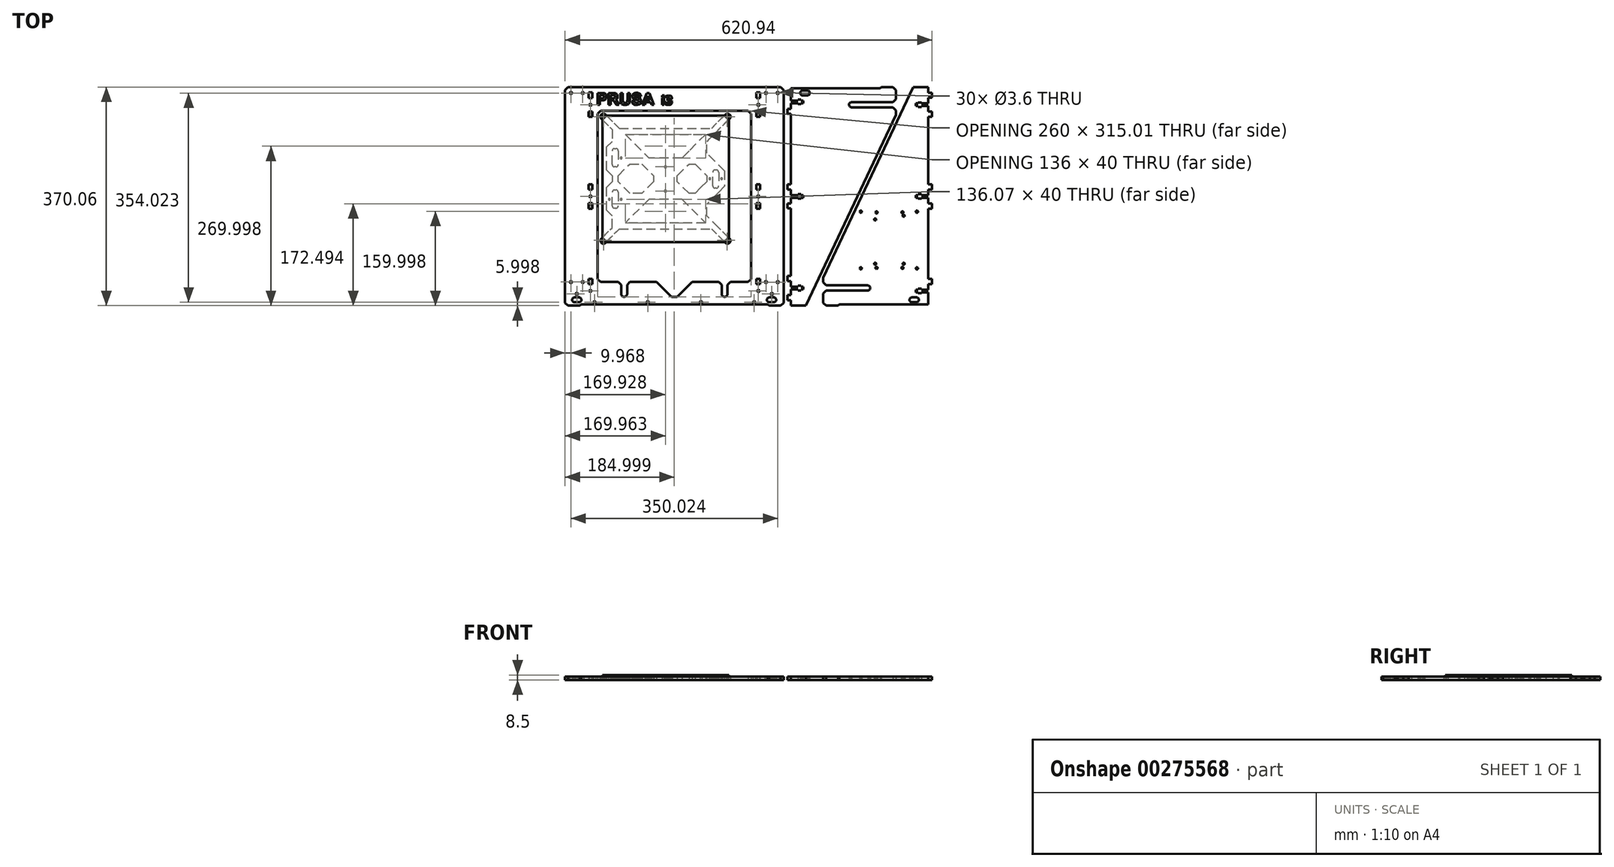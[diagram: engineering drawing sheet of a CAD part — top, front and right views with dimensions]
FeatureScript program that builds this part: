
annotation { "Feature Type Name" : "Feature", "Feature Type Description" : "" }
export const myFeature = defineFeature(function(context is Context, id is Id, definition is map)
    precondition{}
    {
        {
            var Q0;
            Q0=qCreatedBy(makeId("Top.planeOp"),FACE);
            var sketch = newSketch(context, id + "F0", { "sketchPlane" : qUnion([Q0])});
            skLineSegment(sketch, "E0", {"start": v(-112.47, -5.03) * mm, "end": v(-112.54, -5.03) * mm});
            skLineSegment(sketch, "E1", {"start": v(-72.47, -45.03) * mm, "end": v(-72.54, -45.03) * mm});
            skLineSegment(sketch, "E2", {"start": v(-168.47, -5.03) * mm, "end": v(-208.47, -45.03) * mm});
            skLineSegment(sketch, "E3", {"start": v(-112.47, -5.03) * mm, "end": v(-72.47, -45.03) * mm});
            skLineSegment(sketch, "E4", {"start": v(-112.54, -5.03) * mm, "end": v(-72.54, -45.03) * mm});
            skLineSegment(sketch, "E5", {"start": v(-168.54, -5.03) * mm, "end": v(-208.54, -45.03) * mm});
            skLineSegment(sketch, "E6", {"start": v(-208.47, -45.03) * mm, "end": v(-208.54, -45.03) * mm});
            skLineSegment(sketch, "E7", {"start": v(-168.47, -5.03) * mm, "end": v(-168.54, -5.03) * mm});
            skLineSegment(sketch, "E8", {"start": v(-305.47, -185.03) * mm, "end": v(-310.47, -180.22) * mm});
            skLineSegment(sketch, "E9", {"start": v(-310.47, 179.97) * mm, "end": v(-305.47, 184.97) * mm});
            skLineSegment(sketch, "E10", {"start": v(-305.47, 184.97) * mm, "end": v(54.53, 184.97) * mm});
            skLineSegment(sketch, "E11", {"start": v(54.53, 184.97) * mm, "end": v(59.53, 179.97) * mm});
            skLineSegment(sketch, "E12", {"start": v(59.53, -180.03) * mm, "end": v(54.53, -185.03) * mm});
            skLineSegment(sketch, "E13", {"start": v(34.53, -185.03) * mm, "end": v(32.53, -183.03) * mm});
            skLineSegment(sketch, "E14", {"start": v(32.53, -183.03) * mm, "end": v(-283.47, -183.03) * mm});
            skLineSegment(sketch, "E15", {"start": v(-283.47, -183.03) * mm, "end": v(-285.47, -185.03) * mm});
            skLineSegment(sketch, "E16", {"start": v(-230.47, -145.03) * mm, "end": v(-250.47, -145.03) * mm});
            skLineSegment(sketch, "E17", {"start": v(-250.47, -145.03) * mm, "end": v(-255.47, -140.03) * mm});
            skLineSegment(sketch, "E18", {"start": v(-255.47, -140.03) * mm, "end": v(-255.47, 139.97) * mm});
            skLineSegment(sketch, "E19", {"start": v(-255.47, 139.97) * mm, "end": v(-250.47, 144.97) * mm});
            skLineSegment(sketch, "E20", {"start": v(-250.47, 144.97) * mm, "end": v(-0.47, 144.97) * mm});
            skLineSegment(sketch, "E21", {"start": v(-0.47, 144.97) * mm, "end": v(4.53, 139.97) * mm});
            skLineSegment(sketch, "E22", {"start": v(4.53, 139.97) * mm, "end": v(4.53, -140.03) * mm});
            skLineSegment(sketch, "E23", {"start": v(4.53, -140.03) * mm, "end": v(-0.47, -145.03) * mm});
            skLineSegment(sketch, "E24", {"start": v(-0.47, -145.03) * mm, "end": v(-20.47, -145.03) * mm});
            skLineSegment(sketch, "E25", {"start": v(-130.47, -170.03) * mm, "end": v(-120.47, -170.03) * mm});
            skLineSegment(sketch, "E26", {"start": v(-120.47, -170.03) * mm, "end": v(-95.47, -145.03) * mm});
            skLineSegment(sketch, "E27", {"start": v(-130.47, -170.03) * mm, "end": v(-155.47, -145.03) * mm});
            skLineSegment(sketch, "E28", {"start": v(-200.47, -145.03) * mm, "end": v(-155.47, -145.03) * mm});
            skLineSegment(sketch, "E29", {"start": v(-95.47, -145.03) * mm, "end": v(-50.47, -145.03) * mm});
            skLineSegment(sketch, "E30", {"start": v(-80.47, 44.97) * mm, "end": v(-80.47, 44.9) * mm});
            skLineSegment(sketch, "E31", {"start": v(39.53, -179.03) * mm, "end": v(39.8, -179) * mm});
            skLineSegment(sketch, "E32", {"start": v(-310.47, -180.22) * mm, "end": v(-310.47, 179.97) * mm});
            skLineSegment(sketch, "E33", {"start": v(59.53, 179.97) * mm, "end": v(59.53, -180.03) * mm});
            skLineSegment(sketch, "E34", {"start": v(54.53, -185.03) * mm, "end": v(34.53, -185.03) * mm});
            skLineSegment(sketch, "E35", {"start": v(-285.47, -185.03) * mm, "end": v(-305.47, -185.03) * mm});
            skLineSegment(sketch, "E36", {"start": v(31.63, -173) * mm, "end": v(31.23, -173.96) * mm});
            skLineSegment(sketch, "E37", {"start": v(31.1, -175) * mm, "end": v(31.23, -176.03) * mm});
            skLineSegment(sketch, "E38", {"start": v(34.06, -171.13) * mm, "end": v(33.1, -171.53) * mm});
            skLineSegment(sketch, "E39", {"start": v(44.12, -171.13) * mm, "end": v(43.09, -171) * mm});
            skLineSegment(sketch, "E40", {"start": v(45.92, -177.82) * mm, "end": v(46.55, -177) * mm});
            skLineSegment(sketch, "E41", {"start": v(45.09, -178.46) * mm, "end": v(45.92, -177.82) * mm});
            skLineSegment(sketch, "E42", {"start": v(44.12, -178.86) * mm, "end": v(45.09, -178.46) * mm});
            skLineSegment(sketch, "E43", {"start": v(33.1, -178.46) * mm, "end": v(34.06, -178.86) * mm});
            skLineSegment(sketch, "E44", {"start": v(34.06, -178.86) * mm, "end": v(35.1, -179) * mm});
            skLineSegment(sketch, "E45", {"start": v(31.23, -176.03) * mm, "end": v(31.63, -177) * mm});
            skLineSegment(sketch, "E46", {"start": v(45.92, -172.17) * mm, "end": v(45.09, -171.53) * mm});
            skLineSegment(sketch, "E47", {"start": v(46.55, -173) * mm, "end": v(45.92, -172.17) * mm});
            skLineSegment(sketch, "E48", {"start": v(35.1, -171) * mm, "end": v(43.09, -171) * mm});
            skLineSegment(sketch, "E49", {"start": v(33.1, -171.53) * mm, "end": v(32.26, -172.17) * mm});
            skLineSegment(sketch, "E50", {"start": v(32.26, -172.17) * mm, "end": v(31.63, -173) * mm});
            skLineSegment(sketch, "E51", {"start": v(32.26, -177.82) * mm, "end": v(33.1, -178.46) * mm});
            skLineSegment(sketch, "E52", {"start": v(46.95, -173.96) * mm, "end": v(46.55, -173) * mm});
            skLineSegment(sketch, "E53", {"start": v(31.23, -173.96) * mm, "end": v(31.1, -175) * mm});
            skLineSegment(sketch, "E54", {"start": v(31.63, -177) * mm, "end": v(32.26, -177.82) * mm});
            skLineSegment(sketch, "E55", {"start": v(46.95, -176.03) * mm, "end": v(47.09, -175) * mm});
            skLineSegment(sketch, "E56", {"start": v(46.55, -177) * mm, "end": v(46.95, -176.03) * mm});
            skLineSegment(sketch, "E57", {"start": v(35.1, -171) * mm, "end": v(34.06, -171.13) * mm});
            skLineSegment(sketch, "E58", {"start": v(43.16, -179) * mm, "end": v(44.12, -178.86) * mm});
            skLineSegment(sketch, "E59", {"start": v(35.1, -179) * mm, "end": v(39.25, -179) * mm});
            skLineSegment(sketch, "E60", {"start": v(47.09, -175) * mm, "end": v(46.95, -173.96) * mm});
            skLineSegment(sketch, "E61", {"start": v(45.09, -171.53) * mm, "end": v(44.12, -171.13) * mm});
            skLineSegment(sketch, "E62", {"start": v(39.25, -179) * mm, "end": v(39.53, -179.03) * mm});
            skLineSegment(sketch, "E63", {"start": v(39.25, -179) * mm, "end": v(39.8, -179) * mm});
            skLineSegment(sketch, "E64", {"start": v(39.8, -179) * mm, "end": v(43.16, -179) * mm});
            skLineSegment(sketch, "E65", {"start": v(-298.44, -175) * mm, "end": v(-298.3, -176.03) * mm});
            skLineSegment(sketch, "E66", {"start": v(-297.9, -173) * mm, "end": v(-298.3, -173.96) * mm});
            skLineSegment(sketch, "E67", {"start": v(-295.48, -171.13) * mm, "end": v(-296.44, -171.53) * mm});
            skLineSegment(sketch, "E68", {"start": v(-285.41, -171.13) * mm, "end": v(-286.45, -171) * mm});
            skLineSegment(sketch, "E69", {"start": v(-283.62, -177.82) * mm, "end": v(-282.98, -177) * mm});
            skLineSegment(sketch, "E70", {"start": v(-284.45, -178.46) * mm, "end": v(-283.62, -177.82) * mm});
            skLineSegment(sketch, "E71", {"start": v(-285.41, -178.86) * mm, "end": v(-284.45, -178.46) * mm});
            skLineSegment(sketch, "E72", {"start": v(-296.44, -178.46) * mm, "end": v(-295.48, -178.86) * mm});
            skLineSegment(sketch, "E73", {"start": v(-295.48, -178.86) * mm, "end": v(-294.44, -179) * mm});
            skLineSegment(sketch, "E74", {"start": v(-298.3, -176.03) * mm, "end": v(-297.9, -177) * mm});
            skLineSegment(sketch, "E75", {"start": v(-283.62, -172.17) * mm, "end": v(-284.45, -171.53) * mm});
            skLineSegment(sketch, "E76", {"start": v(-282.98, -173) * mm, "end": v(-283.62, -172.17) * mm});
            skLineSegment(sketch, "E77", {"start": v(-294.44, -171) * mm, "end": v(-286.45, -171) * mm});
            skLineSegment(sketch, "E78", {"start": v(-296.44, -171.53) * mm, "end": v(-297.27, -172.17) * mm});
            skLineSegment(sketch, "E79", {"start": v(-297.27, -172.17) * mm, "end": v(-297.9, -173) * mm});
            skLineSegment(sketch, "E80", {"start": v(-297.27, -177.82) * mm, "end": v(-296.44, -178.46) * mm});
            skLineSegment(sketch, "E81", {"start": v(-282.59, -173.96) * mm, "end": v(-282.98, -173) * mm});
            skLineSegment(sketch, "E82", {"start": v(-298.3, -173.96) * mm, "end": v(-298.44, -175) * mm});
            skLineSegment(sketch, "E83", {"start": v(-297.9, -177) * mm, "end": v(-297.27, -177.82) * mm});
            skLineSegment(sketch, "E84", {"start": v(-282.59, -176.03) * mm, "end": v(-282.45, -175) * mm});
            skLineSegment(sketch, "E85", {"start": v(-282.98, -177) * mm, "end": v(-282.59, -176.03) * mm});
            skLineSegment(sketch, "E86", {"start": v(-294.44, -171) * mm, "end": v(-295.48, -171.13) * mm});
            skLineSegment(sketch, "E87", {"start": v(-286.38, -179) * mm, "end": v(-285.41, -178.86) * mm});
            skLineSegment(sketch, "E88", {"start": v(-294.44, -179) * mm, "end": v(-286.38, -179) * mm});
            skLineSegment(sketch, "E89", {"start": v(-282.45, -175) * mm, "end": v(-282.59, -173.96) * mm});
            skLineSegment(sketch, "E90", {"start": v(-284.45, -171.53) * mm, "end": v(-285.41, -171.13) * mm});
            skLineSegment(sketch, "E91", {"start": v(13.28, 166.71) * mm, "end": v(13.28, 175.71) * mm});
            skLineSegment(sketch, "E92", {"start": v(13.28, 175.71) * mm, "end": v(19.78, 175.71) * mm});
            skLineSegment(sketch, "E93", {"start": v(19.78, 175.71) * mm, "end": v(19.78, 166.71) * mm});
            skLineSegment(sketch, "E94", {"start": v(19.78, 166.71) * mm, "end": v(13.28, 166.71) * mm});
            skLineSegment(sketch, "E95", {"start": v(13.28, 134.41) * mm, "end": v(13.28, 143.41) * mm});
            skLineSegment(sketch, "E96", {"start": v(13.28, 143.41) * mm, "end": v(19.78, 143.41) * mm});
            skLineSegment(sketch, "E97", {"start": v(19.78, 143.41) * mm, "end": v(19.78, 134.41) * mm});
            skLineSegment(sketch, "E98", {"start": v(19.78, 134.41) * mm, "end": v(13.28, 134.41) * mm});
            skLineSegment(sketch, "E99", {"start": v(13.28, 11.62) * mm, "end": v(13.28, 20.62) * mm});
            skLineSegment(sketch, "E100", {"start": v(13.28, 20.62) * mm, "end": v(19.78, 20.62) * mm});
            skLineSegment(sketch, "E101", {"start": v(19.78, 20.62) * mm, "end": v(19.78, 11.62) * mm});
            skLineSegment(sketch, "E102", {"start": v(19.78, 11.62) * mm, "end": v(13.28, 11.62) * mm});
            skLineSegment(sketch, "E103", {"start": v(13.28, -20.68) * mm, "end": v(13.28, -11.68) * mm});
            skLineSegment(sketch, "E104", {"start": v(13.28, -11.68) * mm, "end": v(19.78, -11.68) * mm});
            skLineSegment(sketch, "E105", {"start": v(19.78, -11.68) * mm, "end": v(19.78, -20.68) * mm});
            skLineSegment(sketch, "E106", {"start": v(19.78, -20.68) * mm, "end": v(13.28, -20.68) * mm});
            skLineSegment(sketch, "E107", {"start": v(13.28, -148.38) * mm, "end": v(13.28, -139.38) * mm});
            skLineSegment(sketch, "E108", {"start": v(13.28, -139.38) * mm, "end": v(19.78, -139.38) * mm});
            skLineSegment(sketch, "E109", {"start": v(19.78, -139.38) * mm, "end": v(19.78, -148.38) * mm});
            skLineSegment(sketch, "E110", {"start": v(19.78, -148.38) * mm, "end": v(13.28, -148.38) * mm});
            skLineSegment(sketch, "E111", {"start": v(-270.72, 166.71) * mm, "end": v(-270.72, 175.71) * mm});
            skLineSegment(sketch, "E112", {"start": v(-270.72, 175.71) * mm, "end": v(-264.22, 175.71) * mm});
            skLineSegment(sketch, "E113", {"start": v(-264.22, 175.71) * mm, "end": v(-264.22, 166.71) * mm});
            skLineSegment(sketch, "E114", {"start": v(-264.22, 166.71) * mm, "end": v(-270.72, 166.71) * mm});
            skLineSegment(sketch, "E115", {"start": v(-270.72, 134.41) * mm, "end": v(-270.72, 143.41) * mm});
            skLineSegment(sketch, "E116", {"start": v(-270.72, 143.41) * mm, "end": v(-264.22, 143.41) * mm});
            skLineSegment(sketch, "E117", {"start": v(-264.22, 143.41) * mm, "end": v(-264.22, 134.41) * mm});
            skLineSegment(sketch, "E118", {"start": v(-264.22, 134.41) * mm, "end": v(-270.72, 134.41) * mm});
            skLineSegment(sketch, "E119", {"start": v(-270.72, 11.62) * mm, "end": v(-270.72, 20.62) * mm});
            skLineSegment(sketch, "E120", {"start": v(-270.72, 20.62) * mm, "end": v(-264.22, 20.62) * mm});
            skLineSegment(sketch, "E121", {"start": v(-264.22, 20.62) * mm, "end": v(-264.22, 11.62) * mm});
            skLineSegment(sketch, "E122", {"start": v(-264.22, 11.62) * mm, "end": v(-270.72, 11.62) * mm});
            skLineSegment(sketch, "E123", {"start": v(-270.72, -20.68) * mm, "end": v(-270.72, -11.68) * mm});
            skLineSegment(sketch, "E124", {"start": v(-270.72, -11.68) * mm, "end": v(-264.22, -11.68) * mm});
            skLineSegment(sketch, "E125", {"start": v(-264.22, -11.68) * mm, "end": v(-264.22, -20.68) * mm});
            skLineSegment(sketch, "E126", {"start": v(-264.22, -20.68) * mm, "end": v(-270.72, -20.68) * mm});
            skLineSegment(sketch, "E127", {"start": v(-270.72, -148.38) * mm, "end": v(-270.72, -139.38) * mm});
            skLineSegment(sketch, "E128", {"start": v(-270.72, -139.38) * mm, "end": v(-264.22, -139.38) * mm});
            skLineSegment(sketch, "E129", {"start": v(-264.22, -139.38) * mm, "end": v(-264.22, -148.38) * mm});
            skLineSegment(sketch, "E130", {"start": v(-264.22, -148.38) * mm, "end": v(-270.72, -148.38) * mm});
            skLineSegment(sketch, "E131", {"start": v(310.47, 134.51) * mm, "end": v(310.47, 143.31) * mm});
            skLineSegment(sketch, "E132", {"start": v(304.37, -148.28) * mm, "end": v(310.47, -148.28) * mm});
            skLineSegment(sketch, "E133", {"start": v(310.47, -148.28) * mm, "end": v(310.47, -139.48) * mm});
            skLineSegment(sketch, "E134", {"start": v(310.47, -139.48) * mm, "end": v(304.37, -139.48) * mm});
            skLineSegment(sketch, "E135", {"start": v(304.37, -139.48) * mm, "end": v(304.37, -20.58) * mm});
            skLineSegment(sketch, "E136", {"start": v(88.26, 177.03) * mm, "end": v(88.9, 177.86) * mm});
            skLineSegment(sketch, "E137", {"start": v(103.58, 176.07) * mm, "end": v(103.72, 175.03) * mm});
            skLineSegment(sketch, "E138", {"start": v(103.18, 177.03) * mm, "end": v(103.58, 176.07) * mm});
            skLineSegment(sketch, "E139", {"start": v(83.78, 2.23) * mm, "end": v(71.78, 2.23) * mm});
            skLineSegment(sketch, "E140", {"start": v(170.33, 156.17) * mm, "end": v(170.77, 157.23) * mm});
            skLineSegment(sketch, "E141", {"start": v(91.72, 171.03) * mm, "end": v(90.69, 171.17) * mm});
            skLineSegment(sketch, "E142", {"start": v(99.78, 179.03) * mm, "end": v(100.75, 178.9) * mm});
            skLineSegment(sketch, "E143", {"start": v(91.72, 179.03) * mm, "end": v(99.78, 179.03) * mm});
            skLineSegment(sketch, "E144", {"start": v(171.47, 151.92) * mm, "end": v(170.77, 152.83) * mm});
            skLineSegment(sketch, "E145", {"start": v(170.18, 155.03) * mm, "end": v(170.33, 156.17) * mm});
            skLineSegment(sketch, "E146", {"start": v(83.78, -3.97) * mm, "end": v(88.88, -3.97) * mm});
            skLineSegment(sketch, "E147", {"start": v(224.58, 185.03) * mm, "end": v(244.58, 185.03) * mm});
            skLineSegment(sketch, "E148", {"start": v(170.77, 157.23) * mm, "end": v(171.47, 158.14) * mm});
            skLineSegment(sketch, "E149", {"start": v(88.88, 162.24) * mm, "end": v(88.88, 164.04) * mm});
            skLineSegment(sketch, "E150", {"start": v(83.78, 162.24) * mm, "end": v(71.78, 162.24) * mm});
            skLineSegment(sketch, "E151", {"start": v(83.78, 164.04) * mm, "end": v(83.78, 162.24) * mm});
            skLineSegment(sketch, "E152", {"start": v(71.78, 157.84) * mm, "end": v(71.78, 148.28) * mm});
            skLineSegment(sketch, "E153", {"start": v(83.78, -151.05) * mm, "end": v(83.78, -152.85) * mm});
            skLineSegment(sketch, "E154", {"start": v(83.78, -157.25) * mm, "end": v(83.78, -159.05) * mm});
            skLineSegment(sketch, "E155", {"start": v(92.88, -157.25) * mm, "end": v(92.88, -152.85) * mm});
            skLineSegment(sketch, "E156", {"start": v(88.88, -157.25) * mm, "end": v(92.88, -157.25) * mm});
            skLineSegment(sketch, "E157", {"start": v(88.88, -157.25) * mm, "end": v(88.88, -159.05) * mm});
            skLineSegment(sketch, "E158", {"start": v(71.78, -157.25) * mm, "end": v(83.78, -157.25) * mm});
            skLineSegment(sketch, "E159", {"start": v(92.88, -152.85) * mm, "end": v(88.88, -152.85) * mm});
            skLineSegment(sketch, "E160", {"start": v(83.78, -152.85) * mm, "end": v(71.78, -152.85) * mm});
            skLineSegment(sketch, "E161", {"start": v(88.88, -151.05) * mm, "end": v(83.78, -151.05) * mm});
            skLineSegment(sketch, "E162", {"start": v(304.37, -183.03) * mm, "end": v(153.57, -183.03) * mm});
            skLineSegment(sketch, "E163", {"start": v(273.61, -172.2) * mm, "end": v(274.44, -171.57) * mm});
            skLineSegment(sketch, "E164", {"start": v(272.97, -173.03) * mm, "end": v(273.61, -172.2) * mm});
            skLineSegment(sketch, "E165", {"start": v(284.43, -171.03) * mm, "end": v(276.44, -171.03) * mm});
            skLineSegment(sketch, "E166", {"start": v(203.77, -151.22) * mm, "end": v(204.68, -151.92) * mm});
            skLineSegment(sketch, "E167", {"start": v(283.27, -2.23) * mm, "end": v(287.27, -2.23) * mm});
            skLineSegment(sketch, "E168", {"start": v(202.71, -150.78) * mm, "end": v(203.77, -151.22) * mm});
            skLineSegment(sketch, "E169", {"start": v(287.27, -4.03) * mm, "end": v(292.37, -4.03) * mm});
            skLineSegment(sketch, "E170", {"start": v(286.43, -171.57) * mm, "end": v(287.26, -172.2) * mm});
            skLineSegment(sketch, "E171", {"start": v(304.37, -157.84) * mm, "end": v(292.37, -157.84) * mm});
            skLineSegment(sketch, "E172", {"start": v(292.37, -157.84) * mm, "end": v(292.37, -156.04) * mm});
            skLineSegment(sketch, "E173", {"start": v(283.27, -162.24) * mm, "end": v(287.27, -162.24) * mm});
            skLineSegment(sketch, "E174", {"start": v(287.27, -164.04) * mm, "end": v(292.37, -164.04) * mm});
            skLineSegment(sketch, "E175", {"start": v(292.37, -156.04) * mm, "end": v(287.27, -156.04) * mm});
            skLineSegment(sketch, "E176", {"start": v(287.27, -162.24) * mm, "end": v(287.27, -164.04) * mm});
            skLineSegment(sketch, "E177", {"start": v(292.37, -162.24) * mm, "end": v(304.37, -162.24) * mm});
            skLineSegment(sketch, "E178", {"start": v(292.37, -164.04) * mm, "end": v(292.37, -162.24) * mm});
            skLineSegment(sketch, "E179", {"start": v(304.37, -157.84) * mm, "end": v(304.37, -148.28) * mm});
            skLineSegment(sketch, "E180", {"start": v(103.58, 174) * mm, "end": v(103.18, 173.03) * mm});
            skLineSegment(sketch, "E181", {"start": v(273.61, -177.86) * mm, "end": v(272.97, -177.03) * mm});
            skLineSegment(sketch, "E182", {"start": v(274.44, -178.5) * mm, "end": v(273.61, -177.86) * mm});
            skLineSegment(sketch, "E183", {"start": v(275.4, -178.9) * mm, "end": v(274.44, -178.5) * mm});
            skLineSegment(sketch, "E184", {"start": v(304.37, 2.17) * mm, "end": v(292.37, 2.17) * mm});
            skLineSegment(sketch, "E185", {"start": v(286.43, -178.5) * mm, "end": v(285.47, -178.9) * mm});
            skLineSegment(sketch, "E186", {"start": v(285.47, -178.9) * mm, "end": v(284.43, -179.03) * mm});
            skLineSegment(sketch, "E187", {"start": v(288.3, -176.07) * mm, "end": v(287.9, -177.03) * mm});
            skLineSegment(sketch, "E188", {"start": v(203.77, -158.84) * mm, "end": v(202.71, -159.28) * mm});
            skLineSegment(sketch, "E189", {"start": v(71.78, -175.61) * mm, "end": v(71.78, -184.97) * mm});
            skLineSegment(sketch, "E190", {"start": v(65.68, -143.31) * mm, "end": v(71.78, -143.31) * mm});
            skLineSegment(sketch, "E191", {"start": v(71.78, -134.51) * mm, "end": v(65.68, -134.51) * mm});
            skLineSegment(sketch, "E192", {"start": v(65.68, -134.51) * mm, "end": v(65.68, -143.31) * mm});
            skLineSegment(sketch, "E193", {"start": v(71.78, 148.28) * mm, "end": v(65.68, 148.28) * mm});
            skLineSegment(sketch, "E194", {"start": v(65.68, 148.28) * mm, "end": v(65.68, 139.48) * mm});
            skLineSegment(sketch, "E195", {"start": v(65.68, 139.48) * mm, "end": v(71.78, 139.48) * mm});
            skLineSegment(sketch, "E196", {"start": v(71.78, 139.48) * mm, "end": v(71.78, 20.58) * mm});
            skLineSegment(sketch, "E197", {"start": v(83.78, -2.17) * mm, "end": v(83.78, -3.97) * mm});
            skLineSegment(sketch, "E198", {"start": v(244.58, 185.03) * mm, "end": v(249.58, 180.03) * mm});
            skLineSegment(sketch, "E199", {"start": v(222.58, 183.03) * mm, "end": v(224.58, 185.03) * mm});
            skLineSegment(sketch, "E200", {"start": v(87.86, 174) * mm, "end": v(87.72, 175.03) * mm});
            skLineSegment(sketch, "E201", {"start": v(310.47, 20.52) * mm, "end": v(304.37, 20.52) * mm});
            skLineSegment(sketch, "E202", {"start": v(304.37, 20.52) * mm, "end": v(304.37, 134.51) * mm});
            skLineSegment(sketch, "E203", {"start": v(310.47, -11.78) * mm, "end": v(304.37, -11.78) * mm});
            skLineSegment(sketch, "E204", {"start": v(304.37, -20.58) * mm, "end": v(310.47, -20.58) * mm});
            skLineSegment(sketch, "E205", {"start": v(310.47, -20.58) * mm, "end": v(310.47, -11.78) * mm});
            skLineSegment(sketch, "E206", {"start": v(304.37, 11.72) * mm, "end": v(304.37, 2.17) * mm});
            skLineSegment(sketch, "E207", {"start": v(304.37, -2.23) * mm, "end": v(304.37, -11.78) * mm});
            skLineSegment(sketch, "E208", {"start": v(304.37, 166.81) * mm, "end": v(310.47, 166.81) * mm});
            skLineSegment(sketch, "E209", {"start": v(310.47, 166.81) * mm, "end": v(310.47, 175.61) * mm});
            skLineSegment(sketch, "E210", {"start": v(310.47, 175.61) * mm, "end": v(304.37, 175.61) * mm});
            skLineSegment(sketch, "E211", {"start": v(304.37, 175.61) * mm, "end": v(304.37, 184.97) * mm});
            skLineSegment(sketch, "E212", {"start": v(310.47, 143.31) * mm, "end": v(304.37, 143.31) * mm});
            skLineSegment(sketch, "E213", {"start": v(304.37, 134.51) * mm, "end": v(310.47, 134.51) * mm});
            skLineSegment(sketch, "E214", {"start": v(92.88, -2.17) * mm, "end": v(92.88, 2.23) * mm});
            skLineSegment(sketch, "E215", {"start": v(249.58, 138.03) * mm, "end": v(97.18, -184.97) * mm});
            skLineSegment(sketch, "E216", {"start": v(88.88, -2.17) * mm, "end": v(92.88, -2.17) * mm});
            skLineSegment(sketch, "E217", {"start": v(88.88, -2.17) * mm, "end": v(88.88, -3.97) * mm});
            skLineSegment(sketch, "E218", {"start": v(100.75, 171.17) * mm, "end": v(99.72, 171.03) * mm});
            skLineSegment(sketch, "E219", {"start": v(71.78, -184.97) * mm, "end": v(97.18, -184.97) * mm});
            skLineSegment(sketch, "E220", {"start": v(71.78, 2.23) * mm, "end": v(71.78, 11.78) * mm});
            skLineSegment(sketch, "E221", {"start": v(71.78, -166.81) * mm, "end": v(65.68, -166.81) * mm});
            skLineSegment(sketch, "E222", {"start": v(65.68, -166.81) * mm, "end": v(65.68, -175.61) * mm});
            skLineSegment(sketch, "E223", {"start": v(65.68, -175.61) * mm, "end": v(71.78, -175.61) * mm});
            skLineSegment(sketch, "E224", {"start": v(126.57, -180.03) * mm, "end": v(126.57, -164.43) * mm});
            skLineSegment(sketch, "E225", {"start": v(287.9, -173.03) * mm, "end": v(288.3, -174) * mm});
            skLineSegment(sketch, "E226", {"start": v(288.43, -175.03) * mm, "end": v(288.3, -176.07) * mm});
            skLineSegment(sketch, "E227", {"start": v(285.47, -171.17) * mm, "end": v(286.43, -171.57) * mm});
            skLineSegment(sketch, "E228", {"start": v(292.37, -4.03) * mm, "end": v(292.37, -2.23) * mm});
            skLineSegment(sketch, "E229", {"start": v(83.78, -159.05) * mm, "end": v(88.88, -159.05) * mm});
            skLineSegment(sketch, "E230", {"start": v(88.88, -152.85) * mm, "end": v(88.88, -151.05) * mm});
            skLineSegment(sketch, "E231", {"start": v(71.78, -157.25) * mm, "end": v(71.78, -166.81) * mm});
            skLineSegment(sketch, "E232", {"start": v(71.78, -152.85) * mm, "end": v(71.78, -143.31) * mm});
            skLineSegment(sketch, "E233", {"start": v(92.88, 157.84) * mm, "end": v(92.88, 162.24) * mm});
            skLineSegment(sketch, "E234", {"start": v(88.88, 157.84) * mm, "end": v(92.88, 157.84) * mm});
            skLineSegment(sketch, "E235", {"start": v(88.88, 157.84) * mm, "end": v(88.88, 156.04) * mm});
            skLineSegment(sketch, "E236", {"start": v(71.78, 157.84) * mm, "end": v(83.78, 157.84) * mm});
            skLineSegment(sketch, "E237", {"start": v(83.78, 157.84) * mm, "end": v(83.78, 156.04) * mm});
            skLineSegment(sketch, "E238", {"start": v(92.88, 162.24) * mm, "end": v(88.88, 162.24) * mm});
            skLineSegment(sketch, "E239", {"start": v(174.58, 150.63) * mm, "end": v(173.45, 150.78) * mm});
            skLineSegment(sketch, "E240", {"start": v(102.55, 177.86) * mm, "end": v(103.18, 177.03) * mm});
            skLineSegment(sketch, "E241", {"start": v(101.72, 178.5) * mm, "end": v(102.55, 177.86) * mm});
            skLineSegment(sketch, "E242", {"start": v(100.75, 178.9) * mm, "end": v(101.72, 178.5) * mm});
            skLineSegment(sketch, "E243", {"start": v(71.78, -2.17) * mm, "end": v(83.78, -2.17) * mm});
            skLineSegment(sketch, "E244", {"start": v(89.72, 178.5) * mm, "end": v(90.69, 178.9) * mm});
            skLineSegment(sketch, "E245", {"start": v(90.69, 178.9) * mm, "end": v(91.72, 179.03) * mm});
            skLineSegment(sketch, "E246", {"start": v(87.86, 176.07) * mm, "end": v(88.26, 177.03) * mm});
            skLineSegment(sketch, "E247", {"start": v(172.38, 158.84) * mm, "end": v(173.45, 159.28) * mm});
            skLineSegment(sketch, "E248", {"start": v(283.27, 2.17) * mm, "end": v(283.27, -2.23) * mm});
            skLineSegment(sketch, "E249", {"start": v(126.57, -138.03) * mm, "end": v(278.97, 184.97) * mm});
            skLineSegment(sketch, "E250", {"start": v(287.27, 2.17) * mm, "end": v(283.27, 2.17) * mm});
            skLineSegment(sketch, "E251", {"start": v(287.27, 2.17) * mm, "end": v(287.27, 3.97) * mm});
            skLineSegment(sketch, "E252", {"start": v(275.4, -171.17) * mm, "end": v(276.44, -171.03) * mm});
            skLineSegment(sketch, "E253", {"start": v(304.37, 184.97) * mm, "end": v(278.97, 184.97) * mm});
            skLineSegment(sketch, "E254", {"start": v(201.57, -150.63) * mm, "end": v(202.71, -150.78) * mm});
            skLineSegment(sketch, "E255", {"start": v(272.97, -177.03) * mm, "end": v(272.57, -176.07) * mm});
            skLineSegment(sketch, "E256", {"start": v(292.37, -2.23) * mm, "end": v(304.37, -2.23) * mm});
            skLineSegment(sketch, "E257", {"start": v(205.82, -156.17) * mm, "end": v(205.38, -157.23) * mm});
            skLineSegment(sketch, "E258", {"start": v(284.43, -171.03) * mm, "end": v(285.47, -171.17) * mm});
            skLineSegment(sketch, "E259", {"start": v(276.37, -179.03) * mm, "end": v(275.4, -178.9) * mm});
            skLineSegment(sketch, "E260", {"start": v(284.43, -179.03) * mm, "end": v(276.37, -179.03) * mm});
            skLineSegment(sketch, "E261", {"start": v(204.68, -151.92) * mm, "end": v(205.38, -152.83) * mm});
            skLineSegment(sketch, "E262", {"start": v(205.97, -155.03) * mm, "end": v(205.82, -156.17) * mm});
            skLineSegment(sketch, "E263", {"start": v(292.37, 3.97) * mm, "end": v(287.27, 3.97) * mm});
            skLineSegment(sketch, "E264", {"start": v(151.57, -185.03) * mm, "end": v(131.57, -185.03) * mm});
            skLineSegment(sketch, "E265", {"start": v(205.38, -157.23) * mm, "end": v(204.68, -158.14) * mm});
            skLineSegment(sketch, "E266", {"start": v(287.27, -2.23) * mm, "end": v(287.27, -4.03) * mm});
            skLineSegment(sketch, "E267", {"start": v(283.27, 157.25) * mm, "end": v(283.27, 152.85) * mm});
            skLineSegment(sketch, "E268", {"start": v(287.27, 157.25) * mm, "end": v(283.27, 157.25) * mm});
            skLineSegment(sketch, "E269", {"start": v(287.27, 157.25) * mm, "end": v(287.27, 159.05) * mm});
            skLineSegment(sketch, "E270", {"start": v(304.37, 157.25) * mm, "end": v(292.37, 157.25) * mm});
            skLineSegment(sketch, "E271", {"start": v(283.27, 152.85) * mm, "end": v(287.27, 152.85) * mm});
            skLineSegment(sketch, "E272", {"start": v(292.37, 152.85) * mm, "end": v(304.37, 152.85) * mm});
            skLineSegment(sketch, "E273", {"start": v(287.27, 151.05) * mm, "end": v(292.37, 151.05) * mm});
            skLineSegment(sketch, "E274", {"start": v(292.37, 159.05) * mm, "end": v(287.27, 159.05) * mm});
            skLineSegment(sketch, "E275", {"start": v(287.27, 152.85) * mm, "end": v(287.27, 151.05) * mm});
            skLineSegment(sketch, "E276", {"start": v(304.37, 157.25) * mm, "end": v(304.37, 166.81) * mm});
            skLineSegment(sketch, "E277", {"start": v(304.37, 152.85) * mm, "end": v(304.37, 143.31) * mm});
            skLineSegment(sketch, "E278", {"start": v(283.27, -157.84) * mm, "end": v(283.27, -162.24) * mm});
            skLineSegment(sketch, "E279", {"start": v(287.27, -157.84) * mm, "end": v(283.27, -157.84) * mm});
            skLineSegment(sketch, "E280", {"start": v(287.27, -157.84) * mm, "end": v(287.27, -156.04) * mm});
            skLineSegment(sketch, "E281", {"start": v(292.37, 151.05) * mm, "end": v(292.37, 152.85) * mm});
            skLineSegment(sketch, "E282", {"start": v(292.37, 157.25) * mm, "end": v(292.37, 159.05) * mm});
            skLineSegment(sketch, "E283", {"start": v(88.88, 2.23) * mm, "end": v(88.88, 4.03) * mm});
            skLineSegment(sketch, "E284", {"start": v(171.47, 158.14) * mm, "end": v(172.38, 158.84) * mm});
            skLineSegment(sketch, "E285", {"start": v(103.72, 175.03) * mm, "end": v(103.58, 174) * mm});
            skLineSegment(sketch, "E286", {"start": v(101.72, 171.57) * mm, "end": v(100.75, 171.17) * mm});
            skLineSegment(sketch, "E287", {"start": v(244.58, 159.43) * mm, "end": v(174.58, 159.43) * mm});
            skLineSegment(sketch, "E288", {"start": v(244.58, 159.43) * mm, "end": v(249.58, 164.43) * mm});
            skLineSegment(sketch, "E289", {"start": v(244.58, 150.63) * mm, "end": v(174.58, 150.63) * mm});
            skLineSegment(sketch, "E290", {"start": v(249.58, 145.63) * mm, "end": v(249.58, 138.03) * mm});
            skLineSegment(sketch, "E291", {"start": v(244.58, 150.63) * mm, "end": v(249.58, 145.63) * mm});
            skLineSegment(sketch, "E292", {"start": v(71.78, -11.72) * mm, "end": v(65.68, -11.72) * mm});
            skLineSegment(sketch, "E293", {"start": v(65.68, -11.72) * mm, "end": v(65.68, -20.52) * mm});
            skLineSegment(sketch, "E294", {"start": v(65.68, -20.52) * mm, "end": v(71.78, -20.52) * mm});
            skLineSegment(sketch, "E295", {"start": v(71.78, -20.52) * mm, "end": v(71.78, -134.51) * mm});
            skLineSegment(sketch, "E296", {"start": v(65.68, 11.78) * mm, "end": v(71.78, 11.78) * mm});
            skLineSegment(sketch, "E297", {"start": v(71.78, 20.58) * mm, "end": v(65.68, 20.58) * mm});
            skLineSegment(sketch, "E298", {"start": v(65.68, 20.58) * mm, "end": v(65.68, 11.78) * mm});
            skLineSegment(sketch, "E299", {"start": v(71.78, -11.72) * mm, "end": v(71.78, -2.17) * mm});
            skLineSegment(sketch, "E300", {"start": v(88.88, 164.04) * mm, "end": v(83.78, 164.04) * mm});
            skLineSegment(sketch, "E301", {"start": v(91.72, 171.03) * mm, "end": v(99.72, 171.03) * mm});
            skLineSegment(sketch, "E302", {"start": v(172.38, 151.22) * mm, "end": v(171.47, 151.92) * mm});
            skLineSegment(sketch, "E303", {"start": v(92.88, 2.23) * mm, "end": v(88.88, 2.23) * mm});
            skLineSegment(sketch, "E304", {"start": v(173.45, 150.78) * mm, "end": v(172.38, 151.22) * mm});
            skLineSegment(sketch, "E305", {"start": v(88.88, 4.03) * mm, "end": v(83.78, 4.03) * mm});
            skLineSegment(sketch, "E306", {"start": v(83.78, 156.04) * mm, "end": v(88.88, 156.04) * mm});
            skLineSegment(sketch, "E307", {"start": v(89.72, 171.57) * mm, "end": v(88.9, 172.2) * mm});
            skLineSegment(sketch, "E308", {"start": v(88.9, 172.2) * mm, "end": v(88.26, 173.03) * mm});
            skLineSegment(sketch, "E309", {"start": v(88.9, 177.86) * mm, "end": v(89.72, 178.5) * mm});
            skLineSegment(sketch, "E310", {"start": v(170.77, 152.83) * mm, "end": v(170.33, 153.9) * mm});
            skLineSegment(sketch, "E311", {"start": v(170.33, 153.9) * mm, "end": v(170.18, 155.03) * mm});
            skLineSegment(sketch, "E312", {"start": v(71.78, 183.03) * mm, "end": v(71.78, 162.24) * mm});
            skLineSegment(sketch, "E313", {"start": v(173.45, 159.28) * mm, "end": v(174.58, 159.43) * mm});
            skLineSegment(sketch, "E314", {"start": v(249.58, 180.03) * mm, "end": v(249.58, 164.43) * mm});
            skLineSegment(sketch, "E315", {"start": v(88.26, 173.03) * mm, "end": v(87.86, 174) * mm});
            skLineSegment(sketch, "E316", {"start": v(87.72, 175.03) * mm, "end": v(87.86, 176.07) * mm});
            skLineSegment(sketch, "E317", {"start": v(90.69, 171.17) * mm, "end": v(89.72, 171.57) * mm});
            skLineSegment(sketch, "E318", {"start": v(83.78, 4.03) * mm, "end": v(83.78, 2.23) * mm});
            skLineSegment(sketch, "E319", {"start": v(204.68, -158.14) * mm, "end": v(203.77, -158.84) * mm});
            skLineSegment(sketch, "E320", {"start": v(272.44, -175.03) * mm, "end": v(272.57, -174) * mm});
            skLineSegment(sketch, "E321", {"start": v(274.44, -171.57) * mm, "end": v(275.4, -171.17) * mm});
            skLineSegment(sketch, "E322", {"start": v(131.57, -159.43) * mm, "end": v(201.57, -159.43) * mm});
            skLineSegment(sketch, "E323", {"start": v(131.57, -159.43) * mm, "end": v(126.57, -164.43) * mm});
            skLineSegment(sketch, "E324", {"start": v(131.57, -150.63) * mm, "end": v(201.57, -150.63) * mm});
            skLineSegment(sketch, "E325", {"start": v(126.57, -145.63) * mm, "end": v(126.57, -138.03) * mm});
            skLineSegment(sketch, "E326", {"start": v(131.57, -150.63) * mm, "end": v(126.57, -145.63) * mm});
            skLineSegment(sketch, "E327", {"start": v(304.37, 11.72) * mm, "end": v(310.47, 11.72) * mm});
            skLineSegment(sketch, "E328", {"start": v(310.47, 11.72) * mm, "end": v(310.47, 20.52) * mm});
            skLineSegment(sketch, "E329", {"start": v(287.26, -172.2) * mm, "end": v(287.9, -173.03) * mm});
            skLineSegment(sketch, "E330", {"start": v(287.26, -177.86) * mm, "end": v(286.43, -178.5) * mm});
            skLineSegment(sketch, "E331", {"start": v(205.38, -152.83) * mm, "end": v(205.82, -153.9) * mm});
            skLineSegment(sketch, "E332", {"start": v(205.82, -153.9) * mm, "end": v(205.97, -155.03) * mm});
            skLineSegment(sketch, "E333", {"start": v(272.57, -174) * mm, "end": v(272.97, -173.03) * mm});
            skLineSegment(sketch, "E334", {"start": v(292.37, 2.17) * mm, "end": v(292.37, 3.97) * mm});
            skLineSegment(sketch, "E335", {"start": v(131.57, -185.03) * mm, "end": v(126.57, -180.03) * mm});
            skLineSegment(sketch, "E336", {"start": v(153.57, -183.03) * mm, "end": v(151.57, -185.03) * mm});
            skLineSegment(sketch, "E337", {"start": v(288.3, -174) * mm, "end": v(288.43, -175.03) * mm});
            skLineSegment(sketch, "E338", {"start": v(287.9, -177.03) * mm, "end": v(287.26, -177.86) * mm});
            skLineSegment(sketch, "E339", {"start": v(272.57, -176.07) * mm, "end": v(272.44, -175.03) * mm});
            skLineSegment(sketch, "E340", {"start": v(304.37, -183.03) * mm, "end": v(304.37, -162.24) * mm});
            skLineSegment(sketch, "E341", {"start": v(202.71, -159.28) * mm, "end": v(201.57, -159.43) * mm});
            skLineSegment(sketch, "E342", {"start": v(71.78, 183.03) * mm, "end": v(222.58, 183.03) * mm});
            skLineSegment(sketch, "E343", {"start": v(102.55, 172.2) * mm, "end": v(101.72, 171.57) * mm});
            skLineSegment(sketch, "E344", {"start": v(103.18, 173.03) * mm, "end": v(102.55, 172.2) * mm});
            skLineSegment(sketch, "E345", {"start": v(188.2, -26.36) * mm, "end": v(188.15, -25.9) * mm});
            skLineSegment(sketch, "E346", {"start": v(286.7, -121.34) * mm, "end": v(286.76, -121.8) * mm});
            skLineSegment(sketch, "E347", {"start": v(286.52, -120.9) * mm, "end": v(286.7, -121.34) * mm});
            skLineSegment(sketch, "E348", {"start": v(286.24, -120.54) * mm, "end": v(286.52, -120.9) * mm});
            skLineSegment(sketch, "E349", {"start": v(191.68, -26.36) * mm, "end": v(191.5, -26.8) * mm});
            skLineSegment(sketch, "E350", {"start": v(191.24, -123.04) * mm, "end": v(190.87, -123.33) * mm});
            skLineSegment(sketch, "E351", {"start": v(191.53, -122.67) * mm, "end": v(191.24, -123.04) * mm});
            skLineSegment(sketch, "E352", {"start": v(189.07, -123.32) * mm, "end": v(188.7, -123.04) * mm});
            skLineSegment(sketch, "E353", {"start": v(188.41, -122.67) * mm, "end": v(188.23, -122.23) * mm});
            skLineSegment(sketch, "E354", {"start": v(189.5, -120.03) * mm, "end": v(189.9, -119.98) * mm});
            skLineSegment(sketch, "E355", {"start": v(286.74, -25.85) * mm, "end": v(286.68, -26.32) * mm});
            skLineSegment(sketch, "E356", {"start": v(285.4, -27.6) * mm, "end": v(284.94, -27.65) * mm});
            skLineSegment(sketch, "E357", {"start": v(188.39, -25) * mm, "end": v(188.67, -24.63) * mm});
            skLineSegment(sketch, "E358", {"start": v(189.9, -27.7) * mm, "end": v(189.48, -27.64) * mm});
            skLineSegment(sketch, "E359", {"start": v(284.04, -27.41) * mm, "end": v(283.67, -27.13) * mm});
            skLineSegment(sketch, "E360", {"start": v(283.17, -121.84) * mm, "end": v(283.16, -121.8) * mm});
            skLineSegment(sketch, "E361", {"start": v(189.48, -24.16) * mm, "end": v(189.95, -24.1) * mm});
            skLineSegment(sketch, "E362", {"start": v(284.06, -123.37) * mm, "end": v(283.69, -123.08) * mm});
            skLineSegment(sketch, "E363", {"start": v(213.85, -37.27) * mm, "end": v(214.31, -37.2) * mm});
            skLineSegment(sketch, "E364", {"start": v(212.75, -38.1) * mm, "end": v(213.04, -37.74) * mm});
            skLineSegment(sketch, "E365", {"start": v(189.04, -27.46) * mm, "end": v(188.67, -27.17) * mm});
            skLineSegment(sketch, "E366", {"start": v(216.08, -114.42) * mm, "end": v(215.9, -114.85) * mm});
            skLineSegment(sketch, "E367", {"start": v(215.9, -114.85) * mm, "end": v(215.62, -115.23) * mm});
            skLineSegment(sketch, "E368", {"start": v(190.41, -24.16) * mm, "end": v(190.85, -24.34) * mm});
            skLineSegment(sketch, "E369", {"start": v(285.43, -120.07) * mm, "end": v(285.86, -120.25) * mm});
            skLineSegment(sketch, "E370", {"start": v(283.69, -120.54) * mm, "end": v(284.06, -120.25) * mm});
            skLineSegment(sketch, "E371", {"start": v(283.4, -120.9) * mm, "end": v(283.69, -120.54) * mm});
            skLineSegment(sketch, "E372", {"start": v(283.22, -121.34) * mm, "end": v(283.4, -120.9) * mm});
            skLineSegment(sketch, "E373", {"start": v(189.95, -24.1) * mm, "end": v(190.41, -24.16) * mm});
            skLineSegment(sketch, "E374", {"start": v(213.07, -115.23) * mm, "end": v(212.79, -114.85) * mm});
            skLineSegment(sketch, "E375", {"start": v(212.79, -114.85) * mm, "end": v(212.6, -114.42) * mm});
            skLineSegment(sketch, "E376", {"start": v(263.48, -34.27) * mm, "end": v(263.04, -34.45) * mm});
            skLineSegment(sketch, "E377", {"start": v(259.04, -108.12) * mm, "end": v(259.04, -110.32) * mm});
            skLineSegment(sketch, "E378", {"start": v(259.04, -110.32) * mm, "end": v(258.74, -110.32) * mm});
            skLineSegment(sketch, "E379", {"start": v(259.04, -110.32) * mm, "end": v(259.36, -110.32) * mm});
            skLineSegment(sketch, "E380", {"start": v(188.23, -122.23) * mm, "end": v(188.17, -121.77) * mm});
            skLineSegment(sketch, "E381", {"start": v(189.07, -120.2) * mm, "end": v(189.5, -120.03) * mm});
            skLineSegment(sketch, "E382", {"start": v(261.02, -33.6) * mm, "end": v(260.84, -33.17) * mm});
            skLineSegment(sketch, "E383", {"start": v(262.11, -30.97) * mm, "end": v(262.58, -30.9) * mm});
            skLineSegment(sketch, "E384", {"start": v(263.48, -31.15) * mm, "end": v(263.62, -31.26) * mm});
            skLineSegment(sketch, "E385", {"start": v(264.14, -31.8) * mm, "end": v(264.32, -32.24) * mm});
            skLineSegment(sketch, "E386", {"start": v(286.76, -121.8) * mm, "end": v(286.7, -122.28) * mm});
            skLineSegment(sketch, "E387", {"start": v(190.41, -27.64) * mm, "end": v(189.94, -27.7) * mm});
            skLineSegment(sketch, "E388", {"start": v(189.94, -27.7) * mm, "end": v(189.9, -27.7) * mm});
            skLineSegment(sketch, "E389", {"start": v(191.48, -31.81) * mm, "end": v(192.63, -31.81) * mm});
            skLineSegment(sketch, "E390", {"start": v(191.48, -31.81) * mm, "end": v(191.48, -30.71) * mm});
            skLineSegment(sketch, "E391", {"start": v(262.11, -34.45) * mm, "end": v(261.75, -34.3) * mm});
            skLineSegment(sketch, "E392", {"start": v(216.05, -38.54) * mm, "end": v(216.11, -39) * mm});
            skLineSegment(sketch, "E393", {"start": v(213.04, -37.74) * mm, "end": v(213.41, -37.45) * mm});
            skLineSegment(sketch, "E394", {"start": v(213.41, -37.45) * mm, "end": v(213.85, -37.27) * mm});
            skLineSegment(sketch, "E395", {"start": v(190.44, -120.03) * mm, "end": v(190.87, -120.2) * mm});
            skLineSegment(sketch, "E396", {"start": v(189.97, -119.97) * mm, "end": v(190.44, -120.03) * mm});
            skLineSegment(sketch, "E397", {"start": v(284.96, -120) * mm, "end": v(285.43, -120.07) * mm});
            skLineSegment(sketch, "E398", {"start": v(283.22, -122.28) * mm, "end": v(283.17, -121.84) * mm});
            skLineSegment(sketch, "E399", {"start": v(215.87, -39.9) * mm, "end": v(215.59, -40.28) * mm});
            skLineSegment(sketch, "E400", {"start": v(214.78, -40.75) * mm, "end": v(214.31, -40.8) * mm});
            skLineSegment(sketch, "E401", {"start": v(259.18, -36) * mm, "end": v(258.88, -36.3) * mm});
            skLineSegment(sketch, "E402", {"start": v(216.99, -42.2) * mm, "end": v(216.69, -42.51) * mm});
            skLineSegment(sketch, "E403", {"start": v(216.99, -44.4) * mm, "end": v(217.3, -44.4) * mm});
            skLineSegment(sketch, "E404", {"start": v(216.99, -44.4) * mm, "end": v(216.69, -44.4) * mm});
            skLineSegment(sketch, "E405", {"start": v(283.16, -121.8) * mm, "end": v(283.22, -121.34) * mm});
            skLineSegment(sketch, "E406", {"start": v(284.5, -123.55) * mm, "end": v(284.06, -123.37) * mm});
            skLineSegment(sketch, "E407", {"start": v(283.2, -25.39) * mm, "end": v(283.38, -24.95) * mm});
            skLineSegment(sketch, "E408", {"start": v(191.75, -25.9) * mm, "end": v(191.68, -26.36) * mm});
            skLineSegment(sketch, "E409", {"start": v(261.3, -31.44) * mm, "end": v(261.68, -31.15) * mm});
            skLineSegment(sketch, "E410", {"start": v(261.02, -31.8) * mm, "end": v(261.3, -31.44) * mm});
            skLineSegment(sketch, "E411", {"start": v(188.2, -25.43) * mm, "end": v(188.39, -25) * mm});
            skLineSegment(sketch, "E412", {"start": v(260.84, -33.17) * mm, "end": v(260.78, -32.7) * mm});
            skLineSegment(sketch, "E413", {"start": v(193.58, -116.54) * mm, "end": v(194.73, -116.54) * mm});
            skLineSegment(sketch, "E414", {"start": v(193.58, -117.64) * mm, "end": v(194.73, -117.64) * mm});
            skLineSegment(sketch, "E415", {"start": v(194.73, -115.44) * mm, "end": v(193.58, -115.44) * mm});
            skLineSegment(sketch, "E416", {"start": v(193.58, -117.64) * mm, "end": v(193.58, -116.54) * mm});
            skLineSegment(sketch, "E417", {"start": v(282.06, -116.37) * mm, "end": v(282.06, -115.27) * mm});
            skLineSegment(sketch, "E418", {"start": v(280.9, -116.37) * mm, "end": v(282.06, -116.37) * mm});
            skLineSegment(sketch, "E419", {"start": v(280.9, -117.47) * mm, "end": v(280.9, -116.37) * mm});
            skLineSegment(sketch, "E420", {"start": v(191.76, -121.84) * mm, "end": v(191.7, -122.23) * mm});
            skLineSegment(sketch, "E421", {"start": v(283.38, -26.75) * mm, "end": v(283.2, -26.32) * mm});
            skLineSegment(sketch, "E422", {"start": v(191.22, -27.17) * mm, "end": v(190.84, -27.46) * mm});
            skLineSegment(sketch, "E423", {"start": v(264.31, -33.17) * mm, "end": v(264.13, -33.6) * mm});
            skLineSegment(sketch, "E424", {"start": v(285.86, -123.37) * mm, "end": v(285.43, -123.55) * mm});
            skLineSegment(sketch, "E425", {"start": v(286.24, -123.08) * mm, "end": v(285.86, -123.37) * mm});
            skLineSegment(sketch, "E426", {"start": v(286.52, -122.7) * mm, "end": v(286.24, -123.08) * mm});
            skLineSegment(sketch, "E427", {"start": v(286.7, -122.28) * mm, "end": v(286.52, -122.7) * mm});
            skLineSegment(sketch, "E428", {"start": v(264.13, -33.6) * mm, "end": v(263.85, -33.98) * mm});
            skLineSegment(sketch, "E429", {"start": v(263.04, -34.45) * mm, "end": v(262.58, -34.5) * mm});
            skLineSegment(sketch, "E430", {"start": v(212.6, -114.42) * mm, "end": v(212.55, -113.95) * mm});
            skLineSegment(sketch, "E431", {"start": v(215.9, -113.05) * mm, "end": v(216.08, -113.49) * mm});
            skLineSegment(sketch, "E432", {"start": v(261.68, -31.15) * mm, "end": v(262.11, -30.97) * mm});
            skLineSegment(sketch, "E433", {"start": v(261.68, -34.27) * mm, "end": v(261.53, -34.13) * mm});
            skLineSegment(sketch, "E434", {"start": v(285.84, -27.41) * mm, "end": v(285.4, -27.6) * mm});
            skLineSegment(sketch, "E435", {"start": v(286.68, -26.32) * mm, "end": v(286.5, -26.75) * mm});
            skLineSegment(sketch, "E436", {"start": v(283.38, -24.95) * mm, "end": v(283.67, -24.58) * mm});
            skLineSegment(sketch, "E437", {"start": v(280.9, -117.47) * mm, "end": v(282.06, -117.47) * mm});
            skLineSegment(sketch, "E438", {"start": v(282.06, -115.27) * mm, "end": v(280.9, -115.27) * mm});
            skLineSegment(sketch, "E439", {"start": v(259.18, -38.2) * mm, "end": v(259.5, -38.2) * mm});
            skLineSegment(sketch, "E440", {"start": v(259.18, -38.2) * mm, "end": v(258.88, -38.2) * mm});
            skLineSegment(sketch, "E441", {"start": v(259.18, -36) * mm, "end": v(259.18, -38.2) * mm});
            skLineSegment(sketch, "E442", {"start": v(215.25, -112.4) * mm, "end": v(215.36, -112.48) * mm});
            skLineSegment(sketch, "E443", {"start": v(190.84, -27.46) * mm, "end": v(190.41, -27.64) * mm});
            skLineSegment(sketch, "E444", {"start": v(188.39, -26.8) * mm, "end": v(188.2, -26.36) * mm});
            skLineSegment(sketch, "E445", {"start": v(190.87, -120.2) * mm, "end": v(191.24, -120.5) * mm});
            skLineSegment(sketch, "E446", {"start": v(218.12, -110.06) * mm, "end": v(218.44, -110.06) * mm});
            skLineSegment(sketch, "E447", {"start": v(218.12, -107.86) * mm, "end": v(217.82, -108.17) * mm});
            skLineSegment(sketch, "E448", {"start": v(218.12, -110.06) * mm, "end": v(217.82, -110.06) * mm});
            skLineSegment(sketch, "E449", {"start": v(218.12, -107.86) * mm, "end": v(218.12, -110.06) * mm});
            skLineSegment(sketch, "E450", {"start": v(259.04, -108.12) * mm, "end": v(258.74, -108.43) * mm});
            skLineSegment(sketch, "E451", {"start": v(263.04, -30.97) * mm, "end": v(263.48, -31.15) * mm});
            skLineSegment(sketch, "E452", {"start": v(283.4, -122.7) * mm, "end": v(283.22, -122.28) * mm});
            skLineSegment(sketch, "E453", {"start": v(284.5, -120.07) * mm, "end": v(284.9, -120.02) * mm});
            skLineSegment(sketch, "E454", {"start": v(212.57, -39.47) * mm, "end": v(212.51, -39) * mm});
            skLineSegment(sketch, "E455", {"start": v(261.7, -112.47) * mm, "end": v(262.14, -112.29) * mm});
            skLineSegment(sketch, "E456", {"start": v(260.87, -114.5) * mm, "end": v(260.8, -114.02) * mm});
            skLineSegment(sketch, "E457", {"start": v(213.07, -112.68) * mm, "end": v(213.45, -112.4) * mm});
            skLineSegment(sketch, "E458", {"start": v(214.31, -40.8) * mm, "end": v(213.85, -40.75) * mm});
            skLineSegment(sketch, "E459", {"start": v(213.85, -40.75) * mm, "end": v(213.46, -40.59) * mm});
            skLineSegment(sketch, "E460", {"start": v(264.32, -32.24) * mm, "end": v(264.38, -32.7) * mm});
            skLineSegment(sketch, "E461", {"start": v(262.14, -115.76) * mm, "end": v(261.96, -115.67) * mm});
            skLineSegment(sketch, "E462", {"start": v(261.7, -115.58) * mm, "end": v(261.33, -115.3) * mm});
            skLineSegment(sketch, "E463", {"start": v(261.33, -115.3) * mm, "end": v(261.05, -114.92) * mm});
            skLineSegment(sketch, "E464", {"start": v(190.85, -24.34) * mm, "end": v(191.22, -24.63) * mm});
            skLineSegment(sketch, "E465", {"start": v(191.22, -24.63) * mm, "end": v(191.5, -25) * mm});
            skLineSegment(sketch, "E466", {"start": v(213.41, -40.57) * mm, "end": v(213.3, -40.47) * mm});
            skLineSegment(sketch, "E467", {"start": v(213.04, -40.28) * mm, "end": v(212.75, -39.9) * mm});
            skLineSegment(sketch, "E468", {"start": v(212.75, -39.9) * mm, "end": v(212.57, -39.47) * mm});
            skLineSegment(sketch, "E469", {"start": v(190.87, -123.33) * mm, "end": v(190.44, -123.5) * mm});
            skLineSegment(sketch, "E470", {"start": v(190.44, -123.5) * mm, "end": v(189.97, -123.57) * mm});
            skLineSegment(sketch, "E471", {"start": v(189.97, -123.57) * mm, "end": v(189.5, -123.5) * mm});
            skLineSegment(sketch, "E472", {"start": v(284.06, -120.25) * mm, "end": v(284.5, -120.07) * mm});
            skLineSegment(sketch, "E473", {"start": v(188.17, -121.77) * mm, "end": v(188.23, -121.3) * mm});
            skLineSegment(sketch, "E474", {"start": v(189.5, -123.5) * mm, "end": v(189.07, -123.32) * mm});
            skLineSegment(sketch, "E475", {"start": v(189.9, -119.98) * mm, "end": v(189.97, -119.97) * mm});
            skLineSegment(sketch, "E476", {"start": v(284.96, -123.6) * mm, "end": v(284.5, -123.55) * mm});
            skLineSegment(sketch, "E477", {"start": v(188.15, -25.9) * mm, "end": v(188.2, -25.43) * mm});
            skLineSegment(sketch, "E478", {"start": v(285.43, -123.55) * mm, "end": v(284.96, -123.6) * mm});
            skLineSegment(sketch, "E479", {"start": v(188.7, -120.5) * mm, "end": v(189.07, -120.2) * mm});
            skLineSegment(sketch, "E480", {"start": v(188.41, -120.87) * mm, "end": v(188.7, -120.5) * mm});
            skLineSegment(sketch, "E481", {"start": v(188.23, -121.3) * mm, "end": v(188.41, -120.87) * mm});
            skLineSegment(sketch, "E482", {"start": v(213.88, -112.21) * mm, "end": v(214.35, -112.15) * mm});
            skLineSegment(sketch, "E483", {"start": v(214.35, -112.15) * mm, "end": v(214.81, -112.21) * mm});
            skLineSegment(sketch, "E484", {"start": v(213.45, -112.4) * mm, "end": v(213.88, -112.21) * mm});
            skLineSegment(sketch, "E485", {"start": v(212.79, -113.05) * mm, "end": v(213.07, -112.68) * mm});
            skLineSegment(sketch, "E486", {"start": v(284.47, -24.11) * mm, "end": v(284.94, -24.05) * mm});
            skLineSegment(sketch, "E487", {"start": v(215.87, -38.1) * mm, "end": v(216.05, -38.54) * mm});
            skLineSegment(sketch, "E488", {"start": v(216.05, -39.48) * mm, "end": v(215.87, -39.9) * mm});
            skLineSegment(sketch, "E489", {"start": v(214.81, -115.7) * mm, "end": v(214.35, -115.75) * mm});
            skLineSegment(sketch, "E490", {"start": v(214.35, -115.75) * mm, "end": v(213.88, -115.7) * mm});
            skLineSegment(sketch, "E491", {"start": v(212.57, -38.54) * mm, "end": v(212.75, -38.1) * mm});
            skLineSegment(sketch, "E492", {"start": v(212.51, -39) * mm, "end": v(212.57, -38.54) * mm});
            skLineSegment(sketch, "E493", {"start": v(280.79, -32.1) * mm, "end": v(280.79, -31) * mm});
            skLineSegment(sketch, "E494", {"start": v(280.79, -31) * mm, "end": v(281.94, -31) * mm});
            skLineSegment(sketch, "E495", {"start": v(281.94, -29.9) * mm, "end": v(280.79, -29.9) * mm});
            skLineSegment(sketch, "E496", {"start": v(280.79, -32.1) * mm, "end": v(281.94, -32.1) * mm});
            skLineSegment(sketch, "E497", {"start": v(194.73, -116.54) * mm, "end": v(194.73, -115.44) * mm});
            skLineSegment(sketch, "E498", {"start": v(189.05, -24.34) * mm, "end": v(189.48, -24.16) * mm});
            skLineSegment(sketch, "E499", {"start": v(262.6, -112.22) * mm, "end": v(263.07, -112.29) * mm});
            skLineSegment(sketch, "E500", {"start": v(263.07, -112.29) * mm, "end": v(263.27, -112.37) * mm});
            skLineSegment(sketch, "E501", {"start": v(263.5, -112.47) * mm, "end": v(263.88, -112.75) * mm});
            skLineSegment(sketch, "E502", {"start": v(263.88, -112.75) * mm, "end": v(264.17, -113.13) * mm});
            skLineSegment(sketch, "E503", {"start": v(264.38, -32.7) * mm, "end": v(264.31, -33.17) * mm});
            skLineSegment(sketch, "E504", {"start": v(264.34, -114.5) * mm, "end": v(264.16, -114.93) * mm});
            skLineSegment(sketch, "E505", {"start": v(264.16, -114.93) * mm, "end": v(263.88, -115.3) * mm});
            skLineSegment(sketch, "E506", {"start": v(263.88, -115.3) * mm, "end": v(263.5, -115.58) * mm});
            skLineSegment(sketch, "E507", {"start": v(262.14, -112.29) * mm, "end": v(262.6, -112.22) * mm});
            skLineSegment(sketch, "E508", {"start": v(263.85, -33.98) * mm, "end": v(263.48, -34.27) * mm});
            skLineSegment(sketch, "E509", {"start": v(212.6, -113.49) * mm, "end": v(212.79, -113.05) * mm});
            skLineSegment(sketch, "E510", {"start": v(212.55, -113.95) * mm, "end": v(212.6, -113.49) * mm});
            skLineSegment(sketch, "E511", {"start": v(262.58, -30.9) * mm, "end": v(263.04, -30.97) * mm});
            skLineSegment(sketch, "E512", {"start": v(283.14, -25.85) * mm, "end": v(283.2, -25.39) * mm});
            skLineSegment(sketch, "E513", {"start": v(285.84, -24.3) * mm, "end": v(286.21, -24.58) * mm});
            skLineSegment(sketch, "E514", {"start": v(284.04, -24.3) * mm, "end": v(284.47, -24.11) * mm});
            skLineSegment(sketch, "E515", {"start": v(284.9, -120.02) * mm, "end": v(284.96, -120) * mm});
            skLineSegment(sketch, "E516", {"start": v(188.67, -27.17) * mm, "end": v(188.39, -26.8) * mm});
            skLineSegment(sketch, "E517", {"start": v(188.7, -123.04) * mm, "end": v(188.41, -122.67) * mm});
            skLineSegment(sketch, "E518", {"start": v(263.5, -115.58) * mm, "end": v(263.07, -115.76) * mm});
            skLineSegment(sketch, "E519", {"start": v(263.07, -115.76) * mm, "end": v(262.6, -115.82) * mm});
            skLineSegment(sketch, "E520", {"start": v(262.6, -115.82) * mm, "end": v(262.2, -115.77) * mm});
            skLineSegment(sketch, "E521", {"start": v(215.62, -115.23) * mm, "end": v(215.25, -115.51) * mm});
            skLineSegment(sketch, "E522", {"start": v(215.25, -115.51) * mm, "end": v(214.81, -115.7) * mm});
            skLineSegment(sketch, "E523", {"start": v(191.5, -26.8) * mm, "end": v(191.22, -27.17) * mm});
            skLineSegment(sketch, "E524", {"start": v(284.9, -27.65) * mm, "end": v(284.47, -27.6) * mm});
            skLineSegment(sketch, "E525", {"start": v(189.48, -27.64) * mm, "end": v(189.04, -27.46) * mm});
            skLineSegment(sketch, "E526", {"start": v(285.86, -120.25) * mm, "end": v(286.24, -120.54) * mm});
            skLineSegment(sketch, "E527", {"start": v(285.4, -24.11) * mm, "end": v(285.84, -24.3) * mm});
            skLineSegment(sketch, "E528", {"start": v(286.5, -24.95) * mm, "end": v(286.68, -25.39) * mm});
            skLineSegment(sketch, "E529", {"start": v(191.7, -122.23) * mm, "end": v(191.53, -122.67) * mm});
            skLineSegment(sketch, "E530", {"start": v(191.77, -121.77) * mm, "end": v(191.76, -121.84) * mm});
            skLineSegment(sketch, "E531", {"start": v(213.88, -115.7) * mm, "end": v(213.52, -115.54) * mm});
            skLineSegment(sketch, "E532", {"start": v(213.45, -115.51) * mm, "end": v(213.26, -115.34) * mm});
            skLineSegment(sketch, "E533", {"start": v(214.31, -37.2) * mm, "end": v(214.78, -37.27) * mm});
            skLineSegment(sketch, "E534", {"start": v(214.78, -37.27) * mm, "end": v(215.21, -37.45) * mm});
            skLineSegment(sketch, "E535", {"start": v(215.21, -37.45) * mm, "end": v(215.43, -37.62) * mm});
            skLineSegment(sketch, "E536", {"start": v(284.94, -24.05) * mm, "end": v(285.4, -24.11) * mm});
            skLineSegment(sketch, "E537", {"start": v(283.2, -26.32) * mm, "end": v(283.14, -25.85) * mm});
            skLineSegment(sketch, "E538", {"start": v(283.67, -24.58) * mm, "end": v(284.04, -24.3) * mm});
            skLineSegment(sketch, "E539", {"start": v(216.08, -113.49) * mm, "end": v(216.15, -113.95) * mm});
            skLineSegment(sketch, "E540", {"start": v(216.15, -113.95) * mm, "end": v(216.08, -114.42) * mm});
            skLineSegment(sketch, "E541", {"start": v(192.63, -29.61) * mm, "end": v(191.48, -29.61) * mm});
            skLineSegment(sketch, "E542", {"start": v(191.48, -30.71) * mm, "end": v(192.63, -30.71) * mm});
            skLineSegment(sketch, "E543", {"start": v(192.63, -30.71) * mm, "end": v(192.63, -29.61) * mm});
            skLineSegment(sketch, "E544", {"start": v(281.94, -31) * mm, "end": v(281.94, -29.9) * mm});
            skLineSegment(sketch, "E545", {"start": v(260.8, -114.02) * mm, "end": v(260.87, -113.56) * mm});
            skLineSegment(sketch, "E546", {"start": v(260.87, -113.56) * mm, "end": v(261.05, -113.12) * mm});
            skLineSegment(sketch, "E547", {"start": v(261.05, -113.12) * mm, "end": v(261.33, -112.75) * mm});
            skLineSegment(sketch, "E548", {"start": v(261.33, -112.75) * mm, "end": v(261.7, -112.47) * mm});
            skLineSegment(sketch, "E549", {"start": v(191.7, -121.3) * mm, "end": v(191.77, -121.77) * mm});
            skLineSegment(sketch, "E550", {"start": v(191.53, -120.87) * mm, "end": v(191.7, -121.3) * mm});
            skLineSegment(sketch, "E551", {"start": v(191.24, -120.5) * mm, "end": v(191.53, -120.87) * mm});
            skLineSegment(sketch, "E552", {"start": v(283.69, -123.08) * mm, "end": v(283.4, -122.7) * mm});
            skLineSegment(sketch, "E553", {"start": v(188.67, -24.63) * mm, "end": v(189.05, -24.34) * mm});
            skLineSegment(sketch, "E554", {"start": v(191.5, -25) * mm, "end": v(191.68, -25.43) * mm});
            skLineSegment(sketch, "E555", {"start": v(191.68, -25.43) * mm, "end": v(191.74, -25.84) * mm});
            skLineSegment(sketch, "E556", {"start": v(191.74, -25.84) * mm, "end": v(191.75, -25.9) * mm});
            skLineSegment(sketch, "E557", {"start": v(286.21, -24.58) * mm, "end": v(286.5, -24.95) * mm});
            skLineSegment(sketch, "E558", {"start": v(286.21, -27.13) * mm, "end": v(285.84, -27.41) * mm});
            skLineSegment(sketch, "E559", {"start": v(286.5, -26.75) * mm, "end": v(286.21, -27.13) * mm});
            skLineSegment(sketch, "E560", {"start": v(215.21, -40.57) * mm, "end": v(214.78, -40.75) * mm});
            skLineSegment(sketch, "E561", {"start": v(215.59, -37.74) * mm, "end": v(215.87, -38.1) * mm});
            skLineSegment(sketch, "E562", {"start": v(260.84, -32.24) * mm, "end": v(261.02, -31.8) * mm});
            skLineSegment(sketch, "E563", {"start": v(260.78, -32.7) * mm, "end": v(260.84, -32.24) * mm});
            skLineSegment(sketch, "E564", {"start": v(261.05, -114.92) * mm, "end": v(260.87, -114.5) * mm});
            skLineSegment(sketch, "E565", {"start": v(264.17, -113.13) * mm, "end": v(264.34, -113.56) * mm});
            skLineSegment(sketch, "E566", {"start": v(264.34, -113.56) * mm, "end": v(264.4, -114.03) * mm});
            skLineSegment(sketch, "E567", {"start": v(264.4, -114.03) * mm, "end": v(264.34, -114.5) * mm});
            skLineSegment(sketch, "E568", {"start": v(263.85, -31.44) * mm, "end": v(264.14, -31.8) * mm});
            skLineSegment(sketch, "E569", {"start": v(261.3, -33.98) * mm, "end": v(261.02, -33.6) * mm});
            skLineSegment(sketch, "E570", {"start": v(262.58, -34.5) * mm, "end": v(262.11, -34.45) * mm});
            skLineSegment(sketch, "E571", {"start": v(216.11, -39) * mm, "end": v(216.05, -39.48) * mm});
            skLineSegment(sketch, "E572", {"start": v(215.59, -40.28) * mm, "end": v(215.21, -40.57) * mm});
            skLineSegment(sketch, "E573", {"start": v(283.67, -27.13) * mm, "end": v(283.38, -26.75) * mm});
            skLineSegment(sketch, "E574", {"start": v(284.94, -27.65) * mm, "end": v(284.9, -27.65) * mm});
            skLineSegment(sketch, "E575", {"start": v(284.47, -27.6) * mm, "end": v(284.04, -27.41) * mm});
            skLineSegment(sketch, "E576", {"start": v(286.68, -25.39) * mm, "end": v(286.74, -25.85) * mm});
            skLineSegment(sketch, "E577", {"start": v(214.81, -112.21) * mm, "end": v(215.25, -112.4) * mm});
            skLineSegment(sketch, "E578", {"start": v(215.62, -112.68) * mm, "end": v(215.9, -113.05) * mm});
            skLineSegment(sketch, "E579", {"start": v(263.62, -31.26) * mm, "end": v(263.7, -31.3) * mm});
            skLineSegment(sketch, "E580", {"start": v(261.75, -34.3) * mm, "end": v(261.68, -34.27) * mm});
            skLineSegment(sketch, "E581", {"start": v(261.53, -34.13) * mm, "end": v(261.3, -33.98) * mm});
            skLineSegment(sketch, "E582", {"start": v(215.43, -112.51) * mm, "end": v(215.62, -112.68) * mm});
            skLineSegment(sketch, "E583", {"start": v(215.36, -112.48) * mm, "end": v(215.43, -112.51) * mm});
            skLineSegment(sketch, "E584", {"start": v(213.46, -40.59) * mm, "end": v(213.41, -40.57) * mm});
            skLineSegment(sketch, "E585", {"start": v(261.96, -115.67) * mm, "end": v(261.7, -115.58) * mm});
            skLineSegment(sketch, "E586", {"start": v(213.3, -40.47) * mm, "end": v(213.04, -40.28) * mm});
            skLineSegment(sketch, "E587", {"start": v(263.33, -112.38) * mm, "end": v(263.5, -112.47) * mm});
            skLineSegment(sketch, "E588", {"start": v(263.27, -112.37) * mm, "end": v(263.33, -112.38) * mm});
            skLineSegment(sketch, "E589", {"start": v(262.2, -115.77) * mm, "end": v(262.14, -115.76) * mm});
            skLineSegment(sketch, "E590", {"start": v(213.52, -115.54) * mm, "end": v(213.45, -115.51) * mm});
            skLineSegment(sketch, "E591", {"start": v(213.26, -115.34) * mm, "end": v(213.07, -115.23) * mm});
            skLineSegment(sketch, "E592", {"start": v(215.48, -37.63) * mm, "end": v(215.59, -37.74) * mm});
            skLineSegment(sketch, "E593", {"start": v(215.43, -37.62) * mm, "end": v(215.48, -37.63) * mm});
            skLineSegment(sketch, "E594", {"start": v(263.7, -31.3) * mm, "end": v(263.85, -31.44) * mm});
            skLineSegment(sketch, "E595", {"start": v(-142.74, 154.97) * mm, "end": v(-146.26, 154.97) * mm});
            skLineSegment(sketch, "E596", {"start": v(-146.26, 154.97) * mm, "end": v(-146.26, 166.26) * mm});
            skLineSegment(sketch, "E597", {"start": v(-146.26, 166.26) * mm, "end": v(-142.74, 166.26) * mm});
            skLineSegment(sketch, "E598", {"start": v(-142.74, 166.26) * mm, "end": v(-142.74, 154.97) * mm});
            skLineSegment(sketch, "E599", {"start": v(-142.63, 167.87) * mm, "end": v(-146.36, 167.87) * mm});
            skLineSegment(sketch, "E600", {"start": v(-146.36, 167.87) * mm, "end": v(-146.36, 170.62) * mm});
            skLineSegment(sketch, "E601", {"start": v(-146.36, 170.62) * mm, "end": v(-142.63, 170.62) * mm});
            skLineSegment(sketch, "E602", {"start": v(-142.63, 170.62) * mm, "end": v(-142.63, 167.87) * mm});
            skLineSegment(sketch, "E603", {"start": v(-129.24, 159.82) * mm, "end": v(-129.34, 158.77) * mm});
            skLineSegment(sketch, "E604", {"start": v(-129.34, 158.77) * mm, "end": v(-129.64, 157.81) * mm});
            skLineSegment(sketch, "E605", {"start": v(-129.64, 157.81) * mm, "end": v(-130.15, 156.98) * mm});
            skLineSegment(sketch, "E606", {"start": v(-130.15, 156.98) * mm, "end": v(-130.84, 156.28) * mm});
            skLineSegment(sketch, "E607", {"start": v(-130.84, 156.28) * mm, "end": v(-131.7, 155.72) * mm});
            skLineSegment(sketch, "E608", {"start": v(-131.7, 155.72) * mm, "end": v(-132.7, 155.3) * mm});
            skLineSegment(sketch, "E609", {"start": v(-132.7, 155.3) * mm, "end": v(-133.9, 155.05) * mm});
            skLineSegment(sketch, "E610", {"start": v(-133.9, 155.05) * mm, "end": v(-135.31, 154.97) * mm});
            skLineSegment(sketch, "E611", {"start": v(-135.31, 154.97) * mm, "end": v(-136.94, 155.04) * mm});
            skLineSegment(sketch, "E612", {"start": v(-136.94, 155.04) * mm, "end": v(-138.31, 155.26) * mm});
            skLineSegment(sketch, "E613", {"start": v(-138.31, 155.26) * mm, "end": v(-140.35, 155.91) * mm});
            skLineSegment(sketch, "E614", {"start": v(-140.35, 155.91) * mm, "end": v(-140.35, 159.16) * mm});
            skLineSegment(sketch, "E615", {"start": v(-140.35, 159.16) * mm, "end": v(-139.99, 159.16) * mm});
            skLineSegment(sketch, "E616", {"start": v(-139.99, 159.16) * mm, "end": v(-139.1, 158.67) * mm});
            skLineSegment(sketch, "E617", {"start": v(-139.1, 158.67) * mm, "end": v(-138.05, 158.26) * mm});
            skLineSegment(sketch, "E618", {"start": v(-138.05, 158.26) * mm, "end": v(-137, 157.97) * mm});
            skLineSegment(sketch, "E619", {"start": v(-137, 157.97) * mm, "end": v(-136.03, 157.87) * mm});
            skLineSegment(sketch, "E620", {"start": v(-136.03, 157.87) * mm, "end": v(-134.84, 157.97) * mm});
            skLineSegment(sketch, "E621", {"start": v(-134.84, 157.97) * mm, "end": v(-134.26, 158.12) * mm});
            skLineSegment(sketch, "E622", {"start": v(-134.26, 158.12) * mm, "end": v(-133.77, 158.39) * mm});
            skLineSegment(sketch, "E623", {"start": v(-133.77, 158.39) * mm, "end": v(-133.23, 159) * mm});
            skLineSegment(sketch, "E624", {"start": v(-133.23, 159) * mm, "end": v(-133.07, 159.45) * mm});
            skLineSegment(sketch, "E625", {"start": v(-133.07, 159.45) * mm, "end": v(-133.02, 160.05) * mm});
            skLineSegment(sketch, "E626", {"start": v(-133.02, 160.05) * mm, "end": v(-133.1, 160.63) * mm});
            skLineSegment(sketch, "E627", {"start": v(-133.1, 160.63) * mm, "end": v(-133.31, 161.07) * mm});
            skLineSegment(sketch, "E628", {"start": v(-133.31, 161.07) * mm, "end": v(-133.65, 161.38) * mm});
            skLineSegment(sketch, "E629", {"start": v(-133.65, 161.38) * mm, "end": v(-134.09, 161.59) * mm});
            skLineSegment(sketch, "E630", {"start": v(-134.09, 161.59) * mm, "end": v(-135.24, 161.78) * mm});
            skLineSegment(sketch, "E631", {"start": v(-135.24, 161.78) * mm, "end": v(-136.43, 161.8) * mm});
            skLineSegment(sketch, "E632", {"start": v(-136.43, 161.8) * mm, "end": v(-137.07, 161.8) * mm});
            skLineSegment(sketch, "E633", {"start": v(-137.07, 161.8) * mm, "end": v(-137.07, 164.43) * mm});
            skLineSegment(sketch, "E634", {"start": v(-137.07, 164.43) * mm, "end": v(-136.48, 164.43) * mm});
            skLineSegment(sketch, "E635", {"start": v(-136.48, 164.43) * mm, "end": v(-135.22, 164.5) * mm});
            skLineSegment(sketch, "E636", {"start": v(-135.22, 164.5) * mm, "end": v(-134.25, 164.73) * mm});
            skLineSegment(sketch, "E637", {"start": v(-134.25, 164.73) * mm, "end": v(-133.62, 165.27) * mm});
            skLineSegment(sketch, "E638", {"start": v(-133.62, 165.27) * mm, "end": v(-133.45, 165.67) * mm});
            skLineSegment(sketch, "E639", {"start": v(-133.45, 165.67) * mm, "end": v(-133.4, 166.2) * mm});
            skLineSegment(sketch, "E640", {"start": v(-133.4, 166.2) * mm, "end": v(-133.44, 166.6) * mm});
            skLineSegment(sketch, "E641", {"start": v(-133.44, 166.6) * mm, "end": v(-133.6, 166.93) * mm});
            skLineSegment(sketch, "E642", {"start": v(-133.6, 166.93) * mm, "end": v(-134.13, 167.38) * mm});
            skLineSegment(sketch, "E643", {"start": v(-134.13, 167.38) * mm, "end": v(-134.97, 167.62) * mm});
            skLineSegment(sketch, "E644", {"start": v(-134.97, 167.62) * mm, "end": v(-135.8, 167.68) * mm});
            skLineSegment(sketch, "E645", {"start": v(-135.8, 167.68) * mm, "end": v(-136.92, 167.55) * mm});
            skLineSegment(sketch, "E646", {"start": v(-136.92, 167.55) * mm, "end": v(-138.04, 167.22) * mm});
            skLineSegment(sketch, "E647", {"start": v(-138.04, 167.22) * mm, "end": v(-138.92, 166.8) * mm});
            skLineSegment(sketch, "E648", {"start": v(-138.92, 166.8) * mm, "end": v(-139.6, 166.41) * mm});
            skLineSegment(sketch, "E649", {"start": v(-139.6, 166.41) * mm, "end": v(-139.92, 166.41) * mm});
            skLineSegment(sketch, "E650", {"start": v(-139.92, 166.41) * mm, "end": v(-139.92, 169.62) * mm});
            skLineSegment(sketch, "E651", {"start": v(-139.92, 169.62) * mm, "end": v(-137.83, 170.26) * mm});
            skLineSegment(sketch, "E652", {"start": v(-137.83, 170.26) * mm, "end": v(-136.5, 170.5) * mm});
            skLineSegment(sketch, "E653", {"start": v(-136.5, 170.5) * mm, "end": v(-135.15, 170.57) * mm});
            skLineSegment(sketch, "E654", {"start": v(-135.15, 170.57) * mm, "end": v(-133.9, 170.51) * mm});
            skLineSegment(sketch, "E655", {"start": v(-133.9, 170.51) * mm, "end": v(-132.83, 170.34) * mm});
            skLineSegment(sketch, "E656", {"start": v(-132.83, 170.34) * mm, "end": v(-131.92, 170.05) * mm});
            skLineSegment(sketch, "E657", {"start": v(-131.92, 170.05) * mm, "end": v(-131.16, 169.66) * mm});
            skLineSegment(sketch, "E658", {"start": v(-131.16, 169.66) * mm, "end": v(-130.49, 169.13) * mm});
            skLineSegment(sketch, "E659", {"start": v(-130.49, 169.13) * mm, "end": v(-130.01, 168.46) * mm});
            skLineSegment(sketch, "E660", {"start": v(-130.01, 168.46) * mm, "end": v(-129.73, 167.69) * mm});
            skLineSegment(sketch, "E661", {"start": v(-129.73, 167.69) * mm, "end": v(-129.63, 166.82) * mm});
            skLineSegment(sketch, "E662", {"start": v(-129.63, 166.82) * mm, "end": v(-129.81, 165.62) * mm});
            skLineSegment(sketch, "E663", {"start": v(-129.81, 165.62) * mm, "end": v(-130.37, 164.58) * mm});
            skLineSegment(sketch, "E664", {"start": v(-130.37, 164.58) * mm, "end": v(-131.23, 163.79) * mm});
            skLineSegment(sketch, "E665", {"start": v(-131.23, 163.79) * mm, "end": v(-132.32, 163.34) * mm});
            skLineSegment(sketch, "E666", {"start": v(-132.32, 163.34) * mm, "end": v(-132.32, 163.2) * mm});
            skLineSegment(sketch, "E667", {"start": v(-132.32, 163.2) * mm, "end": v(-131.27, 162.92) * mm});
            skLineSegment(sketch, "E668", {"start": v(-131.27, 162.92) * mm, "end": v(-130.28, 162.3) * mm});
            skLineSegment(sketch, "E669", {"start": v(-130.28, 162.3) * mm, "end": v(-129.87, 161.85) * mm});
            skLineSegment(sketch, "E670", {"start": v(-129.87, 161.85) * mm, "end": v(-129.53, 161.29) * mm});
            skLineSegment(sketch, "E671", {"start": v(-129.53, 161.29) * mm, "end": v(-129.31, 160.61) * mm});
            skLineSegment(sketch, "E672", {"start": v(-129.31, 160.61) * mm, "end": v(-129.24, 159.82) * mm});
            skLineSegment(sketch, "E673", {"start": v(216.99, -42.2) * mm, "end": v(216.99, -44.4) * mm});
            skLineSegment(sketch, "E674", {"start": v(214.86, -27.58) * mm, "end": v(214.8, -27.12) * mm});
            skLineSegment(sketch, "E675", {"start": v(215.7, -25.56) * mm, "end": v(216.14, -25.38) * mm});
            skLineSegment(sketch, "E676", {"start": v(215.33, -28.4) * mm, "end": v(215.04, -28.02) * mm});
            skLineSegment(sketch, "E677", {"start": v(218.16, -28.02) * mm, "end": v(217.87, -28.4) * mm});
            skLineSegment(sketch, "E678", {"start": v(216.13, -28.86) * mm, "end": v(215.7, -28.68) * mm});
            skLineSegment(sketch, "E679", {"start": v(215.33, -25.85) * mm, "end": v(215.7, -25.56) * mm});
            skLineSegment(sketch, "E680", {"start": v(217.07, -28.86) * mm, "end": v(216.6, -28.92) * mm});
            skLineSegment(sketch, "E681", {"start": v(216.6, -28.92) * mm, "end": v(216.55, -28.91) * mm});
            skLineSegment(sketch, "E682", {"start": v(218.4, -27.12) * mm, "end": v(218.34, -27.58) * mm});
            skLineSegment(sketch, "E683", {"start": v(214.86, -26.65) * mm, "end": v(215.04, -26.22) * mm});
            skLineSegment(sketch, "E684", {"start": v(217.87, -28.4) * mm, "end": v(217.5, -28.68) * mm});
            skLineSegment(sketch, "E685", {"start": v(218.16, -26.22) * mm, "end": v(218.34, -26.65) * mm});
            skLineSegment(sketch, "E686", {"start": v(218.34, -26.65) * mm, "end": v(218.4, -27.06) * mm});
            skLineSegment(sketch, "E687", {"start": v(218.4, -27.06) * mm, "end": v(218.4, -27.12) * mm});
            skLineSegment(sketch, "E688", {"start": v(217.5, -28.68) * mm, "end": v(217.07, -28.86) * mm});
            skLineSegment(sketch, "E689", {"start": v(215.04, -28.02) * mm, "end": v(214.86, -27.58) * mm});
            skLineSegment(sketch, "E690", {"start": v(217.5, -25.56) * mm, "end": v(217.87, -25.85) * mm});
            skLineSegment(sketch, "E691", {"start": v(217.87, -25.85) * mm, "end": v(218.16, -26.22) * mm});
            skLineSegment(sketch, "E692", {"start": v(214.8, -27.12) * mm, "end": v(214.86, -26.65) * mm});
            skLineSegment(sketch, "E693", {"start": v(216.55, -28.91) * mm, "end": v(216.13, -28.86) * mm});
            skLineSegment(sketch, "E694", {"start": v(216.14, -25.38) * mm, "end": v(216.6, -25.32) * mm});
            skLineSegment(sketch, "E695", {"start": v(215.7, -28.68) * mm, "end": v(215.33, -28.4) * mm});
            skLineSegment(sketch, "E696", {"start": v(217.07, -25.38) * mm, "end": v(217.5, -25.56) * mm});
            skLineSegment(sketch, "E697", {"start": v(216.6, -25.32) * mm, "end": v(217.07, -25.38) * mm});
            skLineSegment(sketch, "E698", {"start": v(215.04, -26.22) * mm, "end": v(215.33, -25.85) * mm});
            skLineSegment(sketch, "E699", {"start": v(218.34, -27.58) * mm, "end": v(218.16, -28.02) * mm});
            skLineSegment(sketch, "E700", {"start": v(260.38, -28.82) * mm, "end": v(259.97, -28.76) * mm});
            skLineSegment(sketch, "E701", {"start": v(258.64, -27.03) * mm, "end": v(258.7, -26.56) * mm});
            skLineSegment(sketch, "E702", {"start": v(259.54, -25.47) * mm, "end": v(259.97, -25.29) * mm});
            skLineSegment(sketch, "E703", {"start": v(259.16, -28.3) * mm, "end": v(258.88, -27.93) * mm});
            skLineSegment(sketch, "E704", {"start": v(262, -27.93) * mm, "end": v(261.7, -28.3) * mm});
            skLineSegment(sketch, "E705", {"start": v(259.97, -28.76) * mm, "end": v(259.53, -28.58) * mm});
            skLineSegment(sketch, "E706", {"start": v(259.16, -25.75) * mm, "end": v(259.54, -25.47) * mm});
            skLineSegment(sketch, "E707", {"start": v(261.7, -28.3) * mm, "end": v(261.33, -28.58) * mm});
            skLineSegment(sketch, "E708", {"start": v(258.7, -26.56) * mm, "end": v(258.88, -26.13) * mm});
            skLineSegment(sketch, "E709", {"start": v(261.33, -28.58) * mm, "end": v(260.9, -28.76) * mm});
            skLineSegment(sketch, "E710", {"start": v(258.88, -27.93) * mm, "end": v(258.7, -27.5) * mm});
            skLineSegment(sketch, "E711", {"start": v(261.34, -25.47) * mm, "end": v(261.7, -25.75) * mm});
            skLineSegment(sketch, "E712", {"start": v(261.7, -25.75) * mm, "end": v(262, -26.13) * mm});
            skLineSegment(sketch, "E713", {"start": v(262.24, -27.03) * mm, "end": v(262.17, -27.5) * mm});
            skLineSegment(sketch, "E714", {"start": v(260.43, -28.83) * mm, "end": v(260.38, -28.82) * mm});
            skLineSegment(sketch, "E715", {"start": v(260.9, -28.76) * mm, "end": v(260.54, -28.81) * mm});
            skLineSegment(sketch, "E716", {"start": v(260.44, -25.23) * mm, "end": v(260.9, -25.29) * mm});
            skLineSegment(sketch, "E717", {"start": v(260.9, -25.29) * mm, "end": v(261.34, -25.47) * mm});
            skLineSegment(sketch, "E718", {"start": v(258.88, -26.13) * mm, "end": v(259.16, -25.75) * mm});
            skLineSegment(sketch, "E719", {"start": v(262.17, -27.5) * mm, "end": v(262, -27.93) * mm});
            skLineSegment(sketch, "E720", {"start": v(258.7, -27.5) * mm, "end": v(258.64, -27.08) * mm});
            skLineSegment(sketch, "E721", {"start": v(259.97, -25.29) * mm, "end": v(260.44, -25.23) * mm});
            skLineSegment(sketch, "E722", {"start": v(262, -26.13) * mm, "end": v(262.17, -26.56) * mm});
            skLineSegment(sketch, "E723", {"start": v(262.17, -26.56) * mm, "end": v(262.23, -26.97) * mm});
            skLineSegment(sketch, "E724", {"start": v(262.23, -26.97) * mm, "end": v(262.24, -27.03) * mm});
            skLineSegment(sketch, "E725", {"start": v(259.53, -28.58) * mm, "end": v(259.16, -28.3) * mm});
            skLineSegment(sketch, "E726", {"start": v(260.54, -28.81) * mm, "end": v(260.43, -28.83) * mm});
            skLineSegment(sketch, "E727", {"start": v(258.64, -27.08) * mm, "end": v(258.64, -27.03) * mm});
            skLineSegment(sketch, "E728", {"start": v(215.63, -122.6) * mm, "end": v(215.26, -122.32) * mm});
            skLineSegment(sketch, "E729", {"start": v(214.98, -120.14) * mm, "end": v(215.26, -119.77) * mm});
            skLineSegment(sketch, "E730", {"start": v(218.27, -120.58) * mm, "end": v(218.33, -120.99) * mm});
            skLineSegment(sketch, "E731", {"start": v(218.33, -120.99) * mm, "end": v(218.34, -121.04) * mm});
            skLineSegment(sketch, "E732", {"start": v(217, -119.3) * mm, "end": v(217.44, -119.48) * mm});
            skLineSegment(sketch, "E733", {"start": v(214.74, -121.04) * mm, "end": v(214.8, -120.58) * mm});
            skLineSegment(sketch, "E734", {"start": v(215.64, -119.48) * mm, "end": v(216.07, -119.3) * mm});
            skLineSegment(sketch, "E735", {"start": v(215.26, -122.32) * mm, "end": v(214.98, -121.94) * mm});
            skLineSegment(sketch, "E736", {"start": v(218.1, -121.94) * mm, "end": v(217.8, -122.32) * mm});
            skLineSegment(sketch, "E737", {"start": v(216.07, -122.78) * mm, "end": v(215.63, -122.6) * mm});
            skLineSegment(sketch, "E738", {"start": v(215.26, -119.77) * mm, "end": v(215.64, -119.48) * mm});
            skLineSegment(sketch, "E739", {"start": v(218.1, -120.14) * mm, "end": v(218.27, -120.58) * mm});
            skLineSegment(sketch, "E740", {"start": v(214.8, -121.5) * mm, "end": v(214.74, -121.04) * mm});
            skLineSegment(sketch, "E741", {"start": v(214.8, -120.58) * mm, "end": v(214.98, -120.14) * mm});
            skLineSegment(sketch, "E742", {"start": v(216.54, -119.24) * mm, "end": v(217, -119.3) * mm});
            skLineSegment(sketch, "E743", {"start": v(217, -122.78) * mm, "end": v(216.53, -122.84) * mm});
            skLineSegment(sketch, "E744", {"start": v(216.07, -119.3) * mm, "end": v(216.54, -119.24) * mm});
            skLineSegment(sketch, "E745", {"start": v(217.8, -122.32) * mm, "end": v(217.43, -122.6) * mm});
            skLineSegment(sketch, "E746", {"start": v(217.43, -122.6) * mm, "end": v(217, -122.78) * mm});
            skLineSegment(sketch, "E747", {"start": v(214.98, -121.94) * mm, "end": v(214.8, -121.5) * mm});
            skLineSegment(sketch, "E748", {"start": v(218.27, -121.5) * mm, "end": v(218.1, -121.94) * mm});
            skLineSegment(sketch, "E749", {"start": v(216.48, -122.84) * mm, "end": v(216.07, -122.78) * mm});
            skLineSegment(sketch, "E750", {"start": v(217.44, -119.48) * mm, "end": v(217.8, -119.77) * mm});
            skLineSegment(sketch, "E751", {"start": v(217.8, -119.77) * mm, "end": v(218.1, -120.14) * mm});
            skLineSegment(sketch, "E752", {"start": v(216.53, -122.84) * mm, "end": v(216.48, -122.84) * mm});
            skLineSegment(sketch, "E753", {"start": v(218.34, -121.04) * mm, "end": v(218.33, -121.08) * mm});
            skLineSegment(sketch, "E754", {"start": v(218.33, -121.08) * mm, "end": v(218.27, -121.5) * mm});
            skLineSegment(sketch, "E755", {"start": v(261.37, -122.6) * mm, "end": v(260.93, -122.78) * mm});
            skLineSegment(sketch, "E756", {"start": v(258.9, -121.94) * mm, "end": v(258.73, -121.5) * mm});
            skLineSegment(sketch, "E757", {"start": v(261.37, -119.48) * mm, "end": v(261.74, -119.77) * mm});
            skLineSegment(sketch, "E758", {"start": v(261.74, -119.77) * mm, "end": v(262.03, -120.14) * mm});
            skLineSegment(sketch, "E759", {"start": v(258.67, -121.04) * mm, "end": v(258.73, -120.58) * mm});
            skLineSegment(sketch, "E760", {"start": v(259.57, -119.48) * mm, "end": v(260, -119.3) * mm});
            skLineSegment(sketch, "E761", {"start": v(259.2, -122.32) * mm, "end": v(258.9, -121.94) * mm});
            skLineSegment(sketch, "E762", {"start": v(262.03, -121.94) * mm, "end": v(261.74, -122.32) * mm});
            skLineSegment(sketch, "E763", {"start": v(260, -122.78) * mm, "end": v(259.57, -122.6) * mm});
            skLineSegment(sketch, "E764", {"start": v(259.2, -119.77) * mm, "end": v(259.57, -119.48) * mm});
            skLineSegment(sketch, "E765", {"start": v(262.03, -120.14) * mm, "end": v(262.2, -120.58) * mm});
            skLineSegment(sketch, "E766", {"start": v(262.2, -120.58) * mm, "end": v(262.26, -120.99) * mm});
            skLineSegment(sketch, "E767", {"start": v(262.26, -120.99) * mm, "end": v(262.27, -121.04) * mm});
            skLineSegment(sketch, "E768", {"start": v(260.93, -119.3) * mm, "end": v(261.37, -119.48) * mm});
            skLineSegment(sketch, "E769", {"start": v(260.47, -119.24) * mm, "end": v(260.54, -119.25) * mm});
            skLineSegment(sketch, "E770", {"start": v(260.93, -122.78) * mm, "end": v(260.47, -122.84) * mm});
            skLineSegment(sketch, "E771", {"start": v(259.57, -122.6) * mm, "end": v(259.2, -122.32) * mm});
            skLineSegment(sketch, "E772", {"start": v(258.73, -121.5) * mm, "end": v(258.67, -121.08) * mm});
            skLineSegment(sketch, "E773", {"start": v(262.2, -121.5) * mm, "end": v(262.03, -121.94) * mm});
            skLineSegment(sketch, "E774", {"start": v(260, -119.3) * mm, "end": v(260.47, -119.24) * mm});
            skLineSegment(sketch, "E775", {"start": v(260.47, -122.84) * mm, "end": v(260.41, -122.84) * mm});
            skLineSegment(sketch, "E776", {"start": v(262.27, -121.04) * mm, "end": v(262.2, -121.5) * mm});
            skLineSegment(sketch, "E777", {"start": v(258.73, -120.58) * mm, "end": v(258.9, -120.14) * mm});
            skLineSegment(sketch, "E778", {"start": v(261.74, -122.32) * mm, "end": v(261.37, -122.6) * mm});
            skLineSegment(sketch, "E779", {"start": v(258.9, -120.14) * mm, "end": v(259.2, -119.77) * mm});
            skLineSegment(sketch, "E780", {"start": v(260.41, -122.84) * mm, "end": v(260, -122.78) * mm});
            skLineSegment(sketch, "E781", {"start": v(260.54, -119.25) * mm, "end": v(260.93, -119.3) * mm});
            skLineSegment(sketch, "E782", {"start": v(258.67, -121.08) * mm, "end": v(258.67, -121.04) * mm});
            skLineSegment(sketch, "E783", {"start": v(218.2, -32.59) * mm, "end": v(219.35, -32.59) * mm});
            skLineSegment(sketch, "E784", {"start": v(218.2, -31.49) * mm, "end": v(219.35, -31.49) * mm});
            skLineSegment(sketch, "E785", {"start": v(219.35, -30.39) * mm, "end": v(218.2, -30.39) * mm});
            skLineSegment(sketch, "E786", {"start": v(219.35, -30.39) * mm, "end": v(219.35, -31.49) * mm});
            skLineSegment(sketch, "E787", {"start": v(219.35, -31.49) * mm, "end": v(219.35, -32.59) * mm});
            skLineSegment(sketch, "E788", {"start": v(257.86, -30.84) * mm, "end": v(257.86, -31.94) * mm});
            skLineSegment(sketch, "E789", {"start": v(257.86, -30.84) * mm, "end": v(256.71, -30.84) * mm});
            skLineSegment(sketch, "E790", {"start": v(257.86, -31.94) * mm, "end": v(257.86, -33.04) * mm});
            skLineSegment(sketch, "E791", {"start": v(256.71, -33.04) * mm, "end": v(257.86, -33.04) * mm});
            skLineSegment(sketch, "E792", {"start": v(256.71, -31.94) * mm, "end": v(257.86, -31.94) * mm});
            skLineSegment(sketch, "E793", {"start": v(255.87, -116.27) * mm, "end": v(257.02, -116.27) * mm});
            skLineSegment(sketch, "E794", {"start": v(257.02, -115.17) * mm, "end": v(257.02, -116.27) * mm});
            skLineSegment(sketch, "E795", {"start": v(255.87, -117.37) * mm, "end": v(257.02, -117.37) * mm});
            skLineSegment(sketch, "E796", {"start": v(257.02, -115.17) * mm, "end": v(255.87, -115.17) * mm});
            skLineSegment(sketch, "E797", {"start": v(257.02, -116.27) * mm, "end": v(257.02, -117.37) * mm});
            skLineSegment(sketch, "E798", {"start": v(221.1, -114.8) * mm, "end": v(221.1, -115.9) * mm});
            skLineSegment(sketch, "E799", {"start": v(221.1, -114.8) * mm, "end": v(219.94, -114.8) * mm});
            skLineSegment(sketch, "E800", {"start": v(221.1, -115.9) * mm, "end": v(221.1, -117) * mm});
            skLineSegment(sketch, "E801", {"start": v(219.94, -117) * mm, "end": v(221.1, -117) * mm});
            skLineSegment(sketch, "E802", {"start": v(219.94, -115.9) * mm, "end": v(221.1, -115.9) * mm});
            skLineSegment(sketch, "E803", {"start": v(-230.54, 112.97) * mm, "end": v(-230.54, 92.97) * mm});
            skLineSegment(sketch, "E804", {"start": v(-40.54, 16.97) * mm, "end": v(-50.54, 6.97) * mm});
            skLineSegment(sketch, "E805", {"start": v(-220.54, 76.98) * mm, "end": v(-220.54, 53.98) * mm});
            skLineSegment(sketch, "E806", {"start": v(-227.58, 10.83) * mm, "end": v(-228.07, 10.66) * mm});
            skLineSegment(sketch, "E807", {"start": v(-224.54, 49.98) * mm, "end": v(-226.54, 49.98) * mm});
            skLineSegment(sketch, "E808", {"start": v(-227.58, 80.84) * mm, "end": v(-228.07, 80.67) * mm});
            skLineSegment(sketch, "E809", {"start": v(-228.07, 10.66) * mm, "end": v(-228.54, 10.43) * mm});
            skLineSegment(sketch, "E810", {"start": v(-228.98, 10.14) * mm, "end": v(-229.37, 9.8) * mm});
            skLineSegment(sketch, "E811", {"start": v(-228.54, 10.43) * mm, "end": v(-228.98, 10.14) * mm});
            skLineSegment(sketch, "E812", {"start": v(-243.54, -80.03) * mm, "end": v(-218.54, -55.03) * mm});
            skLineSegment(sketch, "E813", {"start": v(-226.54, 80.98) * mm, "end": v(-227.06, 80.94) * mm});
            skLineSegment(sketch, "E814", {"start": v(-223.01, 50.28) * mm, "end": v(-222.54, 50.51) * mm});
            skLineSegment(sketch, "E815", {"start": v(-240.54, -23.03) * mm, "end": v(-230.54, -33.03) * mm});
            skLineSegment(sketch, "E816", {"start": v(-230.54, 92.97) * mm, "end": v(-240.54, 82.97) * mm});
            skLineSegment(sketch, "E817", {"start": v(-250.54, -73.03) * mm, "end": v(-250.54, -77.03) * mm});
            skLineSegment(sketch, "E818", {"start": v(-208.54, 104.97) * mm, "end": v(-72.54, 104.97) * mm});
            skLineSegment(sketch, "E819", {"start": v(-229.72, 9.4) * mm, "end": v(-230, 8.97) * mm});
            skLineSegment(sketch, "E820", {"start": v(-229.37, 9.8) * mm, "end": v(-229.72, 9.4) * mm});
            skLineSegment(sketch, "E821", {"start": v(-250.54, 134.97) * mm, "end": v(-250.54, 132.97) * mm});
            skLineSegment(sketch, "E822", {"start": v(-60.4, 16.8) * mm, "end": v(-60.24, 16.3) * mm});
            skLineSegment(sketch, "E823", {"start": v(-60.5, 17.3) * mm, "end": v(-60.4, 16.8) * mm});
            skLineSegment(sketch, "E824", {"start": v(-223.01, 80.67) * mm, "end": v(-223.5, 80.84) * mm});
            skLineSegment(sketch, "E825", {"start": v(-221.37, 9.4) * mm, "end": v(-221.71, 9.8) * mm});
            skLineSegment(sketch, "E826", {"start": v(-58.07, 14.14) * mm, "end": v(-57.58, 13.97) * mm});
            skLineSegment(sketch, "E827", {"start": v(-230.24, 52.44) * mm, "end": v(-230, 51.98) * mm});
            skLineSegment(sketch, "E828", {"start": v(-230, 51.98) * mm, "end": v(-229.72, 51.54) * mm});
            skLineSegment(sketch, "E829", {"start": v(-229.72, 51.54) * mm, "end": v(-229.37, 51.15) * mm});
            skLineSegment(sketch, "E830", {"start": v(-229.37, 51.15) * mm, "end": v(-228.98, 50.8) * mm});
            skLineSegment(sketch, "E831", {"start": v(-250.54, -73.03) * mm, "end": v(-230.54, -53.03) * mm});
            skLineSegment(sketch, "E832", {"start": v(-53.5, 13.97) * mm, "end": v(-53.01, 14.14) * mm});
            skLineSegment(sketch, "E833", {"start": v(-54.02, 13.87) * mm, "end": v(-53.5, 13.97) * mm});
            skLineSegment(sketch, "E834", {"start": v(-54.54, 13.83) * mm, "end": v(-54.02, 13.87) * mm});
            skLineSegment(sketch, "E835", {"start": v(-160.54, 34.97) * mm, "end": v(-160.54, 24.97) * mm});
            skLineSegment(sketch, "E836", {"start": v(-230.54, 34.97) * mm, "end": v(-230.54, 24.97) * mm});
            skLineSegment(sketch, "E837", {"start": v(-230.54, 53.98) * mm, "end": v(-230.54, 76.98) * mm});
            skLineSegment(sketch, "E838", {"start": v(-37.54, -80.03) * mm, "end": v(-35.47, -80.03) * mm});
            skLineSegment(sketch, "E839", {"start": v(-228.54, 50.51) * mm, "end": v(-228.07, 50.28) * mm});
            skLineSegment(sketch, "E840", {"start": v(-228.98, 50.8) * mm, "end": v(-228.54, 50.51) * mm});
            skLineSegment(sketch, "E841", {"start": v(-230.4, 52.94) * mm, "end": v(-230.24, 52.44) * mm});
            skLineSegment(sketch, "E842", {"start": v(-230.54, 53.98) * mm, "end": v(-230.5, 53.45) * mm});
            skLineSegment(sketch, "E843", {"start": v(-224.02, 80.94) * mm, "end": v(-224.54, 80.98) * mm});
            skLineSegment(sketch, "E844", {"start": v(-223.5, 80.84) * mm, "end": v(-224.02, 80.94) * mm});
            skLineSegment(sketch, "E845", {"start": v(-222.1, 80.15) * mm, "end": v(-222.54, 80.44) * mm});
            skLineSegment(sketch, "E846", {"start": v(-221.71, 79.8) * mm, "end": v(-222.1, 80.15) * mm});
            skLineSegment(sketch, "E847", {"start": v(-221.08, 78.98) * mm, "end": v(-221.37, 79.41) * mm});
            skLineSegment(sketch, "E848", {"start": v(-223.5, -19.9) * mm, "end": v(-223.01, -19.73) * mm});
            skLineSegment(sketch, "E849", {"start": v(-33.54, -80.03) * mm, "end": v(-30.54, -77.03) * mm});
            skLineSegment(sketch, "E850", {"start": v(-220.85, -17.56) * mm, "end": v(-220.68, -17.07) * mm});
            skLineSegment(sketch, "E851", {"start": v(-220.68, -17.07) * mm, "end": v(-220.58, -16.55) * mm});
            skLineSegment(sketch, "E852", {"start": v(-220.58, -16.55) * mm, "end": v(-220.54, -16.03) * mm});
            skLineSegment(sketch, "E853", {"start": v(-218.54, 114.97) * mm, "end": v(-62.54, 114.97) * mm});
            skLineSegment(sketch, "E854", {"start": v(-223.01, -19.73) * mm, "end": v(-222.54, -19.5) * mm});
            skLineSegment(sketch, "E855", {"start": v(-222.54, -19.5) * mm, "end": v(-222.1, -19.2) * mm});
            skLineSegment(sketch, "E856", {"start": v(-222.1, -19.2) * mm, "end": v(-221.71, -18.86) * mm});
            skLineSegment(sketch, "E857", {"start": v(-220.54, 24.97) * mm, "end": v(-220.54, 34.97) * mm});
            skLineSegment(sketch, "E858", {"start": v(-230.54, 24.97) * mm, "end": v(-240.54, 14.97) * mm});
            skLineSegment(sketch, "E859", {"start": v(-57.58, 13.97) * mm, "end": v(-57.06, 13.87) * mm});
            skLineSegment(sketch, "E860", {"start": v(-57.06, 13.87) * mm, "end": v(-56.54, 13.83) * mm});
            skLineSegment(sketch, "E861", {"start": v(-54.54, 13.83) * mm, "end": v(-56.54, 13.83) * mm});
            skLineSegment(sketch, "E862", {"start": v(-221.71, -18.86) * mm, "end": v(-221.37, -18.47) * mm});
            skLineSegment(sketch, "E863", {"start": v(-221.37, -18.47) * mm, "end": v(-221.08, -18.03) * mm});
            skLineSegment(sketch, "E864", {"start": v(-221.08, -18.03) * mm, "end": v(-220.85, -17.56) * mm});
            skLineSegment(sketch, "E865", {"start": v(-180.54, 54.97) * mm, "end": v(-160.54, 34.97) * mm});
            skLineSegment(sketch, "E866", {"start": v(-230.4, -17.07) * mm, "end": v(-230.24, -17.56) * mm});
            skLineSegment(sketch, "E867", {"start": v(-59.72, 15.4) * mm, "end": v(-59.37, 15) * mm});
            skLineSegment(sketch, "E868", {"start": v(-240.54, 44.97) * mm, "end": v(-230.54, 34.97) * mm});
            skLineSegment(sketch, "E869", {"start": v(-223.01, 10.66) * mm, "end": v(-223.5, 10.83) * mm});
            skLineSegment(sketch, "E870", {"start": v(-223.5, 10.83) * mm, "end": v(-224.02, 10.93) * mm});
            skLineSegment(sketch, "E871", {"start": v(-224.02, 10.93) * mm, "end": v(-224.54, 10.97) * mm});
            skLineSegment(sketch, "E872", {"start": v(-250.54, 136.97) * mm, "end": v(-250.54, 134.97) * mm});
            skLineSegment(sketch, "E873", {"start": v(-250.54, -77.03) * mm, "end": v(-247.54, -80.03) * mm});
            skLineSegment(sketch, "E874", {"start": v(-60.54, 17.83) * mm, "end": v(-60.5, 17.3) * mm});
            skLineSegment(sketch, "E875", {"start": v(-226.54, 10.97) * mm, "end": v(-227.06, 10.93) * mm});
            skLineSegment(sketch, "E876", {"start": v(-227.06, 10.93) * mm, "end": v(-227.58, 10.83) * mm});
            skLineSegment(sketch, "E877", {"start": v(-230.54, -16.03) * mm, "end": v(-230.54, 6.97) * mm});
            skLineSegment(sketch, "E878", {"start": v(-230.54, -16.03) * mm, "end": v(-230.5, -16.55) * mm});
            skLineSegment(sketch, "E879", {"start": v(-230.5, -16.55) * mm, "end": v(-230.4, -17.07) * mm});
            skLineSegment(sketch, "E880", {"start": v(-50.54, 6.97) * mm, "end": v(-70.54, -13.03) * mm});
            skLineSegment(sketch, "E881", {"start": v(-30.54, 136.97) * mm, "end": v(-33.54, 139.97) * mm});
            skLineSegment(sketch, "E882", {"start": v(-240.54, 82.97) * mm, "end": v(-240.54, 44.97) * mm});
            skLineSegment(sketch, "E883", {"start": v(-224.54, -20.03) * mm, "end": v(-224.02, -20) * mm});
            skLineSegment(sketch, "E884", {"start": v(-227.58, -19.9) * mm, "end": v(-227.06, -20) * mm});
            skLineSegment(sketch, "E885", {"start": v(-227.06, -20) * mm, "end": v(-226.54, -20.03) * mm});
            skLineSegment(sketch, "E886", {"start": v(-30.54, -73.03) * mm, "end": v(-50.54, -53.03) * mm});
            skLineSegment(sketch, "E887", {"start": v(-50.54, -53.03) * mm, "end": v(-70.54, -33.03) * mm});
            skLineSegment(sketch, "E888", {"start": v(-70.54, -33.03) * mm, "end": v(-70.54, -13.03) * mm});
            skLineSegment(sketch, "E889", {"start": v(-50.58, 41.35) * mm, "end": v(-50.68, 41.87) * mm});
            skLineSegment(sketch, "E890", {"start": v(-50.54, 40.83) * mm, "end": v(-50.58, 41.35) * mm});
            skLineSegment(sketch, "E891", {"start": v(-222.54, 10.43) * mm, "end": v(-223.01, 10.66) * mm});
            skLineSegment(sketch, "E892", {"start": v(-222.1, 10.14) * mm, "end": v(-222.54, 10.43) * mm});
            skLineSegment(sketch, "E893", {"start": v(-221.71, 9.8) * mm, "end": v(-222.1, 10.14) * mm});
            skLineSegment(sketch, "E894", {"start": v(-37.54, 139.97) * mm, "end": v(-60.54, 116.97) * mm});
            skLineSegment(sketch, "E895", {"start": v(-180.54, 4.97) * mm, "end": v(-200.54, 4.97) * mm});
            skLineSegment(sketch, "E896", {"start": v(-247.54, 139.97) * mm, "end": v(-250.54, 136.97) * mm});
            skLineSegment(sketch, "E897", {"start": v(-33.54, 139.97) * mm, "end": v(-37.54, 139.97) * mm});
            skLineSegment(sketch, "E898", {"start": v(-245.54, 139.97) * mm, "end": v(-245.47, 139.97) * mm});
            skLineSegment(sketch, "E899", {"start": v(-243.54, -80.03) * mm, "end": v(-245.47, -80.03) * mm});
            skLineSegment(sketch, "E900", {"start": v(-30.54, 132.97) * mm, "end": v(-70.54, 92.97) * mm});
            skLineSegment(sketch, "E901", {"start": v(-59.37, 43.66) * mm, "end": v(-59.72, 43.27) * mm});
            skLineSegment(sketch, "E902", {"start": v(-58.98, 44) * mm, "end": v(-59.37, 43.66) * mm});
            skLineSegment(sketch, "E903", {"start": v(-58.07, 44.53) * mm, "end": v(-58.54, 44.3) * mm});
            skLineSegment(sketch, "E904", {"start": v(-57.58, 44.7) * mm, "end": v(-58.07, 44.53) * mm});
            skLineSegment(sketch, "E905", {"start": v(-52.1, 14.66) * mm, "end": v(-51.71, 15) * mm});
            skLineSegment(sketch, "E906", {"start": v(-220.85, 8.5) * mm, "end": v(-221.08, 8.97) * mm});
            skLineSegment(sketch, "E907", {"start": v(-221.08, 8.97) * mm, "end": v(-221.37, 9.4) * mm});
            skLineSegment(sketch, "E908", {"start": v(-30.54, -73.03) * mm, "end": v(-30.54, -77.03) * mm});
            skLineSegment(sketch, "E909", {"start": v(-230.54, -53.03) * mm, "end": v(-230.54, -33.03) * mm});
            skLineSegment(sketch, "E910", {"start": v(-245.54, 139.97) * mm, "end": v(-247.54, 139.97) * mm});
            skLineSegment(sketch, "E911", {"start": v(-70.54, 72.97) * mm, "end": v(-70.54, 92.97) * mm});
            skLineSegment(sketch, "E912", {"start": v(-50.54, 52.97) * mm, "end": v(-70.54, 72.97) * mm});
            skLineSegment(sketch, "E913", {"start": v(-50.58, 17.3) * mm, "end": v(-50.54, 17.83) * mm});
            skLineSegment(sketch, "E914", {"start": v(-50.54, 40.83) * mm, "end": v(-50.54, 17.83) * mm});
            skLineSegment(sketch, "E915", {"start": v(-54.02, 44.8) * mm, "end": v(-54.54, 44.83) * mm});
            skLineSegment(sketch, "E916", {"start": v(-53.5, 44.7) * mm, "end": v(-54.02, 44.8) * mm});
            skLineSegment(sketch, "E917", {"start": v(-218.54, -55.03) * mm, "end": v(-62.54, -55.03) * mm});
            skLineSegment(sketch, "E918", {"start": v(-230.24, 8.5) * mm, "end": v(-230.4, 8) * mm});
            skLineSegment(sketch, "E919", {"start": v(-230.4, 8) * mm, "end": v(-230.5, 7.5) * mm});
            skLineSegment(sketch, "E920", {"start": v(-230.5, 7.5) * mm, "end": v(-230.54, 6.97) * mm});
            skLineSegment(sketch, "E921", {"start": v(-226.54, 10.97) * mm, "end": v(-224.54, 10.97) * mm});
            skLineSegment(sketch, "E922", {"start": v(-37.54, -80.03) * mm, "end": v(-62.54, -55.03) * mm});
            skLineSegment(sketch, "E923", {"start": v(-40.54, 42.97) * mm, "end": v(-50.54, 52.97) * mm});
            skLineSegment(sketch, "E924", {"start": v(-30.54, 135.97) * mm, "end": v(-30.54, 136.97) * mm});
            skLineSegment(sketch, "E925", {"start": v(-243.54, 139.97) * mm, "end": v(-218.54, 114.97) * mm});
            skLineSegment(sketch, "E926", {"start": v(-40.54, 42.97) * mm, "end": v(-40.54, 16.97) * mm});
            skLineSegment(sketch, "E927", {"start": v(-35.47, -80.03) * mm, "end": v(-33.54, -80.03) * mm});
            skLineSegment(sketch, "E928", {"start": v(-240.54, 14.97) * mm, "end": v(-240.54, -23.03) * mm});
            skLineSegment(sketch, "E929", {"start": v(-245.47, 139.97) * mm, "end": v(-243.54, 139.97) * mm});
            skLineSegment(sketch, "E930", {"start": v(-245.47, -80.03) * mm, "end": v(-247.54, -80.03) * mm});
            skLineSegment(sketch, "E931", {"start": v(-30.54, 135.97) * mm, "end": v(-30.54, 132.97) * mm});
            skLineSegment(sketch, "E932", {"start": v(-250.54, 132.97) * mm, "end": v(-230.54, 112.97) * mm});
            skLineSegment(sketch, "E933", {"start": v(-60.54, 116.97) * mm, "end": v(-62.54, 114.97) * mm});
            skLineSegment(sketch, "E934", {"start": v(-100.54, 76.97) * mm, "end": v(-102.54, 74.97) * mm});
            skLineSegment(sketch, "E935", {"start": v(-102.54, 74.97) * mm, "end": v(-112.54, 64.97) * mm});
            skLineSegment(sketch, "E936", {"start": v(-72.54, 104.97) * mm, "end": v(-100.54, 76.97) * mm});
            skLineSegment(sketch, "E937", {"start": v(-112.47, 64.97) * mm, "end": v(-112.54, 64.97) * mm});
            skLineSegment(sketch, "E938", {"start": v(-112.54, 64.97) * mm, "end": v(-168.54, 64.97) * mm});
            skLineSegment(sketch, "E939", {"start": v(-208.54, 104.97) * mm, "end": v(-168.54, 64.97) * mm});
            skLineSegment(sketch, "E940", {"start": v(-160.54, 24.97) * mm, "end": v(-180.54, 4.97) * mm});
            skLineSegment(sketch, "E941", {"start": v(-180.54, 54.97) * mm, "end": v(-180.47, 54.97) * mm});
            skLineSegment(sketch, "E942", {"start": v(-220.54, 34.97) * mm, "end": v(-200.54, 54.97) * mm});
            skLineSegment(sketch, "E943", {"start": v(-200.54, 54.97) * mm, "end": v(-180.54, 54.97) * mm});
            skLineSegment(sketch, "E944", {"start": v(-200.54, 4.97) * mm, "end": v(-220.54, 24.97) * mm});
            skLineSegment(sketch, "E945", {"start": v(-70.54, 34.97) * mm, "end": v(-70.54, 24.97) * mm});
            skLineSegment(sketch, "E946", {"start": v(-120.54, 24.97) * mm, "end": v(-120.54, 34.97) * mm});
            skLineSegment(sketch, "E947", {"start": v(-80.47, 44.9) * mm, "end": v(-70.54, 34.97) * mm});
            skLineSegment(sketch, "E948", {"start": v(-90.54, 54.97) * mm, "end": v(-80.47, 44.9) * mm});
            skLineSegment(sketch, "E949", {"start": v(-70.54, 24.97) * mm, "end": v(-80.47, 15.04) * mm});
            skLineSegment(sketch, "E950", {"start": v(-100.54, 4.97) * mm, "end": v(-120.54, 24.97) * mm});
            skLineSegment(sketch, "E951", {"start": v(-120.54, 34.97) * mm, "end": v(-100.54, 54.97) * mm});
            skLineSegment(sketch, "E952", {"start": v(-80.47, 15.04) * mm, "end": v(-90.54, 4.97) * mm});
            skLineSegment(sketch, "E953", {"start": v(-100.54, 54.97) * mm, "end": v(-90.54, 54.97) * mm});
            skLineSegment(sketch, "E954", {"start": v(-80.47, 15.04) * mm, "end": v(-80.47, 14.97) * mm});
            skLineSegment(sketch, "E955", {"start": v(-90.54, 4.97) * mm, "end": v(-100.54, 4.97) * mm});
            skLineSegment(sketch, "E956", {"start": v(-72.54, -45.03) * mm, "end": v(-208.47, -45.03) * mm});
            skLineSegment(sketch, "E957", {"start": v(-112.54, -5.03) * mm, "end": v(-168.47, -5.03) * mm});
            skLineSegment(sketch, "E958", {"start": v(-72.54, 104.97) * mm, "end": v(-72.47, 104.97) * mm});
            skLineSegment(sketch, "E959", {"start": v(-50.68, 41.87) * mm, "end": v(-50.85, 42.36) * mm});
            skLineSegment(sketch, "E960", {"start": v(-60.5, 41.35) * mm, "end": v(-60.54, 40.83) * mm});
            skLineSegment(sketch, "E961", {"start": v(-59.72, 43.27) * mm, "end": v(-60, 42.83) * mm});
            skLineSegment(sketch, "E962", {"start": v(-57.06, 44.8) * mm, "end": v(-57.58, 44.7) * mm});
            skLineSegment(sketch, "E963", {"start": v(-56.54, 44.83) * mm, "end": v(-57.06, 44.8) * mm});
            skLineSegment(sketch, "E964", {"start": v(-56.54, 44.83) * mm, "end": v(-54.54, 44.83) * mm});
            skLineSegment(sketch, "E965", {"start": v(-60.54, 17.83) * mm, "end": v(-60.54, 40.83) * mm});
            skLineSegment(sketch, "E966", {"start": v(-60, 15.83) * mm, "end": v(-59.72, 15.4) * mm});
            skLineSegment(sketch, "E967", {"start": v(-60.4, 41.87) * mm, "end": v(-60.5, 41.35) * mm});
            skLineSegment(sketch, "E968", {"start": v(-60.24, 42.36) * mm, "end": v(-60.4, 41.87) * mm});
            skLineSegment(sketch, "E969", {"start": v(-60, 42.83) * mm, "end": v(-60.24, 42.36) * mm});
            skLineSegment(sketch, "E970", {"start": v(-52.1, 44) * mm, "end": v(-52.54, 44.3) * mm});
            skLineSegment(sketch, "E971", {"start": v(-52.54, 44.3) * mm, "end": v(-53.01, 44.53) * mm});
            skLineSegment(sketch, "E972", {"start": v(-53.01, 44.53) * mm, "end": v(-53.5, 44.7) * mm});
            skLineSegment(sketch, "E973", {"start": v(-50.85, 42.36) * mm, "end": v(-51.08, 42.83) * mm});
            skLineSegment(sketch, "E974", {"start": v(-59.37, 15) * mm, "end": v(-58.98, 14.66) * mm});
            skLineSegment(sketch, "E975", {"start": v(-51.08, 42.83) * mm, "end": v(-51.37, 43.27) * mm});
            skLineSegment(sketch, "E976", {"start": v(-51.37, 43.27) * mm, "end": v(-51.71, 43.66) * mm});
            skLineSegment(sketch, "E977", {"start": v(-51.71, 43.66) * mm, "end": v(-52.1, 44) * mm});
            skLineSegment(sketch, "E978", {"start": v(-51.37, 15.4) * mm, "end": v(-51.08, 15.83) * mm});
            skLineSegment(sketch, "E979", {"start": v(-58.54, 44.3) * mm, "end": v(-58.98, 44) * mm});
            skLineSegment(sketch, "E980", {"start": v(-60.24, 16.3) * mm, "end": v(-60, 15.83) * mm});
            skLineSegment(sketch, "E981", {"start": v(-51.08, 15.83) * mm, "end": v(-50.85, 16.3) * mm});
            skLineSegment(sketch, "E982", {"start": v(-50.85, 16.3) * mm, "end": v(-50.68, 16.8) * mm});
            skLineSegment(sketch, "E983", {"start": v(-50.68, 16.8) * mm, "end": v(-50.58, 17.3) * mm});
            skLineSegment(sketch, "E984", {"start": v(-51.71, 15) * mm, "end": v(-51.37, 15.4) * mm});
            skLineSegment(sketch, "E985", {"start": v(-52.54, 14.37) * mm, "end": v(-52.1, 14.66) * mm});
            skLineSegment(sketch, "E986", {"start": v(-53.01, 14.14) * mm, "end": v(-52.54, 14.37) * mm});
            skLineSegment(sketch, "E987", {"start": v(-58.54, 14.37) * mm, "end": v(-58.07, 14.14) * mm});
            skLineSegment(sketch, "E988", {"start": v(-58.98, 14.66) * mm, "end": v(-58.54, 14.37) * mm});
            skLineSegment(sketch, "E989", {"start": v(-220.58, 53.45) * mm, "end": v(-220.54, 53.98) * mm});
            skLineSegment(sketch, "E990", {"start": v(-220.68, 52.94) * mm, "end": v(-220.58, 53.45) * mm});
            skLineSegment(sketch, "E991", {"start": v(-224.02, 50) * mm, "end": v(-223.5, 50.11) * mm});
            skLineSegment(sketch, "E992", {"start": v(-222.54, 50.51) * mm, "end": v(-222.1, 50.8) * mm});
            skLineSegment(sketch, "E993", {"start": v(-222.1, 50.8) * mm, "end": v(-221.71, 51.15) * mm});
            skLineSegment(sketch, "E994", {"start": v(-221.71, 51.15) * mm, "end": v(-221.37, 51.54) * mm});
            skLineSegment(sketch, "E995", {"start": v(-220.85, 52.44) * mm, "end": v(-220.68, 52.94) * mm});
            skLineSegment(sketch, "E996", {"start": v(-221.37, 51.54) * mm, "end": v(-221.08, 51.98) * mm});
            skLineSegment(sketch, "E997", {"start": v(-221.08, 51.98) * mm, "end": v(-220.85, 52.44) * mm});
            skLineSegment(sketch, "E998", {"start": v(-228.54, 80.44) * mm, "end": v(-228.98, 80.15) * mm});
            skLineSegment(sketch, "E999", {"start": v(-228.98, 80.15) * mm, "end": v(-229.37, 79.8) * mm});
            skLineSegment(sketch, "E1000", {"start": v(-229.37, 79.8) * mm, "end": v(-229.72, 79.41) * mm});
            skLineSegment(sketch, "E1001", {"start": v(-229.72, 79.41) * mm, "end": v(-230, 78.98) * mm});
            skLineSegment(sketch, "E1002", {"start": v(-230, 78.98) * mm, "end": v(-230.24, 78.5) * mm});
            skLineSegment(sketch, "E1003", {"start": v(-230.24, 78.5) * mm, "end": v(-230.4, 78.01) * mm});
            skLineSegment(sketch, "E1004", {"start": v(-230.4, 78.01) * mm, "end": v(-230.5, 77.5) * mm});
            skLineSegment(sketch, "E1005", {"start": v(-230.5, 77.5) * mm, "end": v(-230.54, 76.98) * mm});
            skLineSegment(sketch, "E1006", {"start": v(-220.58, 77.5) * mm, "end": v(-220.68, 78.01) * mm});
            skLineSegment(sketch, "E1007", {"start": v(-220.68, 78.01) * mm, "end": v(-220.85, 78.5) * mm});
            skLineSegment(sketch, "E1008", {"start": v(-220.85, 78.5) * mm, "end": v(-221.08, 78.98) * mm});
            skLineSegment(sketch, "E1009", {"start": v(-221.37, 79.41) * mm, "end": v(-221.71, 79.8) * mm});
            skLineSegment(sketch, "E1010", {"start": v(-228.07, 50.28) * mm, "end": v(-227.58, 50.11) * mm});
            skLineSegment(sketch, "E1011", {"start": v(-227.58, 50.11) * mm, "end": v(-227.06, 50) * mm});
            skLineSegment(sketch, "E1012", {"start": v(-227.06, 50) * mm, "end": v(-226.54, 49.98) * mm});
            skLineSegment(sketch, "E1013", {"start": v(-220.54, 76.98) * mm, "end": v(-220.58, 77.5) * mm});
            skLineSegment(sketch, "E1014", {"start": v(-227.06, 80.94) * mm, "end": v(-227.58, 80.84) * mm});
            skLineSegment(sketch, "E1015", {"start": v(-230.5, 53.45) * mm, "end": v(-230.4, 52.94) * mm});
            skLineSegment(sketch, "E1016", {"start": v(-223.5, 50.11) * mm, "end": v(-223.01, 50.28) * mm});
            skLineSegment(sketch, "E1017", {"start": v(-226.54, 80.98) * mm, "end": v(-224.54, 80.98) * mm});
            skLineSegment(sketch, "E1018", {"start": v(-222.54, 80.44) * mm, "end": v(-223.01, 80.67) * mm});
            skLineSegment(sketch, "E1019", {"start": v(-224.54, 49.98) * mm, "end": v(-224.02, 50) * mm});
            skLineSegment(sketch, "E1020", {"start": v(-228.07, 80.67) * mm, "end": v(-228.54, 80.44) * mm});
            skLineSegment(sketch, "E1021", {"start": v(-228.07, -19.73) * mm, "end": v(-227.58, -19.9) * mm});
            skLineSegment(sketch, "E1022", {"start": v(-228.54, -19.5) * mm, "end": v(-228.07, -19.73) * mm});
            skLineSegment(sketch, "E1023", {"start": v(-228.98, -19.2) * mm, "end": v(-228.54, -19.5) * mm});
            skLineSegment(sketch, "E1024", {"start": v(-229.37, -18.86) * mm, "end": v(-228.98, -19.2) * mm});
            skLineSegment(sketch, "E1025", {"start": v(-224.54, -20.03) * mm, "end": v(-226.54, -20.03) * mm});
            skLineSegment(sketch, "E1026", {"start": v(-220.68, 8) * mm, "end": v(-220.85, 8.5) * mm});
            skLineSegment(sketch, "E1027", {"start": v(-220.58, 7.5) * mm, "end": v(-220.68, 8) * mm});
            skLineSegment(sketch, "E1028", {"start": v(-220.54, 6.97) * mm, "end": v(-220.58, 7.5) * mm});
            skLineSegment(sketch, "E1029", {"start": v(-224.02, -20) * mm, "end": v(-223.5, -19.9) * mm});
            skLineSegment(sketch, "E1030", {"start": v(-230.24, -17.56) * mm, "end": v(-230, -18.03) * mm});
            skLineSegment(sketch, "E1031", {"start": v(-230, -18.03) * mm, "end": v(-229.72, -18.47) * mm});
            skLineSegment(sketch, "E1032", {"start": v(-229.72, -18.47) * mm, "end": v(-229.37, -18.86) * mm});
            skLineSegment(sketch, "E1033", {"start": v(-220.54, 6.97) * mm, "end": v(-220.54, -16.03) * mm});
            skLineSegment(sketch, "E1034", {"start": v(-230, 8.97) * mm, "end": v(-230.24, 8.5) * mm});
            skLineSegment(sketch, "E1035", {"start": v(-191.55, 164.03) * mm, "end": v(-186.98, 162.9) * mm});
            skLineSegment(sketch, "E1036", {"start": v(-186.98, 162.9) * mm, "end": v(-185.72, 162.15) * mm});
            skLineSegment(sketch, "E1037", {"start": v(-185.72, 162.15) * mm, "end": v(-185.36, 161.13) * mm});
            skLineSegment(sketch, "E1038", {"start": v(-185.36, 161.13) * mm, "end": v(-185.41, 159.97) * mm});
            skLineSegment(sketch, "E1039", {"start": v(-185.41, 159.97) * mm, "end": v(-186.22, 158.9) * mm});
            skLineSegment(sketch, "E1040", {"start": v(-186.22, 158.9) * mm, "end": v(-187.44, 158.19) * mm});
            skLineSegment(sketch, "E1041", {"start": v(-187.44, 158.19) * mm, "end": v(-189.07, 158.04) * mm});
            skLineSegment(sketch, "E1042", {"start": v(-189.07, 158.04) * mm, "end": v(-191, 158.4) * mm});
            skLineSegment(sketch, "E1043", {"start": v(-191, 158.4) * mm, "end": v(-192.47, 159.3) * mm});
            skLineSegment(sketch, "E1044", {"start": v(-192.47, 159.3) * mm, "end": v(-193.38, 160.88) * mm});
            skLineSegment(sketch, "E1045", {"start": v(-193.38, 160.88) * mm, "end": v(-193.58, 161.74) * mm});
            skLineSegment(sketch, "E1046", {"start": v(-193.58, 161.74) * mm, "end": v(-197.49, 161.39) * mm});
            skLineSegment(sketch, "E1047", {"start": v(-224.67, 174.37) * mm, "end": v(-225.57, 174.67) * mm});
            skLineSegment(sketch, "E1048", {"start": v(-225.57, 174.67) * mm, "end": v(-227.07, 174.87) * mm});
            skLineSegment(sketch, "E1049", {"start": v(-227.07, 174.87) * mm, "end": v(-228.47, 174.97) * mm});
            skLineSegment(sketch, "E1050", {"start": v(-228.47, 174.97) * mm, "end": v(-236.87, 174.97) * mm});
            skLineSegment(sketch, "E1051", {"start": v(-236.87, 174.97) * mm, "end": v(-236.87, 154.97) * mm});
            skLineSegment(sketch, "E1052", {"start": v(-236.87, 154.97) * mm, "end": v(-232.87, 154.97) * mm});
            skLineSegment(sketch, "E1053", {"start": v(-232.87, 154.97) * mm, "end": v(-232.87, 171.57) * mm});
            skLineSegment(sketch, "E1054", {"start": v(-232.87, 171.57) * mm, "end": v(-228.57, 171.57) * mm});
            skLineSegment(sketch, "E1055", {"start": v(-228.57, 171.57) * mm, "end": v(-227.57, 171.37) * mm});
            skLineSegment(sketch, "E1056", {"start": v(-227.57, 171.37) * mm, "end": v(-226.77, 170.97) * mm});
            skLineSegment(sketch, "E1057", {"start": v(-226.77, 170.97) * mm, "end": v(-226.17, 170.37) * mm});
            skLineSegment(sketch, "E1058", {"start": v(-226.17, 170.37) * mm, "end": v(-225.87, 169.77) * mm});
            skLineSegment(sketch, "E1059", {"start": v(-223.74, 154.97) * mm, "end": v(-228.98, 162.57) * mm});
            skLineSegment(sketch, "E1060", {"start": v(-204.77, 163.02) * mm, "end": v(-204.9, 161.3) * mm});
            skLineSegment(sketch, "E1061", {"start": v(-204.9, 161.3) * mm, "end": v(-205.26, 159.57) * mm});
            skLineSegment(sketch, "E1062", {"start": v(-205.26, 159.57) * mm, "end": v(-206.16, 158.69) * mm});
            skLineSegment(sketch, "E1063", {"start": v(-206.16, 158.69) * mm, "end": v(-207.36, 158.17) * mm});
            skLineSegment(sketch, "E1064", {"start": v(-207.36, 158.17) * mm, "end": v(-208.8, 158.07) * mm});
            skLineSegment(sketch, "E1065", {"start": v(-208.8, 158.07) * mm, "end": v(-210.3, 158.32) * mm});
            skLineSegment(sketch, "E1066", {"start": v(-210.3, 158.32) * mm, "end": v(-211.52, 159.05) * mm});
            skLineSegment(sketch, "E1067", {"start": v(-211.52, 159.05) * mm, "end": v(-212.33, 160.28) * mm});
            skLineSegment(sketch, "E1068", {"start": v(-212.33, 160.28) * mm, "end": v(-212.65, 162.18) * mm});
            skLineSegment(sketch, "E1069", {"start": v(-212.65, 162.18) * mm, "end": v(-212.62, 170.14) * mm});
            skLineSegment(sketch, "E1070", {"start": v(-212.62, 170.14) * mm, "end": v(-212.62, 174.96) * mm});
            skLineSegment(sketch, "E1071", {"start": v(-212.62, 174.96) * mm, "end": v(-216.67, 174.97) * mm});
            skLineSegment(sketch, "E1072", {"start": v(-179.93, 154.94) * mm, "end": v(-172.06, 174.89) * mm});
            skLineSegment(sketch, "E1073", {"start": v(-186.63, 166.87) * mm, "end": v(-190.18, 167.78) * mm});
            skLineSegment(sketch, "E1074", {"start": v(-190.18, 167.78) * mm, "end": v(-192.52, 168.8) * mm});
            skLineSegment(sketch, "E1075", {"start": v(-192.52, 168.8) * mm, "end": v(-192.82, 169.7) * mm});
            skLineSegment(sketch, "E1076", {"start": v(-192.82, 169.7) * mm, "end": v(-192.82, 170.47) * mm});
            skLineSegment(sketch, "E1077", {"start": v(-192.82, 170.47) * mm, "end": v(-192.35, 171.18) * mm});
            skLineSegment(sketch, "E1078", {"start": v(-192.35, 171.18) * mm, "end": v(-191.5, 171.68) * mm});
            skLineSegment(sketch, "E1079", {"start": v(-191.5, 171.68) * mm, "end": v(-190.47, 171.94) * mm});
            skLineSegment(sketch, "E1080", {"start": v(-190.47, 171.94) * mm, "end": v(-189.09, 172) * mm});
            skLineSegment(sketch, "E1081", {"start": v(-189.09, 172) * mm, "end": v(-187.8, 171.8) * mm});
            skLineSegment(sketch, "E1082", {"start": v(-187.8, 171.8) * mm, "end": v(-186.65, 171.15) * mm});
            skLineSegment(sketch, "E1083", {"start": v(-186.65, 171.15) * mm, "end": v(-186.12, 170.3) * mm});
            skLineSegment(sketch, "E1084", {"start": v(-186.12, 170.3) * mm, "end": v(-185.83, 169) * mm});
            skLineSegment(sketch, "E1085", {"start": v(-185.83, 169) * mm, "end": v(-181.76, 169.25) * mm});
            skLineSegment(sketch, "E1086", {"start": v(-183.28, 173.21) * mm, "end": v(-184.85, 174.33) * mm});
            skLineSegment(sketch, "E1087", {"start": v(-184.85, 174.33) * mm, "end": v(-186.88, 175.09) * mm});
            skLineSegment(sketch, "E1088", {"start": v(-186.88, 175.09) * mm, "end": v(-189.01, 175.24) * mm});
            skLineSegment(sketch, "E1089", {"start": v(-189.01, 175.24) * mm, "end": v(-190.69, 175.24) * mm});
            skLineSegment(sketch, "E1090", {"start": v(-190.69, 175.24) * mm, "end": v(-193.33, 174.63) * mm});
            skLineSegment(sketch, "E1091", {"start": v(-193.33, 174.63) * mm, "end": v(-195.2, 173.47) * mm});
            skLineSegment(sketch, "E1092", {"start": v(-195.2, 173.47) * mm, "end": v(-196.42, 171.64) * mm});
            skLineSegment(sketch, "E1093", {"start": v(-196.42, 171.64) * mm, "end": v(-196.83, 170.32) * mm});
            skLineSegment(sketch, "E1094", {"start": v(-196.83, 170.32) * mm, "end": v(-196.63, 168.34) * mm});
            skLineSegment(sketch, "E1095", {"start": v(-196.63, 168.34) * mm, "end": v(-195.81, 166.56) * mm});
            skLineSegment(sketch, "E1096", {"start": v(-195.81, 166.56) * mm, "end": v(-194.4, 165.3) * mm});
            skLineSegment(sketch, "E1097", {"start": v(-194.4, 165.3) * mm, "end": v(-191.55, 164.03) * mm});
            skLineSegment(sketch, "E1098", {"start": v(-213.33, 155.56) * mm, "end": v(-211.6, 154.93) * mm});
            skLineSegment(sketch, "E1099", {"start": v(-211.6, 154.93) * mm, "end": v(-208.98, 154.58) * mm});
            skLineSegment(sketch, "E1100", {"start": v(-208.98, 154.58) * mm, "end": v(-206.36, 154.78) * mm});
            skLineSegment(sketch, "E1101", {"start": v(-206.36, 154.78) * mm, "end": v(-204.25, 155.44) * mm});
            skLineSegment(sketch, "E1102", {"start": v(-204.25, 155.44) * mm, "end": v(-202.93, 156.3) * mm});
            skLineSegment(sketch, "E1103", {"start": v(-202.93, 156.3) * mm, "end": v(-201.78, 157.42) * mm});
            skLineSegment(sketch, "E1104", {"start": v(-201.78, 157.42) * mm, "end": v(-201.05, 159.47) * mm});
            skLineSegment(sketch, "E1105", {"start": v(-201.05, 159.47) * mm, "end": v(-200.7, 162.23) * mm});
            skLineSegment(sketch, "E1106", {"start": v(-200.7, 162.23) * mm, "end": v(-200.7, 166.15) * mm});
            skLineSegment(sketch, "E1107", {"start": v(-200.7, 166.15) * mm, "end": v(-200.73, 174.96) * mm});
            skLineSegment(sketch, "E1108", {"start": v(-200.73, 174.96) * mm, "end": v(-204.8, 174.96) * mm});
            skLineSegment(sketch, "E1109", {"start": v(-204.8, 174.96) * mm, "end": v(-204.77, 163.02) * mm});
            skLineSegment(sketch, "E1110", {"start": v(-246.17, 171.37) * mm, "end": v(-245.37, 170.97) * mm});
            skLineSegment(sketch, "E1111", {"start": v(-245.37, 170.97) * mm, "end": v(-244.77, 170.37) * mm});
            skLineSegment(sketch, "E1112", {"start": v(-244.77, 170.37) * mm, "end": v(-244.47, 169.77) * mm});
            skLineSegment(sketch, "E1113", {"start": v(-244.47, 169.77) * mm, "end": v(-244.27, 168.97) * mm});
            skLineSegment(sketch, "E1114", {"start": v(-244.27, 168.97) * mm, "end": v(-244.37, 168.07) * mm});
            skLineSegment(sketch, "E1115", {"start": v(-244.37, 168.07) * mm, "end": v(-244.77, 167.27) * mm});
            skLineSegment(sketch, "E1116", {"start": v(-244.77, 167.27) * mm, "end": v(-245.27, 166.67) * mm});
            skLineSegment(sketch, "E1117", {"start": v(-245.27, 166.67) * mm, "end": v(-246.17, 166.17) * mm});
            skLineSegment(sketch, "E1118", {"start": v(-246.17, 166.17) * mm, "end": v(-247.07, 165.97) * mm});
            skLineSegment(sketch, "E1119", {"start": v(-247.07, 165.97) * mm, "end": v(-248.37, 165.97) * mm});
            skLineSegment(sketch, "E1120", {"start": v(-248.37, 165.97) * mm, "end": v(-249.97, 165.97) * mm});
            skLineSegment(sketch, "E1121", {"start": v(-241.97, 173.47) * mm, "end": v(-243.27, 174.37) * mm});
            skLineSegment(sketch, "E1122", {"start": v(-243.27, 174.37) * mm, "end": v(-244.17, 174.67) * mm});
            skLineSegment(sketch, "E1123", {"start": v(-244.17, 174.67) * mm, "end": v(-245.67, 174.87) * mm});
            skLineSegment(sketch, "E1124", {"start": v(-245.67, 174.87) * mm, "end": v(-247.07, 174.97) * mm});
            skLineSegment(sketch, "E1125", {"start": v(-247.07, 174.97) * mm, "end": v(-255.47, 174.97) * mm});
            skLineSegment(sketch, "E1126", {"start": v(-225.87, 169.77) * mm, "end": v(-225.67, 168.97) * mm});
            skLineSegment(sketch, "E1127", {"start": v(-225.67, 168.97) * mm, "end": v(-225.77, 168.07) * mm});
            skLineSegment(sketch, "E1128", {"start": v(-225.77, 168.07) * mm, "end": v(-226.17, 167.27) * mm});
            skLineSegment(sketch, "E1129", {"start": v(-226.17, 167.27) * mm, "end": v(-226.67, 166.67) * mm});
            skLineSegment(sketch, "E1130", {"start": v(-226.67, 166.67) * mm, "end": v(-227.57, 166.17) * mm});
            skLineSegment(sketch, "E1131", {"start": v(-227.57, 166.17) * mm, "end": v(-228.47, 165.97) * mm});
            skLineSegment(sketch, "E1132", {"start": v(-228.47, 165.97) * mm, "end": v(-229.77, 165.97) * mm});
            skLineSegment(sketch, "E1133", {"start": v(-172.06, 174.89) * mm, "end": v(-167.8, 174.89) * mm});
            skLineSegment(sketch, "E1134", {"start": v(-167.8, 174.89) * mm, "end": v(-159.88, 155) * mm});
            skLineSegment(sketch, "E1135", {"start": v(-159.88, 155) * mm, "end": v(-164.2, 155.04) * mm});
            skLineSegment(sketch, "E1136", {"start": v(-179.93, 154.94) * mm, "end": v(-175.57, 154.94) * mm});
            skLineSegment(sketch, "E1137", {"start": v(-175.57, 154.94) * mm, "end": v(-170.03, 170.22) * mm});
            skLineSegment(sketch, "E1138", {"start": v(-170.03, 170.22) * mm, "end": v(-167.24, 162.9) * mm});
            skLineSegment(sketch, "E1139", {"start": v(-167.24, 162.9) * mm, "end": v(-171.6, 162.86) * mm});
            skLineSegment(sketch, "E1140", {"start": v(-171.6, 162.86) * mm, "end": v(-172.77, 159.56) * mm});
            skLineSegment(sketch, "E1141", {"start": v(-172.77, 159.56) * mm, "end": v(-165.92, 159.56) * mm});
            skLineSegment(sketch, "E1142", {"start": v(-165.92, 159.56) * mm, "end": v(-164.2, 155.04) * mm});
            skLineSegment(sketch, "E1143", {"start": v(-181.76, 169.25) * mm, "end": v(-182.16, 171.23) * mm});
            skLineSegment(sketch, "E1144", {"start": v(-182.16, 171.23) * mm, "end": v(-183.28, 173.21) * mm});
            skLineSegment(sketch, "E1145", {"start": v(-197.49, 161.39) * mm, "end": v(-196.88, 159.1) * mm});
            skLineSegment(sketch, "E1146", {"start": v(-196.88, 159.1) * mm, "end": v(-195.4, 156.72) * mm});
            skLineSegment(sketch, "E1147", {"start": v(-195.4, 156.72) * mm, "end": v(-192.92, 155.2) * mm});
            skLineSegment(sketch, "E1148", {"start": v(-192.92, 155.2) * mm, "end": v(-190.28, 154.64) * mm});
            skLineSegment(sketch, "E1149", {"start": v(-190.28, 154.64) * mm, "end": v(-187.75, 154.74) * mm});
            skLineSegment(sketch, "E1150", {"start": v(-187.75, 154.74) * mm, "end": v(-184.45, 155.55) * mm});
            skLineSegment(sketch, "E1151", {"start": v(-184.45, 155.55) * mm, "end": v(-182.32, 157.43) * mm});
            skLineSegment(sketch, "E1152", {"start": v(-182.32, 157.43) * mm, "end": v(-181.3, 159.36) * mm});
            skLineSegment(sketch, "E1153", {"start": v(-181.3, 159.36) * mm, "end": v(-181.3, 161.9) * mm});
            skLineSegment(sketch, "E1154", {"start": v(-181.3, 161.9) * mm, "end": v(-182.01, 163.92) * mm});
            skLineSegment(sketch, "E1155", {"start": v(-182.01, 163.92) * mm, "end": v(-183.63, 165.7) * mm});
            skLineSegment(sketch, "E1156", {"start": v(-183.63, 165.7) * mm, "end": v(-186.63, 166.87) * mm});
            skLineSegment(sketch, "E1157", {"start": v(-249.97, 165.97) * mm, "end": v(-249.97, 162.57) * mm});
            skLineSegment(sketch, "E1158", {"start": v(-249.97, 162.57) * mm, "end": v(-247.07, 162.57) * mm});
            skLineSegment(sketch, "E1159", {"start": v(-247.07, 162.57) * mm, "end": v(-245.37, 162.67) * mm});
            skLineSegment(sketch, "E1160", {"start": v(-245.37, 162.67) * mm, "end": v(-243.37, 163.27) * mm});
            skLineSegment(sketch, "E1161", {"start": v(-243.37, 163.27) * mm, "end": v(-241.87, 164.27) * mm});
            skLineSegment(sketch, "E1162", {"start": v(-241.87, 164.27) * mm, "end": v(-240.97, 165.37) * mm});
            skLineSegment(sketch, "E1163", {"start": v(-240.97, 165.37) * mm, "end": v(-240.37, 166.67) * mm});
            skLineSegment(sketch, "E1164", {"start": v(-240.37, 166.67) * mm, "end": v(-240.17, 167.97) * mm});
            skLineSegment(sketch, "E1165", {"start": v(-240.17, 167.97) * mm, "end": v(-240.17, 169.67) * mm});
            skLineSegment(sketch, "E1166", {"start": v(-240.17, 169.67) * mm, "end": v(-240.47, 171.17) * mm});
            skLineSegment(sketch, "E1167", {"start": v(-240.47, 171.17) * mm, "end": v(-241.17, 172.47) * mm});
            skLineSegment(sketch, "E1168", {"start": v(-241.17, 172.47) * mm, "end": v(-241.97, 173.47) * mm});
            skLineSegment(sketch, "E1169", {"start": v(-223.74, 154.97) * mm, "end": v(-218.86, 154.97) * mm});
            skLineSegment(sketch, "E1170", {"start": v(-218.86, 154.97) * mm, "end": v(-223.04, 161.62) * mm});
            skLineSegment(sketch, "E1171", {"start": v(-223.04, 161.62) * mm, "end": v(-224, 162.58) * mm});
            skLineSegment(sketch, "E1172", {"start": v(-224, 162.58) * mm, "end": v(-224.77, 163.27) * mm});
            skLineSegment(sketch, "E1173", {"start": v(-231.37, 162.57) * mm, "end": v(-228.98, 162.57) * mm});
            skLineSegment(sketch, "E1174", {"start": v(-216.67, 174.97) * mm, "end": v(-216.71, 163.98) * mm});
            skLineSegment(sketch, "E1175", {"start": v(-216.71, 163.98) * mm, "end": v(-216.5, 160.36) * mm});
            skLineSegment(sketch, "E1176", {"start": v(-216.5, 160.36) * mm, "end": v(-216.1, 158.7) * mm});
            skLineSegment(sketch, "E1177", {"start": v(-216.1, 158.7) * mm, "end": v(-215.51, 157.5) * mm});
            skLineSegment(sketch, "E1178", {"start": v(-215.51, 157.5) * mm, "end": v(-214.58, 156.4) * mm});
            skLineSegment(sketch, "E1179", {"start": v(-214.58, 156.4) * mm, "end": v(-213.33, 155.56) * mm});
            skLineSegment(sketch, "E1180", {"start": v(-229.77, 165.97) * mm, "end": v(-231.37, 165.97) * mm});
            skLineSegment(sketch, "E1181", {"start": v(-231.37, 165.97) * mm, "end": v(-231.37, 162.57) * mm});
            skLineSegment(sketch, "E1182", {"start": v(-224.77, 163.27) * mm, "end": v(-223.27, 164.27) * mm});
            skLineSegment(sketch, "E1183", {"start": v(-223.27, 164.27) * mm, "end": v(-222.37, 165.37) * mm});
            skLineSegment(sketch, "E1184", {"start": v(-222.37, 165.37) * mm, "end": v(-221.77, 166.67) * mm});
            skLineSegment(sketch, "E1185", {"start": v(-221.77, 166.67) * mm, "end": v(-221.57, 167.97) * mm});
            skLineSegment(sketch, "E1186", {"start": v(-221.57, 167.97) * mm, "end": v(-221.57, 169.67) * mm});
            skLineSegment(sketch, "E1187", {"start": v(-221.57, 169.67) * mm, "end": v(-221.87, 171.17) * mm});
            skLineSegment(sketch, "E1188", {"start": v(-221.87, 171.17) * mm, "end": v(-222.57, 172.47) * mm});
            skLineSegment(sketch, "E1189", {"start": v(-222.57, 172.47) * mm, "end": v(-223.37, 173.47) * mm});
            skLineSegment(sketch, "E1190", {"start": v(-223.37, 173.47) * mm, "end": v(-224.67, 174.37) * mm});
            skLineSegment(sketch, "E1191", {"start": v(-255.47, 174.97) * mm, "end": v(-255.47, 154.97) * mm});
            skLineSegment(sketch, "E1192", {"start": v(-255.47, 154.97) * mm, "end": v(-251.47, 154.97) * mm});
            skLineSegment(sketch, "E1193", {"start": v(-251.47, 154.97) * mm, "end": v(-251.47, 171.57) * mm});
            skLineSegment(sketch, "E1194", {"start": v(-251.47, 171.57) * mm, "end": v(-247.17, 171.57) * mm});
            skLineSegment(sketch, "E1195", {"start": v(-247.17, 171.57) * mm, "end": v(-246.17, 171.37) * mm});
            skLineSegment(sketch, "E1196", {"start": v(-215.47, -151.03) * mm, "end": v(-215.47, -165.1) * mm});
            skLineSegment(sketch, "E1197", {"start": v(-205.47, -165.1) * mm, "end": v(-205.47, -151.03) * mm});
            skLineSegment(sketch, "E1198", {"start": v(-215.47, -151.03) * mm, "end": v(-215.47, -150.03) * mm});
            skLineSegment(sketch, "E1199", {"start": v(-205.47, -150.03) * mm, "end": v(-200.47, -145.03) * mm});
            skLineSegment(sketch, "E1200", {"start": v(-205.47, -151.03) * mm, "end": v(-205.47, -150.03) * mm});
            skLineSegment(sketch, "E1201", {"start": v(-45.47, -151.03) * mm, "end": v(-45.47, -165.1) * mm});
            skLineSegment(sketch, "E1202", {"start": v(-35.47, -165.1) * mm, "end": v(-35.47, -151.03) * mm});
            skLineSegment(sketch, "E1203", {"start": v(-45.47, -150.03) * mm, "end": v(-50.47, -145.03) * mm});
            skLineSegment(sketch, "E1204", {"start": v(-45.47, -151.03) * mm, "end": v(-45.47, -150.03) * mm});
            skLineSegment(sketch, "E1205", {"start": v(-35.47, -151.03) * mm, "end": v(-35.47, -150.03) * mm});
            skLineSegment(sketch, "E1206", {"start": v(-230.47, -145.03) * mm, "end": v(-220.47, -145.03) * mm});
            skLineSegment(sketch, "E1207", {"start": v(-220.47, -145.03) * mm, "end": v(-215.47, -150.03) * mm});
            skLineSegment(sketch, "E1208", {"start": v(-20.47, -145.03) * mm, "end": v(-30.47, -145.03) * mm});
            skLineSegment(sketch, "E1209", {"start": v(-35.47, -150.03) * mm, "end": v(-30.47, -145.03) * mm});
            skCircle(sketch, "E1210", {"center": v(29.54, -145.04) * mm, "radius": 1.8 * mm});
            skCircle(sketch, "E1211", {"center": v(49.52, -145.09) * mm, "radius": 1.8 * mm});
            skCircle(sketch, "E1212", {"center": v(39.53, -165.06) * mm, "radius": 1.8 * mm});
            skCircle(sketch, "E1213", {"center": v(16.53, -160.03) * mm, "radius": 1.8 * mm});
            skCircle(sketch, "E1214", {"center": v(-290.5, -165.02) * mm, "radius": 1.8 * mm});
            skCircle(sketch, "E1215", {"center": v(-267.49, -160.02) * mm, "radius": 1.8 * mm});
            skCircle(sketch, "E1216", {"center": v(-280.49, -145.01) * mm, "radius": 1.8 * mm});
            skCircle(sketch, "E1217", {"center": v(-300.5, -145.01) * mm, "radius": 1.8 * mm});
            skArc(sketch, "E1218", {"start": v(-215.47, -165.1) * mm, "mid": v(-210.47, -170.04) * mm, "end": v(-205.47, -165.1) * mm});
            skArc(sketch, "E1219", {"start": v(-45.47, -165.1) * mm, "mid": v(-40.47, -170.04) * mm, "end": v(-35.47, -165.1) * mm});
            skCircle(sketch, "E1220", {"center": v(-245.05, -74.52) * mm, "radius": 1.8 * mm});
            skCircle(sketch, "E1221", {"center": v(-36.03, -74.54) * mm, "radius": 1.8 * mm});
            skCircle(sketch, "E1222", {"center": v(-45.54, 29.97) * mm, "radius": 1.5 * mm});
            skCircle(sketch, "E1223", {"center": v(-65.54, 29.97) * mm, "radius": 1.5 * mm});
            skCircle(sketch, "E1224", {"center": v(-140.5, 49.95) * mm, "radius": 1.8 * mm});
            skCircle(sketch, "E1225", {"center": v(-140.5, 8.97) * mm, "radius": 1.8 * mm});
            skCircle(sketch, "E1226", {"center": v(-215.54, -5.03) * mm, "radius": 1.5 * mm});
            skCircle(sketch, "E1227", {"center": v(-235.54, -5.03) * mm, "radius": 1.5 * mm});
            skCircle(sketch, "E1228", {"center": v(-215.54, 64.97) * mm, "radius": 1.5 * mm});
            skCircle(sketch, "E1229", {"center": v(-245.05, 134.48) * mm, "radius": 1.8 * mm});
            skCircle(sketch, "E1230", {"center": v(-36.03, 134.48) * mm, "radius": 1.8 * mm});
            skCircle(sketch, "E1231", {"center": v(-267.45, -0.03) * mm, "radius": 1.8 * mm});
            skCircle(sketch, "E1232", {"center": v(-267.45, 154.96) * mm, "radius": 1.8 * mm});
            skCircle(sketch, "E1233", {"center": v(-280.45, 174.98) * mm, "radius": 1.8 * mm});
            skCircle(sketch, "E1234", {"center": v(-300.47, 174.98) * mm, "radius": 1.8 * mm});
            skCircle(sketch, "E1235", {"center": v(16.54, 154.96) * mm, "radius": 1.8 * mm});
            skCircle(sketch, "E1236", {"center": v(29.53, 174.96) * mm, "radius": 1.8 * mm});
            skCircle(sketch, "E1237", {"center": v(49.5, 175) * mm, "radius": 1.8 * mm});
            skCircle(sketch, "E1238", {"center": v(16.53, -0.03) * mm, "radius": 1.8 * mm});
            skCircle(sketch, "E1239", {"center": v(9.53, -179.03) * mm, "radius": 1.8 * mm});
            skCircle(sketch, "E1240", {"center": v(-80.47, -179.03) * mm, "radius": 1.8 * mm});
            skCircle(sketch, "E1241", {"center": v(-170.47, -179.03) * mm, "radius": 1.8 * mm});
            skCircle(sketch, "E1242", {"center": v(-260.47, -179.03) * mm, "radius": 1.8 * mm});
            skPoint(sketch, "E1243", {"position": v(16.53, -143.88) * mm});
            skPoint(sketch, "E1243.positionSnap0", {"position": v(16.53, -139.38) * mm});
            skPoint(sketch, "E1243.positionSnap1", {"position": v(19.78, -143.88) * mm});
            skPoint(sketch, "E1244", {"position": v(16.53, 171.21) * mm});
            skPoint(sketch, "E1244.positionSnap0", {"position": v(13.28, 171.21) * mm});
            skPoint(sketch, "E1244.positionSnap1", {"position": v(16.53, 175.71) * mm});
            skPoint(sketch, "E1245", {"position": v(-267.47, 171.21) * mm});
            skPoint(sketch, "E1245.positionSnap0", {"position": v(-267.47, 175.71) * mm});
            skPoint(sketch, "E1245.positionSnap1", {"position": v(-270.72, 171.21) * mm});
            skPoint(sketch, "E1246", {"position": v(-267.47, -143.88) * mm});
            skPoint(sketch, "E1246.positionSnap0", {"position": v(-267.47, -148.38) * mm});
            skPoint(sketch, "E1246.positionSnap1", {"position": v(-264.22, -143.88) * mm});
            skSolve(sketch);
        }
        {
            var Q0;
            Q0=makeQuery(id+"F0.imprint","IMPRINT",FACE,{"disambiguationData":[TD([[makeQuery(id+"F0.imprint","IMPRINT",EDGE,{"derivedFrom":sQuery(id+"F0.wireOp",EDGE,"E0")}),-1.0]])]});
            var Q1;
            Q1=sQuery(id+"F0.wireOp",EDGE,"E925");
            var Q2;
            Q2=sQuery(id+"F0.wireOp",EDGE,"E914");
            var Q3;
            Q3=sQuery(id+"F0.wireOp",EDGE,"E938");
            var Q4;
            Q4=sQuery(id+"F0.wireOp",EDGE,"E911");
            var Q5;
            Q5=sQuery(id+"F0.wireOp",EDGE,"E928");
            var Q6;
            Q6=sQuery(id+"F0.wireOp",EDGE,"E900");
            var Q7;
            Q7=sQuery(id+"F0.wireOp",EDGE,"E888");
            var Q8;
            Q8=sQuery(id+"F0.wireOp",EDGE,"E831");
            var Q9;
            Q9=sQuery(id+"F0.wireOp",EDGE,"E942");
            var Q10;
            Q10=sQuery(id+"F0.wireOp",EDGE,"E949");
            var Q11;
            Q11=sQuery(id+"F0.wireOp",EDGE,"E944");
            var Q12;
            Q12=sQuery(id+"F0.wireOp",EDGE,"E951");
            var Q13;
            Q13=sQuery(id+"F0.wireOp",EDGE,"E935");
            var Q14;
            Q14=sQuery(id+"F0.wireOp",EDGE,"E5");
            var Q15;
            Q15=sQuery(id+"F0.wireOp",EDGE,"E4");
            var Q16;
            Q16=sQuery(id+"F0.wireOp",EDGE,"E3");
            var Q17;
            Q17=sQuery(id+"F0.wireOp",EDGE,"E957");
            var Q18;
            Q18=sQuery(id+"F0.wireOp",EDGE,"E948");
            var Q19;
            Q19=sQuery(id+"F0.wireOp",EDGE,"E932");
            var Q20;
            Q20=sQuery(id+"F0.wireOp",EDGE,"E909");
            var Q21;
            Q21=sQuery(id+"F0.wireOp",EDGE,"E887");
            var Q22;
            Q22=sQuery(id+"F0.wireOp",EDGE,"E858");
            var Q23;
            Q23=sQuery(id+"F0.wireOp",EDGE,"E804");
            var Q24;
            Q24=sQuery(id+"F0.wireOp",EDGE,"E880");
            var Q25;
            Q25=sQuery(id+"F0.wireOp",EDGE,"E965");
            var Q26;
            Q26=sQuery(id+"F0.wireOp",EDGE,"E952");
            var Q27;
            Q27=sQuery(id+"F0.wireOp",EDGE,"E936");
            var Q28;
            Q28=sQuery(id+"F0.wireOp",EDGE,"E956");
            var Q29;
            Q29=sQuery(id+"F0.wireOp",EDGE,"E940");
            var Q30;
            Q30=sQuery(id+"F0.wireOp",EDGE,"E947");
            var Q31;
            Q31=sQuery(id+"F0.wireOp",EDGE,"E894");
            var Q32;
            Q32=sQuery(id+"F0.wireOp",EDGE,"E926");
            var Q33;
            Q33=sQuery(id+"F0.wireOp",EDGE,"E882");
            var Q34;
            Q34=sQuery(id+"F0.wireOp",EDGE,"E939");
            var Q35;
            Q35=sQuery(id+"F0.wireOp",EDGE,"E923");
            var Q36;
            Q36=sQuery(id+"F0.wireOp",EDGE,"E917");
            var Q37;
            Q37=sQuery(id+"F0.wireOp",EDGE,"E877");
            var Q38;
            Q38=sQuery(id+"F0.wireOp",EDGE,"E803");
            var Q39;
            Q39=sQuery(id+"F0.wireOp",EDGE,"E922");
            var Q40;
            Q40=sQuery(id+"F0.wireOp",EDGE,"E865");
            var Q41;
            Q41=sQuery(id+"F0.wireOp",EDGE,"E912");
            var Q42;
            Q42=sQuery(id+"F0.wireOp",EDGE,"E895");
            var Q43;
            Q43=sQuery(id+"F0.wireOp",EDGE,"E886");
            var Q44;
            Q44=sQuery(id+"F0.wireOp",EDGE,"E868");
            var Q45;
            Q45=sQuery(id+"F0.wireOp",EDGE,"E853");
            var Q46;
            Q46=sQuery(id+"F0.wireOp",EDGE,"E812");
            var Q47;
            Q47=sQuery(id+"F0.wireOp",EDGE,"E818");
            var Q48;
            Q48=sQuery(id+"F0.wireOp",EDGE,"E943");
            var Q49;
            Q49=sQuery(id+"F0.wireOp",EDGE,"E950");
            var Q50;
            Q50=sQuery(id+"F0.wireOp",EDGE,"E2");
            var Q51;
            Q51=sQuery(id+"F0.wireOp",EDGE,"E857");
            var Q52;
            Q52=sQuery(id+"F0.wireOp",EDGE,"E815");
            var Q53;
            Q53=sQuery(id+"F0.wireOp",EDGE,"E933");
            var Q54;
            Q54=sQuery(id+"F0.wireOp",EDGE,"E817");
            var Q55;
            Q55=sQuery(id+"F0.wireOp",EDGE,"E835");
            var Q56;
            Q56=sQuery(id+"F0.wireOp",EDGE,"E953");
            var Q57;
            Q57=sQuery(id+"F0.wireOp",EDGE,"E836");
            var Q58;
            Q58=sQuery(id+"F0.wireOp",EDGE,"E955");
            var Q59;
            Q59=sQuery(id+"F0.wireOp",EDGE,"E946");
            var Q60;
            Q60=sQuery(id+"F0.wireOp",EDGE,"E816");
            var Q61;
            Q61=sQuery(id+"F0.wireOp",EDGE,"E934");
            var Q62;
            Q62=sQuery(id+"F0.wireOp",EDGE,"E954");
            var Q63;
            Q63=sQuery(id+"F0.wireOp",EDGE,"E30");
            var Q64;
            Q64=sQuery(id+"F0.wireOp",EDGE,"E958");
            var Q65;
            Q65=sQuery(id+"F0.wireOp",EDGE,"E1033");
            var Q66;
            Q66=sQuery(id+"F0.wireOp",EDGE,"E805");
            var Q67;
            Q67=sQuery(id+"F0.wireOp",EDGE,"E941");
            var Q68;
            Q68=sQuery(id+"F0.wireOp",EDGE,"E837");
            var Q69;
            Q69=sQuery(id+"F0.wireOp",EDGE,"E937");
            var Q70;
            Q70=sQuery(id+"F0.wireOp",EDGE,"E821");
            var Q71;
            Q71=sQuery(id+"F0.wireOp",EDGE,"E7");
            var Q72;
            Q72=sQuery(id+"F0.wireOp",EDGE,"E6");
            var Q73;
            Q73=sQuery(id+"F0.wireOp",EDGE,"E1");
            var Q74;
            Q74=sQuery(id+"F0.wireOp",EDGE,"E0");
            var Q75;
            Q75=sQuery(id+"F0.wireOp",EDGE,"E872");
            var Q76;
            Q76=sQuery(id+"F0.wireOp",EDGE,"E806");
            var Q77;
            Q77=sQuery(id+"F0.wireOp",EDGE,"E1034");
            var Q78;
            Q78=sQuery(id+"F0.wireOp",EDGE,"E820");
            var Q79;
            Q79=sQuery(id+"F0.wireOp",EDGE,"E918");
            var Q80;
            Q80=sQuery(id+"F0.wireOp",EDGE,"E876");
            var Q81;
            Q81=sQuery(id+"F0.wireOp",EDGE,"E920");
            var Q82;
            Q82=sQuery(id+"F0.wireOp",EDGE,"E819");
            var Q83;
            Q83=sQuery(id+"F0.wireOp",EDGE,"E811");
            var Q84;
            Q84=sQuery(id+"F0.wireOp",EDGE,"E885");
            var Q85;
            Q85=sQuery(id+"F0.wireOp",EDGE,"E921");
            var Q86;
            Q86=sQuery(id+"F0.wireOp",EDGE,"E913");
            var Q87;
            Q87=sQuery(id+"F0.wireOp",EDGE,"E851");
            var Q88;
            Q88=sQuery(id+"F0.wireOp",EDGE,"E907");
            var Q89;
            Q89=sQuery(id+"F0.wireOp",EDGE,"E871");
            var Q90;
            Q90=sQuery(id+"F0.wireOp",EDGE,"E834");
            var Q91;
            Q91=sQuery(id+"F0.wireOp",EDGE,"E862");
            var Q92;
            Q92=sQuery(id+"F0.wireOp",EDGE,"E1023");
            var Q93;
            Q93=sQuery(id+"F0.wireOp",EDGE,"E982");
            var Q94;
            Q94=sQuery(id+"F0.wireOp",EDGE,"E974");
            var Q95;
            Q95=sQuery(id+"F0.wireOp",EDGE,"E961");
            var Q96;
            Q96=sQuery(id+"F0.wireOp",EDGE,"E833");
            var Q97;
            Q97=sQuery(id+"F0.wireOp",EDGE,"E861");
            var Q98;
            Q98=sQuery(id+"F0.wireOp",EDGE,"E924");
            var Q99;
            Q99=sQuery(id+"F0.wireOp",EDGE,"E1032");
            var Q100;
            Q100=sQuery(id+"F0.wireOp",EDGE,"E969");
            var Q101;
            Q101=sQuery(id+"F0.wireOp",EDGE,"E981");
            var Q102;
            Q102=sQuery(id+"F0.wireOp",EDGE,"E884");
            var Q103;
            Q103=sQuery(id+"F0.wireOp",EDGE,"E878");
            var Q104;
            Q104=sQuery(id+"F0.wireOp",EDGE,"E850");
            var Q105;
            Q105=sQuery(id+"F0.wireOp",EDGE,"E870");
            var Q106;
            Q106=sQuery(id+"F0.wireOp",EDGE,"E1028");
            var Q107;
            Q107=sQuery(id+"F0.wireOp",EDGE,"E968");
            var Q108;
            Q108=sQuery(id+"F0.wireOp",EDGE,"E988");
            var Q109;
            Q109=sQuery(id+"F0.wireOp",EDGE,"E980");
            var Q110;
            Q110=sQuery(id+"F0.wireOp",EDGE,"E822");
            var Q111;
            Q111=sQuery(id+"F0.wireOp",EDGE,"E866");
            var Q112;
            Q112=sQuery(id+"F0.wireOp",EDGE,"E1025");
            var Q113;
            Q113=sQuery(id+"F0.wireOp",EDGE,"E810");
            var Q114;
            Q114=sQuery(id+"F0.wireOp",EDGE,"E931");
            var Q115;
            Q115=sQuery(id+"F0.wireOp",EDGE,"E849");
            var Q116;
            Q116=sQuery(id+"F0.wireOp",EDGE,"E869");
            var Q117;
            Q117=sQuery(id+"F0.wireOp",EDGE,"E905");
            var Q118;
            Q118=sQuery(id+"F0.wireOp",EDGE,"E832");
            var Q119;
            Q119=sQuery(id+"F0.wireOp",EDGE,"E875");
            var Q120;
            Q120=sQuery(id+"F0.wireOp",EDGE,"E1027");
            var Q121;
            Q121=sQuery(id+"F0.wireOp",EDGE,"E979");
            var Q122;
            Q122=sQuery(id+"F0.wireOp",EDGE,"E967");
            var Q123;
            Q123=sQuery(id+"F0.wireOp",EDGE,"E883");
            var Q124;
            Q124=sQuery(id+"F0.wireOp",EDGE,"E908");
            var Q125;
            Q125=sQuery(id+"F0.wireOp",EDGE,"E919");
            var Q126;
            Q126=sQuery(id+"F0.wireOp",EDGE,"E809");
            var Q127;
            Q127=sQuery(id+"F0.wireOp",EDGE,"E848");
            var Q128;
            Q128=sQuery(id+"F0.wireOp",EDGE,"E881");
            var Q129;
            Q129=sQuery(id+"F0.wireOp",EDGE,"E826");
            var Q130;
            Q130=sQuery(id+"F0.wireOp",EDGE,"E903");
            var Q131;
            Q131=sQuery(id+"F0.wireOp",EDGE,"E840");
            var Q132;
            Q132=sQuery(id+"F0.wireOp",EDGE,"E874");
            var Q133;
            Q133=sQuery(id+"F0.wireOp",EDGE,"E966");
            var Q134;
            Q134=sQuery(id+"F0.wireOp",EDGE,"E978");
            var Q135;
            Q135=sQuery(id+"F0.wireOp",EDGE,"cdc0a224-aea8-41c6-a81f-871d923c7d92");
            var Q136;
            Q136=sQuery(id+"F0.wireOp",EDGE,"E893");
            var Q137;
            Q137=sQuery(id+"F0.wireOp",EDGE,"bc39cccc-46bb-4995-b1c6-2d97363e9930");
            var Q138;
            Q138=sQuery(id+"F0.wireOp",EDGE,"E838");
            var Q139;
            Q139=sQuery(id+"F0.wireOp",EDGE,"E844");
            var Q140;
            Q140=sQuery(id+"F0.wireOp",EDGE,"43ff72d7-fdd7-47b5-8dc7-33902472c25b");
            var Q141;
            Q141=sQuery(id+"F0.wireOp",EDGE,"9a1018fb-7509-48c5-9983-983c4e2f5393");
            var Q142;
            Q142=sQuery(id+"F0.wireOp",EDGE,"312ed6c2-6fb5-4807-85d1-3ac4b1190a24");
            var Q143;
            Q143=sQuery(id+"F0.wireOp",EDGE,"E1017");
            var Q144;
            Q144=sQuery(id+"F0.wireOp",EDGE,"c983bd9c-7af0-4034-918c-bd9357f90098");
            var Q145;
            Q145=sQuery(id+"F0.wireOp",EDGE,"E1001");
            var Q146;
            Q146=sQuery(id+"F0.wireOp",EDGE,"E962");
            var Q147;
            Q147=sQuery(id+"F0.wireOp",EDGE,"e36aca62-5309-4241-a6a4-e7c9d19b2996");
            var Q148;
            Q148=sQuery(id+"F0.wireOp",EDGE,"b2061277-c1e9-47e3-8b0b-c7ee70998474");
            var Q149;
            Q149=sQuery(id+"F0.wireOp",EDGE,"472061d3-1b85-4f8c-91b7-9786c5c18222");
            var Q150;
            Q150=sQuery(id+"F0.wireOp",EDGE,"E1005");
            var Q151;
            Q151=sQuery(id+"F0.wireOp",EDGE,"E986");
            var Q152;
            Q152=sQuery(id+"F0.wireOp",EDGE,"E830");
            var Q153;
            Q153=sQuery(id+"F0.wireOp",EDGE,"E964");
            var Q154;
            Q154=sQuery(id+"F0.wireOp",EDGE,"E976");
            var Q155;
            Q155=sQuery(id+"F0.wireOp",EDGE,"E1022");
            var Q156;
            Q156=sQuery(id+"F0.wireOp",EDGE,"E1009");
            var Q157;
            Q157=sQuery(id+"F0.wireOp",EDGE,"6d931976-14f4-42fa-a9cf-b36e56378210");
            var Q158;
            Q158=sQuery(id+"F0.wireOp",EDGE,"E902");
            var Q159;
            Q159=sQuery(id+"F0.wireOp",EDGE,"29d0a25d-e4a0-4b36-a27e-578b47d1bdb7");
            var Q160;
            Q160=sQuery(id+"F0.wireOp",EDGE,"b1ade15e-ac78-4de9-8870-3ebd057eae47");
            var Q161;
            Q161=sQuery(id+"F0.wireOp",EDGE,"E890");
            var Q162;
            Q162=sQuery(id+"F0.wireOp",EDGE,"E927");
            var Q163;
            Q163=sQuery(id+"F0.wireOp",EDGE,"E906");
            var Q164;
            Q164=sQuery(id+"F0.wireOp",EDGE,"E846");
            var Q165;
            Q165=sQuery(id+"F0.wireOp",EDGE,"099a45de-8323-4931-8ac2-2f65142ab7f5");
            var Q166;
            Q166=sQuery(id+"F0.wireOp",EDGE,"fa67e3ec-6e7e-4efd-9874-503e8d5aa896");
            var Q167;
            Q167=sQuery(id+"F0.wireOp",EDGE,"cbbc4eb4-0ef0-4003-91c5-345c761bc047");
            var Q168;
            Q168=sQuery(id+"F0.wireOp",EDGE,"E864");
            var Q169;
            Q169=sQuery(id+"F0.wireOp",EDGE,"E1031");
            var Q170;
            Q170=sQuery(id+"F0.wireOp",EDGE,"E855");
            var Q171;
            Q171=sQuery(id+"F0.wireOp",EDGE,"E1029");
            var Q172;
            Q172=sQuery(id+"F0.wireOp",EDGE,"5f8e1ba7-8a23-4369-a411-7742abd484a9");
            var Q173;
            Q173=sQuery(id+"F0.wireOp",EDGE,"E1015");
            var Q174;
            Q174=sQuery(id+"F0.wireOp",EDGE,"E1004");
            var Q175;
            Q175=sQuery(id+"F0.wireOp",EDGE,"E960");
            var Q176;
            Q176=sQuery(id+"F0.wireOp",EDGE,"E973");
            var Q177;
            Q177=sQuery(id+"F0.wireOp",EDGE,"71c39cb7-5196-4dc6-ab58-8d6bdb40f9c6");
            var Q178;
            Q178=sQuery(id+"F0.wireOp",EDGE,"E916");
            var Q179;
            Q179=sQuery(id+"F0.wireOp",EDGE,"E842");
            var Q180;
            Q180=sQuery(id+"F0.wireOp",EDGE,"E813");
            var Q181;
            Q181=sQuery(id+"F0.wireOp",EDGE,"E860");
            var Q182;
            Q182=sQuery(id+"F0.wireOp",EDGE,"e863e419-e6b4-4ea0-b17f-5765d6024846");
            var Q183;
            Q183=sQuery(id+"F0.wireOp",EDGE,"e8690d2a-224f-4857-bd98-dc8a85aa94e4");
            var Q184;
            Q184=sQuery(id+"F0.wireOp",EDGE,"E1020");
            var Q185;
            Q185=sQuery(id+"F0.wireOp",EDGE,"E1007");
            var Q186;
            Q186=sQuery(id+"F0.wireOp",EDGE,"E987");
            var Q187;
            Q187=sQuery(id+"F0.wireOp",EDGE,"E998");
            var Q188;
            Q188=sQuery(id+"F0.wireOp",EDGE,"E972");
            var Q189;
            Q189=sQuery(id+"F0.wireOp",EDGE,"E852");
            var Q190;
            Q190=sQuery(id+"F0.wireOp",EDGE,"E897");
            var Q191;
            Q191=sQuery(id+"F0.wireOp",EDGE,"E863");
            var Q192;
            Q192=sQuery(id+"F0.wireOp",EDGE,"E825");
            var Q193;
            Q193=sQuery(id+"F0.wireOp",EDGE,"83cc3bc7-c428-4e94-ac31-b6e446562241");
            var Q194;
            Q194=sQuery(id+"F0.wireOp",EDGE,"E879");
            var Q195;
            Q195=sQuery(id+"F0.wireOp",EDGE,"54a5e1ec-1ecf-47fa-89bc-6a71472cd95e");
            var Q196;
            Q196=sQuery(id+"F0.wireOp",EDGE,"E1024");
            var Q197;
            Q197=sQuery(id+"F0.wireOp",EDGE,"E904");
            var Q198;
            Q198=sQuery(id+"F0.wireOp",EDGE,"E824");
            var Q199;
            Q199=sQuery(id+"F0.wireOp",EDGE,"E1002");
            var Q200;
            Q200=sQuery(id+"F0.wireOp",EDGE,"E983");
            var Q201;
            Q201=sQuery(id+"F0.wireOp",EDGE,"E827");
            var Q202;
            Q202=sQuery(id+"F0.wireOp",EDGE,"bbe12b69-1339-4445-98e5-bc8a7c76dc8a");
            var Q203;
            Q203=sQuery(id+"F0.wireOp",EDGE,"ff9602f2-77e2-4368-987a-6285d16a0c96");
            var Q204;
            Q204=sQuery(id+"F0.wireOp",EDGE,"0c64cd33-312b-416a-89a1-1da72ed71bd0");
            var Q205;
            Q205=sQuery(id+"F0.wireOp",EDGE,"c449b056-d35f-4f2e-a958-e9bf5da80a05");
            var Q206;
            Q206=sQuery(id+"F0.wireOp",EDGE,"f9394eab-178f-45c5-897e-ce77d937d24f");
            var Q207;
            Q207=sQuery(id+"F0.wireOp",EDGE,"a060e41b-989e-4451-ae43-0cfb2c1e98f5");
            var Q208;
            Q208=sQuery(id+"F0.wireOp",EDGE,"E867");
            var Q209;
            Q209=sQuery(id+"F0.wireOp",EDGE,"7a0d2995-c34d-4865-b9f3-07111121c4c4");
            var Q210;
            Q210=sQuery(id+"F0.wireOp",EDGE,"6d369d4c-ed45-4b99-8ca1-fbd43ed49f33");
            var Q211;
            Q211=sQuery(id+"F0.wireOp",EDGE,"72bba3b3-873d-447f-a342-fed4d893cd13");
            var Q212;
            Q212=sQuery(id+"F0.wireOp",EDGE,"bae28338-ddd6-4c6a-b9f6-02485098fde6");
            var Q213;
            Q213=sQuery(id+"F0.wireOp",EDGE,"d4c4c522-f95f-47e7-a99d-0df94f2807e5");
            var Q214;
            Q214=sQuery(id+"F0.wireOp",EDGE,"d9a67787-17b4-47ce-a9c6-cfeb8296acf9");
            var Q215;
            Q215=sQuery(id+"F0.wireOp",EDGE,"e5bf8433-dc89-4e04-81ee-7a8bb34c6838");
            var Q216;
            Q216=sQuery(id+"F0.wireOp",EDGE,"825093fd-8aa2-44ec-8f70-d18631b84c55");
            var Q217;
            Q217=sQuery(id+"F0.wireOp",EDGE,"5d2047ff-9164-452d-9cb9-88a478ec0fa3");
            var Q218;
            Q218=sQuery(id+"F0.wireOp",EDGE,"47876a35-bffe-4eb6-baaa-d4c3d486001d");
            var Q219;
            Q219=sQuery(id+"F0.wireOp",EDGE,"9ad84fa8-761a-443f-b740-1985d570915a");
            var Q220;
            Q220=sQuery(id+"F0.wireOp",EDGE,"6ec50b46-1b64-4e3d-b857-da350ce8e41d");
            var Q221;
            Q221=sQuery(id+"F0.wireOp",EDGE,"62cac10d-e5b1-4951-998b-e049fa1455c4");
            var Q222;
            Q222=sQuery(id+"F0.wireOp",EDGE,"512e75ab-63a2-4055-a3c7-f23ede31a562");
            var Q223;
            Q223=sQuery(id+"F0.wireOp",EDGE,"b739928d-7f18-4173-94c2-834139890039");
            var Q224;
            Q224=sQuery(id+"F0.wireOp",EDGE,"0b9ec59e-cc14-48af-a710-f9976c519150");
            var Q225;
            Q225=sQuery(id+"F0.wireOp",EDGE,"5deb0e7e-419e-4f0d-a7a9-13f0747407a0");
            var Q226;
            Q226=sQuery(id+"F0.wireOp",EDGE,"e1296081-e6fe-45e2-8fa3-eea8bf72fa41");
            var Q227;
            Q227=sQuery(id+"F0.wireOp",EDGE,"b9f2806e-95a8-45a6-8ec1-a161dd1ec68a");
            var Q228;
            Q228=sQuery(id+"F0.wireOp",EDGE,"4cf72698-9ecf-4465-9cce-3db976e7d02d");
            var Q229;
            Q229=sQuery(id+"F0.wireOp",EDGE,"c997236b-a306-452c-a95a-fcc6a9c51b76");
            var Q230;
            Q230=sQuery(id+"F0.wireOp",EDGE,"76471b3e-ed4f-4709-b69d-5cdf395d66fe");
            var Q231;
            Q231=sQuery(id+"F0.wireOp",EDGE,"b0d9f231-a6e8-4934-be0e-59488f2b0fa8");
            var Q232;
            Q232=sQuery(id+"F0.wireOp",EDGE,"4097a8aa-f8a1-448f-8927-2fffd177a227");
            var Q233;
            Q233=sQuery(id+"F0.wireOp",EDGE,"E843");
            var Q234;
            Q234=sQuery(id+"F0.wireOp",EDGE,"b1a72132-80b2-4fcc-943e-6907f23ef3dc");
            var Q235;
            Q235=sQuery(id+"F0.wireOp",EDGE,"E984");
            var Q236;
            Q236=sQuery(id+"F0.wireOp",EDGE,"06fed679-c378-4324-974f-901c71e4a27d");
            var Q237;
            Q237=sQuery(id+"F0.wireOp",EDGE,"2503f15e-fea5-4a69-b3a0-f0f7379b1eb2");
            var Q238;
            Q238=sQuery(id+"F0.wireOp",EDGE,"a2face15-2e22-416f-bc70-2698bcba3738");
            var Q239;
            Q239=sQuery(id+"F0.wireOp",EDGE,"da935abc-0fc6-41ad-a00a-e9e7717a88ad");
            var Q240;
            Q240=sQuery(id+"F0.wireOp",EDGE,"E1000");
            var Q241;
            Q241=sQuery(id+"F0.wireOp",EDGE,"b379f1f5-1bad-4337-affb-4b34963f9315");
            var Q242;
            Q242=sQuery(id+"F0.wireOp",EDGE,"7e499759-eef9-4783-a56c-cff78a9e3abc");
            var Q243;
            Q243=sQuery(id+"F0.wireOp",EDGE,"E1021");
            var Q244;
            Q244=sQuery(id+"F0.wireOp",EDGE,"E1008");
            var Q245;
            Q245=sQuery(id+"F0.wireOp",EDGE,"1a04b766-c9a5-48b2-8ae5-41076a6c997e");
            var Q246;
            Q246=sQuery(id+"F0.wireOp",EDGE,"E892");
            var Q247;
            Q247=sQuery(id+"F0.wireOp",EDGE,"322cda39-e27f-47c0-a6bc-b5473caf3b12");
            var Q248;
            Q248=sQuery(id+"F0.wireOp",EDGE,"E1018");
            var Q249;
            Q249=sQuery(id+"F0.wireOp",EDGE,"d3c9d076-696d-4f37-8d5a-000095cdc5d9");
            var Q250;
            Q250=sQuery(id+"F0.wireOp",EDGE,"574fa6f7-6ba7-4809-a873-41cd5075c195");
            var Q251;
            Q251=sQuery(id+"F0.wireOp",EDGE,"eae9e281-cfbd-481d-a72b-a17e7f3f8396");
            var Q252;
            Q252=sQuery(id+"F0.wireOp",EDGE,"E823");
            var Q253;
            Q253=sQuery(id+"F0.wireOp",EDGE,"3347e06c-3686-4eb5-9ad0-f2956d319f7b");
            var Q254;
            Q254=sQuery(id+"F0.wireOp",EDGE,"E1003");
            var Q255;
            Q255=sQuery(id+"F0.wireOp",EDGE,"ff4ffe44-eb2f-4a67-9829-d30d49ef5e2a");
            var Q256;
            Q256=sQuery(id+"F0.wireOp",EDGE,"94aba077-545a-4114-b0de-c06442fa6d05");
            var Q257;
            Q257=sQuery(id+"F0.wireOp",EDGE,"E985");
            var Q258;
            Q258=sQuery(id+"F0.wireOp",EDGE,"E977");
            var Q259;
            Q259=sQuery(id+"F0.wireOp",EDGE,"68a75019-cdc5-482e-bdab-0989c7975d1f");
            var Q260;
            Q260=sQuery(id+"F0.wireOp",EDGE,"4625a7d6-32b5-4c13-9cc2-4be30836bec0");
            var Q261;
            Q261=sQuery(id+"F0.wireOp",EDGE,"8df6b744-6bf7-4631-b5a1-4e5a65822869");
            var Q262;
            Q262=sQuery(id+"F0.wireOp",EDGE,"E829");
            var Q263;
            Q263=sQuery(id+"F0.wireOp",EDGE,"0287ac27-b1aa-43dd-8d99-8c5cee18e590");
            var Q264;
            Q264=sQuery(id+"F0.wireOp",EDGE,"42f5cbc7-aa84-4dbf-8367-f227c23708ba");
            var Q265;
            Q265=sQuery(id+"F0.wireOp",EDGE,"2bbe2262-2074-4fc3-a78f-68f10f7271c7");
            var Q266;
            Q266=sQuery(id+"F0.wireOp",EDGE,"E1030");
            var Q267;
            Q267=sQuery(id+"F0.wireOp",EDGE,"d6f7bc65-4a59-4f4d-8b18-00a0f1c0727b");
            var Q268;
            Q268=sQuery(id+"F0.wireOp",EDGE,"E1014");
            var Q269;
            Q269=sQuery(id+"F0.wireOp",EDGE,"E901");
            var Q270;
            Q270=sQuery(id+"F0.wireOp",EDGE,"2c7db86f-f387-471c-9791-867d9fdabf95");
            var Q271;
            Q271=sQuery(id+"F0.wireOp",EDGE,"E889");
            var Q272;
            Q272=sQuery(id+"F0.wireOp",EDGE,"E845");
            var Q273;
            Q273=sQuery(id+"F0.wireOp",EDGE,"E854");
            var Q274;
            Q274=sQuery(id+"F0.wireOp",EDGE,"609a37af-97ff-4365-b039-f565c52880ca");
            var Q275;
            Q275=sQuery(id+"F0.wireOp",EDGE,"c2140cea-6f73-493d-b4ad-d5984a63a3f7");
            var Q276;
            Q276=sQuery(id+"F0.wireOp",EDGE,"92ec2daa-221f-479b-a102-8d12d0d9b9bb");
            var Q277;
            Q277=sQuery(id+"F0.wireOp",EDGE,"bd7edcda-c087-4c16-815e-04a7961a16dc");
            var Q278;
            Q278=sQuery(id+"F0.wireOp",EDGE,"0895a20b-ebc3-44c2-88b5-9414cf76fb1c");
            var Q279;
            Q279=sQuery(id+"F0.wireOp",EDGE,"E915");
            var Q280;
            Q280=sQuery(id+"F0.wireOp",EDGE,"E841");
            var Q281;
            Q281=sQuery(id+"F0.wireOp",EDGE,"E963");
            var Q282;
            Q282=sQuery(id+"F0.wireOp",EDGE,"baf83a39-2ee5-4bd8-84a4-7186442840e7");
            var Q283;
            Q283=sQuery(id+"F0.wireOp",EDGE,"E959");
            var Q284;
            Q284=sQuery(id+"F0.wireOp",EDGE,"E859");
            var Q285;
            Q285=sQuery(id+"F0.wireOp",EDGE,"E1026");
            var Q286;
            Q286=sQuery(id+"F0.wireOp",EDGE,"E1013");
            var Q287;
            Q287=sQuery(id+"F0.wireOp",EDGE,"a1e67bd4-0821-4104-a0f2-3aa55e58fcb5");
            var Q288;
            Q288=sQuery(id+"F0.wireOp",EDGE,"E971");
            var Q289;
            Q289=sQuery(id+"F0.wireOp",EDGE,"962c5001-3d36-4d51-bb1e-a1e731ce15f7");
            var Q290;
            Q290=sQuery(id+"F0.wireOp",EDGE,"E945");
            var Q291;
            Q291=sQuery(id+"F0.wireOp",EDGE,"8e4a2f44-10bf-4950-a08c-941d8413bbf2");
            var Q292;
            Q292=sQuery(id+"F0.wireOp",EDGE,"c9618bfa-b404-436b-ad41-d31a25e11c55");
            var Q293;
            Q293=sQuery(id+"F0.wireOp",EDGE,"ad80cf75-1c2f-46aa-88a1-5ee16af714ee");
            var Q294;
            Q294=sQuery(id+"F0.wireOp",EDGE,"e8c1205a-5a77-4fd1-9301-6a95dbff5f1c");
            var Q295;
            Q295=sQuery(id+"F0.wireOp",EDGE,"E1006");
            var Q296;
            Q296=sQuery(id+"F0.wireOp",EDGE,"2771b44c-2e19-4826-b9d2-e3c3cc3c9675");
            var Q297;
            Q297=sQuery(id+"F0.wireOp",EDGE,"a821aa22-c915-4f13-a428-b72c5fd355c7");
            var Q298;
            Q298=sQuery(id+"F0.wireOp",EDGE,"5dc678d2-1053-44bf-a139-d94a8a6ad452");
            var Q299;
            Q299=sQuery(id+"F0.wireOp",EDGE,"8bf1d2ba-fd2b-48d2-bf5c-46e33ca34b55");
            var Q300;
            Q300=sQuery(id+"F0.wireOp",EDGE,"29ab85e9-d642-4a3a-a5e4-723f07f29d2a");
            var Q301;
            Q301=sQuery(id+"F0.wireOp",EDGE,"f4cadf86-af98-408b-8f87-9aa1b2f3a70c");
            var Q302;
            Q302=sQuery(id+"F0.wireOp",EDGE,"e4792239-90e6-4d6b-b65c-8a9bc76ea7e6");
            var Q303;
            Q303=sQuery(id+"F0.wireOp",EDGE,"ce387b29-bb8f-4fc7-b2a1-2ab5daa77b03");
            var Q304;
            Q304=sQuery(id+"F0.wireOp",EDGE,"db43410d-95d9-4df2-b210-1cb29ee2706c");
            var Q305;
            Q305=sQuery(id+"F0.wireOp",EDGE,"962e4d56-84b2-4428-9969-9f8ccd511e50");
            var Q306;
            Q306=sQuery(id+"F0.wireOp",EDGE,"eb7b9c8b-a3f1-428e-8edd-b146506a69b7");
            var Q307;
            Q307=sQuery(id+"F0.wireOp",EDGE,"01adead8-caab-4bd5-b094-2681d1e0e05c");
            var Q308;
            Q308=sQuery(id+"F0.wireOp",EDGE,"e60e44eb-0b74-4a1c-8386-9dcced35d97c");
            var Q309;
            Q309=sQuery(id+"F0.wireOp",EDGE,"0444f39a-ffc6-4234-9f76-a907715c76f7");
            var Q310;
            Q310=sQuery(id+"F0.wireOp",EDGE,"1898346c-e4c7-486e-916f-2e7f4a387cd6");
            var Q311;
            Q311=sQuery(id+"F0.wireOp",EDGE,"66ed40d4-8dc9-4648-bee7-e5e4e7dd7e9b");
            var Q312;
            Q312=sQuery(id+"F0.wireOp",EDGE,"9dccb327-35f5-4ac2-8b7d-8d81f978e2c1");
            var Q313;
            Q313=sQuery(id+"F0.wireOp",EDGE,"5777fa3e-7bb5-47b9-ac10-615e4ea5d59d");
            var Q314;
            Q314=sQuery(id+"F0.wireOp",EDGE,"8009bce4-192d-49b4-a337-6950730249ba");
            var Q315;
            Q315=sQuery(id+"F0.wireOp",EDGE,"09230063-8580-4e24-a287-6f2da9dbbf0f");
            var Q316;
            Q316=sQuery(id+"F0.wireOp",EDGE,"dc91e3a6-d7d9-40f3-80de-3a6bfaabbb9d");
            var Q317;
            Q317=sQuery(id+"F0.wireOp",EDGE,"a4c23b64-05f9-4ef3-a80f-bd60344bfe29");
            var Q318;
            Q318=sQuery(id+"F0.wireOp",EDGE,"f590e5ea-0877-439a-b6c0-cbd4b1aa47b3");
            var Q319;
            Q319=sQuery(id+"F0.wireOp",EDGE,"E930");
            var Q320;
            Q320=sQuery(id+"F0.wireOp",EDGE,"fe0454da-1e97-4748-aa08-4f6f4616a8b3");
            var Q321;
            Q321=sQuery(id+"F0.wireOp",EDGE,"0ee439c5-e576-43cc-9564-91bf15b2f0fd");
            var Q322;
            Q322=sQuery(id+"F0.wireOp",EDGE,"944ea9ee-5563-404e-8b09-fbb085500a0e");
            var Q323;
            Q323=sQuery(id+"F0.wireOp",EDGE,"697fe53e-25cd-4641-899a-709ec1092e21");
            var Q324;
            Q324=sQuery(id+"F0.wireOp",EDGE,"E873");
            var Q325;
            Q325=sQuery(id+"F0.wireOp",EDGE,"5eb74230-47f2-466b-9c8d-72e358125a43");
            var Q326;
            Q326=sQuery(id+"F0.wireOp",EDGE,"5e39a1cb-6b71-4dda-a2a0-18214ba4fc21");
            var Q327;
            Q327=sQuery(id+"F0.wireOp",EDGE,"14d3b580-9a93-4046-998e-70edd759602c");
            var Q328;
            Q328=sQuery(id+"F0.wireOp",EDGE,"288657c2-08e3-4bd5-b65e-4a861e63620c");
            var Q329;
            Q329=sQuery(id+"F0.wireOp",EDGE,"260f5ce1-0fb5-42ce-83ab-60cfa753a113");
            var Q330;
            Q330=sQuery(id+"F0.wireOp",EDGE,"334cb1f4-53b9-4fff-8bd9-cdc899bf692d");
            var Q331;
            Q331=sQuery(id+"F0.wireOp",EDGE,"E999");
            var Q332;
            Q332=sQuery(id+"F0.wireOp",EDGE,"E808");
            var Q333;
            Q333=sQuery(id+"F0.wireOp",EDGE,"144c2dc0-3634-41d5-bae4-fb9a6429f866");
            var Q334;
            Q334=sQuery(id+"F0.wireOp",EDGE,"0ffb3c8c-acd7-4940-bff6-8103a661c58b");
            var Q335;
            Q335=sQuery(id+"F0.wireOp",EDGE,"9dc785f0-25bf-423e-95f9-5c680652c30b");
            var Q336;
            Q336=sQuery(id+"F0.wireOp",EDGE,"422afe0e-c483-4bd5-958f-d303fff509a8");
            var Q337;
            Q337=sQuery(id+"F0.wireOp",EDGE,"E970");
            var Q338;
            Q338=sQuery(id+"F0.wireOp",EDGE,"f62bf0f7-813d-4fdc-9f0b-19ac61a75c1a");
            var Q339;
            Q339=sQuery(id+"F0.wireOp",EDGE,"ca25e040-1b5d-4877-9178-8d605860d4ed");
            var Q340;
            Q340=sQuery(id+"F0.wireOp",EDGE,"E899");
            var Q341;
            Q341=sQuery(id+"F0.wireOp",EDGE,"2d102040-a846-4325-8181-a7c8054a4ab6");
            var Q342;
            Q342=sQuery(id+"F0.wireOp",EDGE,"a12fe08b-7315-4c05-b842-d1f7bc39658a");
            var Q343;
            Q343=sQuery(id+"F0.wireOp",EDGE,"794285c3-05a8-4859-9dbf-b327305d75b3");
            var Q344;
            Q344=sQuery(id+"F0.wireOp",EDGE,"8fbd2b2f-def5-4bb2-9b99-2850dba940d9");
            var Q345;
            Q345=sQuery(id+"F0.wireOp",EDGE,"c6b047ca-e4c8-495f-a3cc-21cac800a887");
            var Q346;
            Q346=sQuery(id+"F0.wireOp",EDGE,"58701f04-344e-4b87-9c6a-0fcfec83a3ee");
            var Q347;
            Q347=sQuery(id+"F0.wireOp",EDGE,"8229c53b-4803-4d55-8c96-dea8f0ea775d");
            var Q348;
            Q348=sQuery(id+"F0.wireOp",EDGE,"3ac4a822-6ea2-4749-bd48-6e8364794825");
            var Q349;
            Q349=sQuery(id+"F0.wireOp",EDGE,"9c15eda4-8800-4b2d-b753-ccb06505193d");
            var Q350;
            Q350=sQuery(id+"F0.wireOp",EDGE,"4acc60c7-388a-4dc3-ac42-e45b993e9081");
            var Q351;
            Q351=sQuery(id+"F0.wireOp",EDGE,"7504fb77-443d-452d-a50e-72def5781a08");
            var Q352;
            Q352=sQuery(id+"F0.wireOp",EDGE,"f43d0577-76f9-4d7b-89fc-d403f9392459");
            var Q353;
            Q353=sQuery(id+"F0.wireOp",EDGE,"E891");
            var Q354;
            Q354=sQuery(id+"F0.wireOp",EDGE,"a500b31e-5ea3-4658-b31b-6ab24c514578");
            var Q355;
            Q355=sQuery(id+"F0.wireOp",EDGE,"667bc6cb-0bca-4a3b-a9de-d843004ac1f2");
            var Q356;
            Q356=sQuery(id+"F0.wireOp",EDGE,"E847");
            var Q357;
            Q357=sQuery(id+"F0.wireOp",EDGE,"8eda9b34-7263-4f39-b93e-9326c730d5d0");
            var Q358;
            Q358=sQuery(id+"F0.wireOp",EDGE,"E856");
            var Q359;
            Q359=sQuery(id+"F0.wireOp",EDGE,"df3065ab-c28e-43bb-be7b-b37a5f2b5e30");
            var Q360;
            Q360=sQuery(id+"F0.wireOp",EDGE,"8e8442d9-479a-42dc-aa18-399aa399897e");
            var Q361;
            Q361=sQuery(id+"F0.wireOp",EDGE,"d3c7662d-d3dd-4d54-8648-fe943810d137");
            var Q362;
            Q362=sQuery(id+"F0.wireOp",EDGE,"E828");
            var Q363;
            Q363=sQuery(id+"F0.wireOp",EDGE,"74ff2ead-e5c3-4528-8ac3-b6686c5ddf08");
            var Q364;
            Q364=sQuery(id+"F0.wireOp",EDGE,"E975");
            var Q365;
            Q365=sQuery(id+"F0.wireOp",EDGE,"da7f3f3c-af03-43c8-a6e7-d43b24c7f7c1");
            var Q366;
            Q366=sQuery(id+"F0.wireOp",EDGE,"c13d3fb2-5ca2-4450-8b27-90f43d2e407a");
            var Q367;
            Q367=sQuery(id+"F0.wireOp",EDGE,"53936a19-08c9-4d20-b9f8-16be3742736c");
            var Q368;
            Q368=sQuery(id+"F0.wireOp",EDGE,"e89c2fff-b5b3-4877-8d92-0d3eefcffa27");
            var Q369;
            Q369=sQuery(id+"F0.wireOp",EDGE,"8c665c69-41ee-4d2d-b8f3-c2186e4a0584");
            var Q370;
            Q370=sQuery(id+"F0.wireOp",EDGE,"798ba0b1-0cd3-420b-82d7-f4c250af2a17");
            var Q371;
            Q371=sQuery(id+"F0.wireOp",EDGE,"b2616e62-406d-40e4-8c7b-4552a27a096e");
            var Q372;
            Q372=sQuery(id+"F0.wireOp",EDGE,"9351aec0-119b-4154-856a-320406b930db");
            var Q373;
            Q373=sQuery(id+"F0.wireOp",EDGE,"7577e5e3-1ebc-4e34-a30e-19b66d2a4027");
            var Q374;
            Q374=sQuery(id+"F0.wireOp",EDGE,"824f91da-6e62-40ff-9131-d3cf8db559e9");
            var Q375;
            Q375=sQuery(id+"F0.wireOp",EDGE,"6d016c04-86d9-4909-bfd5-871686835899");
            var Q376;
            Q376=sQuery(id+"F0.wireOp",EDGE,"488b71d9-aaa3-41f3-9dab-c114febdabb3");
            var Q377;
            Q377=sQuery(id+"F0.wireOp",EDGE,"E1019");
            var Q378;
            Q378=sQuery(id+"F0.wireOp",EDGE,"b27adb1e-0ad8-47cf-85be-6eaaab53ffed");
            var Q379;
            Q379=sQuery(id+"F0.wireOp",EDGE,"576fe0fb-72e4-4773-b968-bcc8a9823b42");
            var Q380;
            Q380=sQuery(id+"F0.wireOp",EDGE,"249b726a-b8af-489e-9a1d-83cee191e77f");
            var Q381;
            Q381=sQuery(id+"F0.wireOp",EDGE,"7f442ec8-8b06-4776-a0c1-ceaa7d053cb9");
            var Q382;
            Q382=sQuery(id+"F0.wireOp",EDGE,"c3f43872-2e25-426d-9bbb-c56da974beb1");
            var Q383;
            Q383=sQuery(id+"F0.wireOp",EDGE,"76a6b08f-6e62-4b33-b204-411812e5ad29");
            var Q384;
            Q384=sQuery(id+"F0.wireOp",EDGE,"E1010");
            var Q385;
            Q385=sQuery(id+"F0.wireOp",EDGE,"E995");
            var Q386;
            Q386=sQuery(id+"F0.wireOp",EDGE,"E1016");
            var Q387;
            Q387=sQuery(id+"F0.wireOp",EDGE,"27d582e7-14e9-4102-a524-274e76b22159");
            var Q388;
            Q388=sQuery(id+"F0.wireOp",EDGE,"4ce418c3-933e-4631-8a2c-692f15465339");
            var Q389;
            Q389=sQuery(id+"F0.wireOp",EDGE,"19f18548-1ceb-492c-9b99-b0b926571fdc");
            var Q390;
            Q390=sQuery(id+"F0.wireOp",EDGE,"6b22f77d-6811-4f3f-bbb8-f97fe59a24bb");
            var Q391;
            Q391=sQuery(id+"F0.wireOp",EDGE,"ec1f1de5-f2f4-4b79-8117-240645458c7b");
            var Q392;
            Q392=sQuery(id+"F0.wireOp",EDGE,"b8280172-94eb-4a06-9a6b-7bf1fb2692c5");
            var Q393;
            Q393=sQuery(id+"F0.wireOp",EDGE,"ed418bd0-8737-46f3-a725-07382cf5fe16");
            var Q394;
            Q394=sQuery(id+"F0.wireOp",EDGE,"95b5ff18-5fb1-42d5-8d0e-9188ebd57b54");
            var Q395;
            Q395=sQuery(id+"F0.wireOp",EDGE,"E839");
            var Q396;
            Q396=sQuery(id+"F0.wireOp",EDGE,"0462b1a8-ae60-4876-bb23-e7d27baba8b5");
            var Q397;
            Q397=sQuery(id+"F0.wireOp",EDGE,"ab570da4-77a8-40cb-b942-e5b709a26c00");
            var Q398;
            Q398=sQuery(id+"F0.wireOp",EDGE,"5bb571ac-6344-4a70-9319-e8369ee6cdbf");
            var Q399;
            Q399=sQuery(id+"F0.wireOp",EDGE,"b9613d34-02e0-4986-ac00-5444b133e690");
            var Q400;
            Q400=sQuery(id+"F0.wireOp",EDGE,"E994");
            var Q401;
            Q401=sQuery(id+"F0.wireOp",EDGE,"4ead381f-7aae-487b-a4ae-28d807b9e44f");
            var Q402;
            Q402=sQuery(id+"F0.wireOp",EDGE,"55d38448-261e-40d6-b89c-4b759f8821d6");
            var Q403;
            Q403=sQuery(id+"F0.wireOp",EDGE,"65763cf2-b856-49f0-b912-ee49d4150ab0");
            var Q404;
            Q404=sQuery(id+"F0.wireOp",EDGE,"00e3f4b1-1edc-4e9e-ac9a-bc02a6b7f2b4");
            var Q405;
            Q405=sQuery(id+"F0.wireOp",EDGE,"43b25094-7da1-4a93-912a-b2dd187738ea");
            var Q406;
            Q406=sQuery(id+"F0.wireOp",EDGE,"E1012");
            var Q407;
            Q407=sQuery(id+"F0.wireOp",EDGE,"accce7f7-1d05-4107-987e-b21e7e182c8a");
            var Q408;
            Q408=sQuery(id+"F0.wireOp",EDGE,"9624ebfd-bc3d-438b-a005-7d4f84a0f6a1");
            var Q409;
            Q409=sQuery(id+"F0.wireOp",EDGE,"fd42b984-01ed-490c-98c6-19d2c28b9150");
            var Q410;
            Q410=sQuery(id+"F0.wireOp",EDGE,"3711b7d3-dd82-4b83-b370-1c11a62b489a");
            var Q411;
            Q411=sQuery(id+"F0.wireOp",EDGE,"d3b9f2e9-0099-4e5f-974d-8179f7d3def4");
            var Q412;
            Q412=sQuery(id+"F0.wireOp",EDGE,"cf82a6e8-b48c-4aee-959b-edf2f47bd973");
            var Q413;
            Q413=sQuery(id+"F0.wireOp",EDGE,"b04c9a94-077f-4dbe-af55-f5a8fef62fb2");
            var Q414;
            Q414=sQuery(id+"F0.wireOp",EDGE,"E993");
            var Q415;
            Q415=sQuery(id+"F0.wireOp",EDGE,"6831b5af-558b-4b2a-bc8c-14abbc131d31");
            var Q416;
            Q416=sQuery(id+"F0.wireOp",EDGE,"1add2aac-fe33-4b21-a940-2eb45125e954");
            var Q417;
            Q417=sQuery(id+"F0.wireOp",EDGE,"86b7d8a0-2b92-4d84-b4bc-6690516fe7b2");
            var Q418;
            Q418=sQuery(id+"F0.wireOp",EDGE,"d0cc756a-f3e9-460f-8731-c1e943a631e5");
            var Q419;
            Q419=sQuery(id+"F0.wireOp",EDGE,"aaaf1c15-d134-416a-ac3b-f1fd17da8ea7");
            var Q420;
            Q420=sQuery(id+"F0.wireOp",EDGE,"111c2811-3065-4301-863d-0fba40a10008");
            var Q421;
            Q421=sQuery(id+"F0.wireOp",EDGE,"E807");
            var Q422;
            Q422=sQuery(id+"F0.wireOp",EDGE,"72110a64-596f-48fd-a8c1-f2c2006914f2");
            var Q423;
            Q423=sQuery(id+"F0.wireOp",EDGE,"e78ec1bd-2165-4f5e-ae24-297ae42f2223");
            var Q424;
            Q424=sQuery(id+"F0.wireOp",EDGE,"ba71f3a5-f54a-45dc-8a84-c00c16684f82");
            var Q425;
            Q425=sQuery(id+"F0.wireOp",EDGE,"580be2e5-d7a5-42b7-9151-916367c06abf");
            var Q426;
            Q426=sQuery(id+"F0.wireOp",EDGE,"da702d13-d1e6-4f09-ab54-6e6efe085d7a");
            var Q427;
            Q427=sQuery(id+"F0.wireOp",EDGE,"2a229516-efd7-44df-b1fc-3456b3fbba21");
            var Q428;
            Q428=sQuery(id+"F0.wireOp",EDGE,"49441a34-d703-41f0-8eaf-17c93d027547");
            var Q429;
            Q429=sQuery(id+"F0.wireOp",EDGE,"d83767a0-cb18-483f-b3fc-db13c80cb105");
            var Q430;
            Q430=sQuery(id+"F0.wireOp",EDGE,"E992");
            var Q431;
            Q431=sQuery(id+"F0.wireOp",EDGE,"c753922b-bef4-4564-b7e6-cf777146c8cb");
            var Q432;
            Q432=sQuery(id+"F0.wireOp",EDGE,"0ae07f46-b224-438c-84a1-5899bcc70ab1");
            var Q433;
            Q433=sQuery(id+"F0.wireOp",EDGE,"815ad818-d36c-4b1f-9bc9-827c0dffe5d4");
            var Q434;
            Q434=sQuery(id+"F0.wireOp",EDGE,"E814");
            var Q435;
            Q435=sQuery(id+"F0.wireOp",EDGE,"53e0a3f9-b461-41c0-a58e-dc23914a821d");
            var Q436;
            Q436=sQuery(id+"F0.wireOp",EDGE,"56bc0f3f-8ecd-4908-a735-d8e2b2aa5f79");
            var Q437;
            Q437=sQuery(id+"F0.wireOp",EDGE,"09b6fa1e-499d-49bc-9323-418cfc5a36a1");
            var Q438;
            Q438=sQuery(id+"F0.wireOp",EDGE,"E989");
            var Q439;
            Q439=sQuery(id+"F0.wireOp",EDGE,"a8ba6ce4-d652-47e9-9a5d-e343d79b1e8c");
            var Q440;
            Q440=sQuery(id+"F0.wireOp",EDGE,"9df087b0-41a5-4c65-8bca-e863bf3a727a");
            var Q441;
            Q441=sQuery(id+"F0.wireOp",EDGE,"57f98894-d9a2-4f38-862f-5e8a553039ca");
            var Q442;
            Q442=sQuery(id+"F0.wireOp",EDGE,"5724e3f6-ada3-49ec-b8b6-e62c6e324bf6");
            var Q443;
            Q443=sQuery(id+"F0.wireOp",EDGE,"22163893-96d8-45b3-bfc7-b890366f9851");
            var Q444;
            Q444=sQuery(id+"F0.wireOp",EDGE,"E997");
            var Q445;
            Q445=sQuery(id+"F0.wireOp",EDGE,"b0e365f7-9a71-4c75-a489-c81fa5f9cab0");
            var Q446;
            Q446=sQuery(id+"F0.wireOp",EDGE,"E991");
            var Q447;
            Q447=sQuery(id+"F0.wireOp",EDGE,"d37510bd-46f4-413c-87c8-0ba2cd4a6333");
            var Q448;
            Q448=sQuery(id+"F0.wireOp",EDGE,"3bd421ed-c2ac-42a5-b2e0-e2a51bbc301e");
            var Q449;
            Q449=sQuery(id+"F0.wireOp",EDGE,"d8b301e5-287a-4cf0-9b0d-ef2cdf519a13");
            var Q450;
            Q450=sQuery(id+"F0.wireOp",EDGE,"be9fe4ff-a39e-4d29-b50b-6e4054b6fe27");
            var Q451;
            Q451=sQuery(id+"F0.wireOp",EDGE,"2c3caccb-dfe3-4bb8-8d5a-4f0fe1ac84dd");
            var Q452;
            Q452=sQuery(id+"F0.wireOp",EDGE,"517b4d46-a341-4410-a54f-5a08f3fe55b8");
            var Q453;
            Q453=sQuery(id+"F0.wireOp",EDGE,"6ee76791-6987-49d8-8862-ef2f8ae81109");
            var Q454;
            Q454=sQuery(id+"F0.wireOp",EDGE,"7abc97d6-afd9-4ab4-834d-8372ee43eb68");
            var Q455;
            Q455=sQuery(id+"F0.wireOp",EDGE,"f435cfca-cf31-4e59-8c1f-7c4b925fd815");
            var Q456;
            Q456=sQuery(id+"F0.wireOp",EDGE,"e4418318-01eb-430f-98d1-0e757f5d104c");
            var Q457;
            Q457=sQuery(id+"F0.wireOp",EDGE,"9af42774-cfcb-402e-8bb4-c2d0581ec12a");
            var Q458;
            Q458=sQuery(id+"F0.wireOp",EDGE,"E1011");
            var Q459;
            Q459=sQuery(id+"F0.wireOp",EDGE,"09a223a5-4633-493b-a59c-263dee0a1aa9");
            var Q460;
            Q460=sQuery(id+"F0.wireOp",EDGE,"2479478a-da84-4838-844a-079949297298");
            var Q461;
            Q461=sQuery(id+"F0.wireOp",EDGE,"7efebebf-a1da-4aae-af74-b82fd2d2953f");
            var Q462;
            Q462=sQuery(id+"F0.wireOp",EDGE,"b7e441af-f540-47f9-8dca-2c452251cdcb");
            var Q463;
            Q463=sQuery(id+"F0.wireOp",EDGE,"6b096960-5ff1-4e29-99f8-b9d8a9366f81");
            var Q464;
            Q464=sQuery(id+"F0.wireOp",EDGE,"e05d5cc1-1232-46ee-88b3-890b53c53c4a");
            var Q465;
            Q465=sQuery(id+"F0.wireOp",EDGE,"E896");
            var Q466;
            Q466=sQuery(id+"F0.wireOp",EDGE,"b105fd50-2016-4939-8c22-a1aa931629f0");
            var Q467;
            Q467=sQuery(id+"F0.wireOp",EDGE,"c581d4a2-dcf7-4fb2-9cd4-4807128d9b45");
            var Q468;
            Q468=sQuery(id+"F0.wireOp",EDGE,"2b871284-a070-4284-be5d-6eb2a2715021");
            var Q469;
            Q469=sQuery(id+"F0.wireOp",EDGE,"8465a1d2-1c81-410c-98b1-5e66c4747f40");
            var Q470;
            Q470=sQuery(id+"F0.wireOp",EDGE,"51303a86-5447-4b0e-aff4-e5f6b5ea0327");
            var Q471;
            Q471=sQuery(id+"F0.wireOp",EDGE,"bf501977-9729-4758-8af2-76bf67a0fabc");
            var Q472;
            Q472=sQuery(id+"F0.wireOp",EDGE,"E898");
            var Q473;
            Q473=sQuery(id+"F0.wireOp",EDGE,"e9f0beda-055a-4d5c-87c1-949b464e1855");
            var Q474;
            Q474=sQuery(id+"F0.wireOp",EDGE,"828457b8-24cb-42db-9c51-800d6db92909");
            var Q475;
            Q475=sQuery(id+"F0.wireOp",EDGE,"2e0d8273-81fc-4f72-b0f3-8daf22550274");
            var Q476;
            Q476=sQuery(id+"F0.wireOp",EDGE,"d7487c61-654a-4ef3-953a-2680dd1fb559");
            var Q477;
            Q477=sQuery(id+"F0.wireOp",EDGE,"6825f87d-77aa-4121-b49d-a064865198ab");
            var Q478;
            Q478=sQuery(id+"F0.wireOp",EDGE,"ff19a59d-0b08-46ac-94c9-a86ca510f83f");
            var Q479;
            Q479=sQuery(id+"F0.wireOp",EDGE,"E929");
            var Q480;
            Q480=sQuery(id+"F0.wireOp",EDGE,"fd0326dd-568e-4723-830e-b9212018742b");
            var Q481;
            Q481=sQuery(id+"F0.wireOp",EDGE,"3dea49d8-f5aa-4034-b916-9c9fa873e314");
            var Q482;
            Q482=sQuery(id+"F0.wireOp",EDGE,"7a7bf2c0-c343-4467-a23d-57d6c53baf9f");
            var Q483;
            Q483=sQuery(id+"F0.wireOp",EDGE,"c5df3c47-90a9-4e6d-b239-5975d8290d28");
            var Q484;
            Q484=sQuery(id+"F0.wireOp",EDGE,"E990");
            var Q485;
            Q485=sQuery(id+"F0.wireOp",EDGE,"76e0016f-fb3d-498e-a623-4e76cf710045");
            var Q486;
            Q486=sQuery(id+"F0.wireOp",EDGE,"a9d63bf8-2bdc-4b50-8864-1a49c3b61afb");
            var Q487;
            Q487=sQuery(id+"F0.wireOp",EDGE,"E996");
            var Q488;
            Q488=sQuery(id+"F0.wireOp",EDGE,"60bf6f6e-3b62-4edc-bb09-c51b1c2ff835");
            var Q489;
            Q489=sQuery(id+"F0.wireOp",EDGE,"2bee0e97-ceb5-410a-85a7-0fc6854225cf");
            var Q490;
            Q490=sQuery(id+"F0.wireOp",EDGE,"e1ef0c3a-dca7-4e92-b7cd-acff2b52feb4");
            var Q491;
            Q491=sQuery(id+"F0.wireOp",EDGE,"980f7fed-a50b-4e67-8c0c-8745dbfa9a5d");
            var Q492;
            Q492=sQuery(id+"F0.wireOp",EDGE,"203c9b9c-fb45-4296-bd5a-be519bbd3228");
            var Q493;
            Q493=sQuery(id+"F0.wireOp",EDGE,"5259ce18-0b1a-4ec3-bf07-914564c1a3f5");
            var Q494;
            Q494=sQuery(id+"F0.wireOp",EDGE,"3118706d-1e47-476d-b6a5-7393a50af668");
            var Q495;
            Q495=sQuery(id+"F0.wireOp",EDGE,"dd267f34-46b2-4058-913f-2b822de52076");
            var Q496;
            Q496=sQuery(id+"F0.wireOp",EDGE,"2824aa6b-456d-4543-b18a-818bd8823873");
            var Q497;
            Q497=sQuery(id+"F0.wireOp",EDGE,"904985df-6eca-4101-ae62-bd93f6a8fe37");
            var Q498;
            Q498=sQuery(id+"F0.wireOp",EDGE,"8259fe79-1fe7-4242-926b-9f2b6477bd51");
            var Q499;
            Q499=sQuery(id+"F0.wireOp",EDGE,"4b59ea09-b12b-4d2b-b2c6-63f1ad0777d8");
            var Q500;
            Q500=sQuery(id+"F0.wireOp",EDGE,"E910");
            var Q501;
            Q501=sQuery(id+"F0.wireOp",EDGE,"7c40316a-7472-4062-b2ee-550bdde0893f");
            var Q502;
            Q502=sQuery(id+"F0.wireOp",EDGE,"142925ff-f166-49ae-88e3-e020eb0b4309");
            var Q503;
            Q503=sQuery(id+"F0.wireOp",EDGE,"c1ea459c-3bc3-4184-9705-c36a47e096ce");
            var Q504;
            Q504=sQuery(id+"F0.wireOp",EDGE,"e873705b-affc-4d2d-b929-194993f265ca");
            var Q505;
            Q505=sQuery(id+"F0.wireOp",EDGE,"390d4829-1acf-47e7-9232-39c035a6fafd");
            var Q506;
            Q506=sQuery(id+"F0.wireOp",EDGE,"32fe8947-d7f4-4a0d-b4ce-eaee9533c170");
            var Q507;
            Q507=sQuery(id+"F0.wireOp",EDGE,"9b5f61d8-7636-43bd-b426-2898c4dcd077");
            var Q508;
            Q508=sQuery(id+"F0.wireOp",EDGE,"3dfc4098-3366-4e19-ab4f-73be5c954e8b");
            var Q509;
            Q509=sQuery(id+"F0.wireOp",EDGE,"74b22888-ff3c-4930-a957-bcdace39639c");
            var Q510;
            Q510=sQuery(id+"F0.wireOp",EDGE,"9ced5b8b-8811-4711-adcd-9f04695d6aed");
            var Q511;
            Q511=sQuery(id+"F0.wireOp",EDGE,"2fe543ee-8558-46a9-acd8-6118f65fe2fc");
            var Q512;
            Q512=sQuery(id+"F0.wireOp",EDGE,"be848d55-30a1-4e0f-8d9d-ed919b6d0dc0");
            var Q513;
            Q513=sQuery(id+"F0.wireOp",EDGE,"c47f56a4-a907-4588-968d-0000e786967a");
            var Q514;
            Q514=sQuery(id+"F0.wireOp",EDGE,"bb1eab34-1c6b-400e-b9b9-a6ee53b61011");
            var Q515;
            Q515=sQuery(id+"F0.wireOp",EDGE,"30423f99-4825-4a0b-83db-2b0e8aed8b15");
            var Q516;
            Q516=sQuery(id+"F0.wireOp",EDGE,"ea843acf-3952-4d17-968f-18de3df30b27");
            var Q517;
            Q517=sQuery(id+"F0.wireOp",EDGE,"45a0b8bc-94a2-4fca-9d62-12421b70a076");
            var Q518;
            Q518=sQuery(id+"F0.wireOp",EDGE,"23afc704-1b98-4b9b-ab16-23fd8038e32c");
            var Q519;
            Q519=sQuery(id+"F0.wireOp",EDGE,"1a5350ce-675d-40a3-9769-ff05d86d51ae");
            var Q520;
            Q520=sQuery(id+"F0.wireOp",EDGE,"9d9b7622-16d4-45a2-ae40-f113cb7f3c2d");
            var Q521;
            Q521=sQuery(id+"F0.wireOp",EDGE,"1e393b8a-6e36-4e42-8cbe-ae5e1ec57be1");
            var Q522;
            Q522=sQuery(id+"F0.wireOp",EDGE,"f9e22850-cec8-46e1-abb8-c86683553ede");
            var Q523;
            Q523=sQuery(id+"F0.wireOp",EDGE,"faeba22f-dcf6-4559-ba73-911cfb7d3897");
            var Q524;
            Q524=sQuery(id+"F0.wireOp",EDGE,"aaf7d139-f0fd-4339-9928-b454845de16e");
            var Q525;
            Q525=sQuery(id+"F0.wireOp",EDGE,"6256bf15-eb71-441a-9870-c6b32a01288d");
            var Q526;
            Q526=sQuery(id+"F0.wireOp",EDGE,"ad5bb771-e828-4b3e-af76-f8a6327b8f86");
            var Q527;
            Q527=sQuery(id+"F0.wireOp",EDGE,"3508dda7-5464-4e1a-8ae8-8f63d447ffb6");
            var Q528;
            Q528=sQuery(id+"F0.wireOp",EDGE,"3d043524-cf2d-4c1a-a3a4-0282f72d0127");
            var Q529;
            Q529=sQuery(id+"F0.wireOp",EDGE,"4a6fc7f8-9287-48b5-8b2e-cff1def414aa");
            var Q530;
            Q530=sQuery(id+"F0.wireOp",EDGE,"30b7d2c9-a3c1-4ada-931e-289e06e3faa3");
            var Q531;
            Q531=sQuery(id+"F0.wireOp",EDGE,"216235d5-c404-4d47-a80a-a29f500b2eb4");
            var Q532;
            Q532=sQuery(id+"F0.wireOp",EDGE,"35178881-f403-405d-b679-f2186ab3e5a5");
            var Q533;
            Q533=sQuery(id+"F0.wireOp",EDGE,"1c738439-f851-49e8-a5d5-596ffa55766a");
            var Q534;
            Q534=sQuery(id+"F0.wireOp",EDGE,"c8e3ff84-d87c-4e7b-a9eb-6dccf92b7c5f");
            var Q535;
            Q535=sQuery(id+"F0.wireOp",EDGE,"99c5797b-fda6-4118-972f-b170f9e1a903");
            var Q536;
            Q536=sQuery(id+"F0.wireOp",EDGE,"d5fefb1d-2308-4c30-a2df-ddf66d34e0dd");
            var Q537;
            Q537=sQuery(id+"F0.wireOp",EDGE,"f98baf39-a972-40b3-824f-76d43d1f0077");
            extrude(context, id + "F1", {"entities" : qUnion([Q0]), "surfaceEntities" : qUnion([Q1, Q2, Q3, Q4, Q5, Q6, Q7, Q8, Q9, Q10, Q11, Q12, Q13, Q14, Q15, Q16, Q17, Q18, Q19, Q20, Q21, Q22, Q23, Q24, Q25, Q26, Q27, Q28, Q29, Q30, Q31, Q32, Q33, Q34, Q35, Q36, Q37, Q38, Q39, Q40, Q41, Q42, Q43, Q44, Q45, Q46, Q47, Q48, Q49, Q50, Q51, Q52, Q53, Q54, Q55, Q56, Q57, Q58, Q59, Q60, Q61, Q62, Q63, Q64, Q65, Q66, Q67, Q68, Q69, Q70, Q71, Q72, Q73, Q74, Q75, Q76, Q77, Q78, Q79, Q80, Q81, Q82, Q83, Q84, Q85, Q86, Q87, Q88, Q89, Q90, Q91, Q92, Q93, Q94, Q95, Q96, Q97, Q98, Q99, Q100, Q101, Q102, Q103, Q104, Q105, Q106, Q107, Q108, Q109, Q110, Q111, Q112, Q113, Q114, Q115, Q116, Q117, Q118, Q119, Q120, Q121, Q122, Q123, Q124, Q125, Q126, Q127, Q128, Q129, Q130, Q131, Q132, Q133, Q134, Q135, Q136, Q137, Q138, Q139, Q140, Q141, Q142, Q143, Q144, Q145, Q146, Q147, Q148, Q149, Q150, Q151, Q152, Q153, Q154, Q155, Q156, Q157, Q158, Q159, Q160, Q161, Q162, Q163, Q164, Q165, Q166, Q167, Q168, Q169, Q170, Q171, Q172, Q173, Q174, Q175, Q176, Q177, Q178, Q179, Q180, Q181, Q182, Q183, Q184, Q185, Q186, Q187, Q188, Q189, Q190, Q191, Q192, Q193, Q194, Q195, Q196, Q197, Q198, Q199, Q200, Q201, Q202, Q203, Q204, Q205, Q206, Q207, Q208, Q209, Q210, Q211, Q212, Q213, Q214, Q215, Q216, Q217, Q218, Q219, Q220, Q221, Q222, Q223, Q224, Q225, Q226, Q227, Q228, Q229, Q230, Q231, Q232, Q233, Q234, Q235, Q236, Q237, Q238, Q239, Q240, Q241, Q242, Q243, Q244, Q245, Q246, Q247, Q248, Q249, Q250, Q251, Q252, Q253, Q254, Q255, Q256, Q257, Q258, Q259, Q260, Q261, Q262, Q263, Q264, Q265, Q266, Q267, Q268, Q269, Q270, Q271, Q272, Q273, Q274, Q275, Q276, Q277, Q278, Q279, Q280, Q281, Q282, Q283, Q284, Q285, Q286, Q287, Q288, Q289, Q290, Q291, Q292, Q293, Q294, Q295, Q296, Q297, Q298, Q299, Q300, Q301, Q302, Q303, Q304, Q305, Q306, Q307, Q308, Q309, Q310, Q311, Q312, Q313, Q314, Q315, Q316, Q317, Q318, Q319, Q320, Q321, Q322, Q323, Q324, Q325, Q326, Q327, Q328, Q329, Q330, Q331, Q332, Q333, Q334, Q335, Q336, Q337, Q338, Q339, Q340, Q341, Q342, Q343, Q344, Q345, Q346, Q347, Q348, Q349, Q350, Q351, Q352, Q353, Q354, Q355, Q356, Q357, Q358, Q359, Q360, Q361, Q362, Q363, Q364, Q365, Q366, Q367, Q368, Q369, Q370, Q371, Q372, Q373, Q374, Q375, Q376, Q377, Q378, Q379, Q380, Q381, Q382, Q383, Q384, Q385, Q386, Q387, Q388, Q389, Q390, Q391, Q392, Q393, Q394, Q395, Q396, Q397, Q398, Q399, Q400, Q401, Q402, Q403, Q404, Q405, Q406, Q407, Q408, Q409, Q410, Q411, Q412, Q413, Q414, Q415, Q416, Q417, Q418, Q419, Q420, Q421, Q422, Q423, Q424, Q425, Q426, Q427, Q428, Q429, Q430, Q431, Q432, Q433, Q434, Q435, Q436, Q437, Q438, Q439, Q440, Q441, Q442, Q443, Q444, Q445, Q446, Q447, Q448, Q449, Q450, Q451, Q452, Q453, Q454, Q455, Q456, Q457, Q458, Q459, Q460, Q461, Q462, Q463, Q464, Q465, Q466, Q467, Q468, Q469, Q470, Q471, Q472, Q473, Q474, Q475, Q476, Q477, Q478, Q479, Q480, Q481, Q482, Q483, Q484, Q485, Q486, Q487, Q488, Q489, Q490, Q491, Q492, Q493, Q494, Q495, Q496, Q497, Q498, Q499, Q500, Q501, Q502, Q503, Q504, Q505, Q506, Q507, Q508, Q509, Q510, Q511, Q512, Q513, Q514, Q515, Q516, Q517, Q518, Q519, Q520, Q521, Q522, Q523, Q524, Q525, Q526, Q527, Q528, Q529, Q530, Q531, Q532, Q533, Q534, Q535, Q536, Q537]), "depth" : 6 * mm});
        }
        {
            var Q0;
            Q0=makeQuery(id+"F0.imprint","IMPRINT",FACE,{"disambiguationData":[TD([[makeQuery(id+"F0.imprint","IMPRINT",EDGE,{"derivedFrom":sQuery(id+"F0.wireOp",EDGE,"E8")}),-1.0]])]});
            extrude(context, id + "F2", {"entities" : qUnion([Q0]), "depth" : 6 * mm});
        }
        {
            var Q0;
            Q0=makeQuery(id+"F0.imprint","IMPRINT",FACE,{"disambiguationData":[TD([[makeQuery(id+"F0.imprint","IMPRINT",EDGE,{"derivedFrom":sQuery(id+"F0.wireOp",EDGE,"E136")}),1.0]])]});
            extrude(context, id + "F3", {"entities" : qUnion([Q0]), "depth" : 6 * mm});
        }
        {
            var Q0;
            Q0=makeQuery(id+"F0.imprint","IMPRINT",FACE,{"disambiguationData":[TD([[makeQuery(id+"F0.imprint","IMPRINT",EDGE,{"derivedFrom":sQuery(id+"F0.wireOp",EDGE,"E131")}),1.0]])]});
            extrude(context, id + "F4", {"entities" : qUnion([Q0]), "depth" : 6 * mm});
        }
        {
            var Q0;
            Q0=makeQuery(id+"F1.opExtrude","CAP_EDGE",EDGE,{"disambiguationData":[OSD([sQuery(id+"F0.wireOp",EDGE,"E837")])],"isStart":false});
            cPoint(context, id + "F5", {"entities" : qUnion([Q0]), "parameter" : 0.5});
        }
        {
            var Q0;
            Q0=makeQuery(id+"F1.opExtrude","CAP_EDGE",EDGE,{"disambiguationData":[OSD([sQuery(id+"F0.wireOp",EDGE,"E837")])],"isStart":true});
            cPoint(context, id + "F6", {"entities" : qUnion([Q0]), "parameter" : 0.5});
        }
        {
            var Q0;
            Q0=makeQuery(id+"F1.opExtrude","CAP_EDGE",EDGE,{"disambiguationData":[OSD([sQuery(id+"F0.wireOp",EDGE,"E805")])],"isStart":true});
            cPoint(context, id + "F7", {"entities" : qUnion([Q0]), "parameter" : 0.5});
        }
        {
            var Q0;
            Q0 = qCreatedBy(id + "F5" ,VERTEX);
            var Q1;
            Q1 = qCreatedBy(id + "F6" ,VERTEX);
            var Q2;
            Q2 = qCreatedBy(id + "F7" ,VERTEX);
            cPlane(context, id + "F8", {"entities" : qUnion([Q0, Q1, Q2]), "cplaneType" : CPlaneType.THREE_POINT, "offset" : 25 * mm, "width" : 150 * mm, "height" : 150 * mm});
        }
        {
            var Q0;
            Q0=qCreatedBy(id+"F8.planeOp",FACE);
            var sketch = newSketch(context, id + "F9", { "sketchPlane" : qUnion([Q0])});
            skCircle(sketch, "E1247", {"center": v(225.54, 11.6) * mm, "radius": 7.5 * mm});
            skSolve(sketch);
        }
        {
            var Q0;
            Q0=makeQuery(id+"F1.opExtrude","CAP_EDGE",EDGE,{"disambiguationData":[OSD([sQuery(id+"F0.wireOp",EDGE,"E877")])],"isStart":true});
            cPoint(context, id + "F10", {"entities" : qUnion([Q0]), "parameter" : 0.5});
        }
        {
            var Q0;
            Q0=makeQuery(id+"F1.opExtrude","CAP_EDGE",EDGE,{"disambiguationData":[OSD([sQuery(id+"F0.wireOp",EDGE,"E877")])],"isStart":false});
            cPoint(context, id + "F11", {"entities" : qUnion([Q0]), "parameter" : 0.5});
        }
        {
            var Q0;
            Q0=makeQuery(id+"F1.opExtrude","CAP_EDGE",EDGE,{"disambiguationData":[OSD([sQuery(id+"F0.wireOp",EDGE,"E1033")])],"isStart":true});
            cPoint(context, id + "F12", {"entities" : qUnion([Q0]), "parameter" : 0.5});
        }
        {
            var Q0;
            Q0 = qCreatedBy(id + "F10" ,VERTEX);
            var Q1;
            Q1 = qCreatedBy(id + "F11" ,VERTEX);
            var Q2;
            Q2 = qCreatedBy(id + "F12" ,VERTEX);
            cPlane(context, id + "F13", {"entities" : qUnion([Q0, Q1, Q2]), "cplaneType" : CPlaneType.THREE_POINT, "offset" : 25 * mm, "width" : 150 * mm, "height" : 150 * mm});
        }
        {
            var Q0;
            Q0=qCreatedBy(id+"F13.planeOp",FACE);
            var sketch = newSketch(context, id + "F14", { "sketchPlane" : qUnion([Q0])});
            skCircle(sketch, "E1248", {"center": v(-225.54, 11.6) * mm, "radius": 7.5 * mm});
            skPoint(sketch, "E1248.first.point", {"position": v(-230.54, 6) * mm});
            skPoint(sketch, "E1248.second.point", {"position": v(-220.54, 6) * mm});
            skPoint(sketch, "E1248.third.point", {"position": v(-218.32, 13.61) * mm});
            skSolve(sketch);
        }
        {
            var Q0;
            Q0=makeQuery(id+"F1.opExtrude","CAP_EDGE",EDGE,{"disambiguationData":[OSD([sQuery(id+"F0.wireOp",EDGE,"E965")])],"isStart":true});
            cPoint(context, id + "F15", {"entities" : qUnion([Q0]), "parameter" : 0.5});
        }
        {
            var Q0;
            Q0=makeQuery(id+"F1.opExtrude","CAP_EDGE",EDGE,{"disambiguationData":[OSD([sQuery(id+"F0.wireOp",EDGE,"E965")])],"isStart":false});
            cPoint(context, id + "F16", {"entities" : qUnion([Q0]), "parameter" : 0.5});
        }
        {
            var Q0;
            Q0=makeQuery(id+"F1.opExtrude","CAP_EDGE",EDGE,{"disambiguationData":[OSD([sQuery(id+"F0.wireOp",EDGE,"E914")])],"isStart":true});
            cPoint(context, id + "F17", {"entities" : qUnion([Q0]), "parameter" : 0.5});
        }
        {
            var Q0;
            Q0 = qCreatedBy(id + "F15" ,VERTEX);
            var Q1;
            Q1 = qCreatedBy(id + "F16" ,VERTEX);
            var Q2;
            Q2 = qCreatedBy(id + "F17" ,VERTEX);
            cPlane(context, id + "F18", {"entities" : qUnion([Q0, Q1, Q2]), "cplaneType" : CPlaneType.THREE_POINT, "offset" : 25 * mm, "width" : 150 * mm, "height" : 150 * mm});
        }
        {
            var Q0;
            Q0=qCreatedBy(id+"F18.planeOp",FACE);
            var sketch = newSketch(context, id + "F19", { "sketchPlane" : qUnion([Q0])});
            skCircle(sketch, "E1249", {"center": v(-55.54, 11.6) * mm, "radius": 7.5 * mm});
            skSolve(sketch);
        }
        {
            var Q0;
            Q0=makeQuery(id+"F1.opExtrude","CAP_FACE",FACE,{"disambiguationData":[OSD([sQuery(id+"F0.wireOp",EDGE,"E0"),sQuery(id+"F0.wireOp",EDGE,"E1"),sQuery(id+"F0.wireOp",EDGE,"E3"),sQuery(id+"F0.wireOp",EDGE,"E5"),sQuery(id+"F0.wireOp",EDGE,"E6"),sQuery(id+"F0.wireOp",EDGE,"E7"),sQuery(id+"F0.wireOp",EDGE,"E803"),sQuery(id+"F0.wireOp",EDGE,"E804"),sQuery(id+"F0.wireOp",EDGE,"E805"),sQuery(id+"F0.wireOp",EDGE,"E806"),sQuery(id+"F0.wireOp",EDGE,"E807"),sQuery(id+"F0.wireOp",EDGE,"E808"),sQuery(id+"F0.wireOp",EDGE,"E809"),sQuery(id+"F0.wireOp",EDGE,"E810"),sQuery(id+"F0.wireOp",EDGE,"E811"),sQuery(id+"F0.wireOp",EDGE,"E812"),sQuery(id+"F0.wireOp",EDGE,"E813"),sQuery(id+"F0.wireOp",EDGE,"E814"),sQuery(id+"F0.wireOp",EDGE,"E815"),sQuery(id+"F0.wireOp",EDGE,"E816"),sQuery(id+"F0.wireOp",EDGE,"E817"),sQuery(id+"F0.wireOp",EDGE,"E818"),sQuery(id+"F0.wireOp",EDGE,"E819"),sQuery(id+"F0.wireOp",EDGE,"E820"),sQuery(id+"F0.wireOp",EDGE,"E821"),sQuery(id+"F0.wireOp",EDGE,"E822"),sQuery(id+"F0.wireOp",EDGE,"E823"),sQuery(id+"F0.wireOp",EDGE,"E824"),sQuery(id+"F0.wireOp",EDGE,"E825"),sQuery(id+"F0.wireOp",EDGE,"E826"),sQuery(id+"F0.wireOp",EDGE,"E827"),sQuery(id+"F0.wireOp",EDGE,"E828"),sQuery(id+"F0.wireOp",EDGE,"E829"),sQuery(id+"F0.wireOp",EDGE,"E830"),sQuery(id+"F0.wireOp",EDGE,"E831"),sQuery(id+"F0.wireOp",EDGE,"E832"),sQuery(id+"F0.wireOp",EDGE,"E833"),sQuery(id+"F0.wireOp",EDGE,"E834"),sQuery(id+"F0.wireOp",EDGE,"E835"),sQuery(id+"F0.wireOp",EDGE,"E836"),sQuery(id+"F0.wireOp",EDGE,"E837"),sQuery(id+"F0.wireOp",EDGE,"E838"),sQuery(id+"F0.wireOp",EDGE,"E839"),sQuery(id+"F0.wireOp",EDGE,"E840"),sQuery(id+"F0.wireOp",EDGE,"E841"),sQuery(id+"F0.wireOp",EDGE,"E842"),sQuery(id+"F0.wireOp",EDGE,"E843"),sQuery(id+"F0.wireOp",EDGE,"E844"),sQuery(id+"F0.wireOp",EDGE,"E845"),sQuery(id+"F0.wireOp",EDGE,"E846"),sQuery(id+"F0.wireOp",EDGE,"E847"),sQuery(id+"F0.wireOp",EDGE,"E848"),sQuery(id+"F0.wireOp",EDGE,"E849"),sQuery(id+"F0.wireOp",EDGE,"E850"),sQuery(id+"F0.wireOp",EDGE,"E851"),sQuery(id+"F0.wireOp",EDGE,"E852"),sQuery(id+"F0.wireOp",EDGE,"E853"),sQuery(id+"F0.wireOp",EDGE,"E854"),sQuery(id+"F0.wireOp",EDGE,"E855"),sQuery(id+"F0.wireOp",EDGE,"E856"),sQuery(id+"F0.wireOp",EDGE,"E857"),sQuery(id+"F0.wireOp",EDGE,"E858"),sQuery(id+"F0.wireOp",EDGE,"E859"),sQuery(id+"F0.wireOp",EDGE,"E860"),sQuery(id+"F0.wireOp",EDGE,"E861"),sQuery(id+"F0.wireOp",EDGE,"E862"),sQuery(id+"F0.wireOp",EDGE,"E863"),sQuery(id+"F0.wireOp",EDGE,"E864"),sQuery(id+"F0.wireOp",EDGE,"E865"),sQuery(id+"F0.wireOp",EDGE,"E866"),sQuery(id+"F0.wireOp",EDGE,"E867"),sQuery(id+"F0.wireOp",EDGE,"E868"),sQuery(id+"F0.wireOp",EDGE,"E869"),sQuery(id+"F0.wireOp",EDGE,"E870"),sQuery(id+"F0.wireOp",EDGE,"E871"),sQuery(id+"F0.wireOp",EDGE,"E872"),sQuery(id+"F0.wireOp",EDGE,"E873"),sQuery(id+"F0.wireOp",EDGE,"E874"),sQuery(id+"F0.wireOp",EDGE,"E875"),sQuery(id+"F0.wireOp",EDGE,"E876"),sQuery(id+"F0.wireOp",EDGE,"E877"),sQuery(id+"F0.wireOp",EDGE,"E878"),sQuery(id+"F0.wireOp",EDGE,"E879"),sQuery(id+"F0.wireOp",EDGE,"E880"),sQuery(id+"F0.wireOp",EDGE,"E881"),sQuery(id+"F0.wireOp",EDGE,"E882"),sQuery(id+"F0.wireOp",EDGE,"E883"),sQuery(id+"F0.wireOp",EDGE,"E884"),sQuery(id+"F0.wireOp",EDGE,"E885"),sQuery(id+"F0.wireOp",EDGE,"E886"),sQuery(id+"F0.wireOp",EDGE,"E887"),sQuery(id+"F0.wireOp",EDGE,"E888"),sQuery(id+"F0.wireOp",EDGE,"E889"),sQuery(id+"F0.wireOp",EDGE,"E890"),sQuery(id+"F0.wireOp",EDGE,"E891"),sQuery(id+"F0.wireOp",EDGE,"E892"),sQuery(id+"F0.wireOp",EDGE,"E893"),sQuery(id+"F0.wireOp",EDGE,"E894"),sQuery(id+"F0.wireOp",EDGE,"E895"),sQuery(id+"F0.wireOp",EDGE,"E896"),sQuery(id+"F0.wireOp",EDGE,"E897"),sQuery(id+"F0.wireOp",EDGE,"E898"),sQuery(id+"F0.wireOp",EDGE,"E899"),sQuery(id+"F0.wireOp",EDGE,"E900"),sQuery(id+"F0.wireOp",EDGE,"E901"),sQuery(id+"F0.wireOp",EDGE,"E902"),sQuery(id+"F0.wireOp",EDGE,"E903"),sQuery(id+"F0.wireOp",EDGE,"E904"),sQuery(id+"F0.wireOp",EDGE,"E905"),sQuery(id+"F0.wireOp",EDGE,"E906"),sQuery(id+"F0.wireOp",EDGE,"E907"),sQuery(id+"F0.wireOp",EDGE,"E908"),sQuery(id+"F0.wireOp",EDGE,"E909"),sQuery(id+"F0.wireOp",EDGE,"E910"),sQuery(id+"F0.wireOp",EDGE,"E911"),sQuery(id+"F0.wireOp",EDGE,"E912"),sQuery(id+"F0.wireOp",EDGE,"E913"),sQuery(id+"F0.wireOp",EDGE,"E914"),sQuery(id+"F0.wireOp",EDGE,"E915"),sQuery(id+"F0.wireOp",EDGE,"E916"),sQuery(id+"F0.wireOp",EDGE,"E917"),sQuery(id+"F0.wireOp",EDGE,"E918"),sQuery(id+"F0.wireOp",EDGE,"E919"),sQuery(id+"F0.wireOp",EDGE,"E920"),sQuery(id+"F0.wireOp",EDGE,"E921"),sQuery(id+"F0.wireOp",EDGE,"E922"),sQuery(id+"F0.wireOp",EDGE,"E923"),sQuery(id+"F0.wireOp",EDGE,"E924"),sQuery(id+"F0.wireOp",EDGE,"E925"),sQuery(id+"F0.wireOp",EDGE,"E926"),sQuery(id+"F0.wireOp",EDGE,"E927"),sQuery(id+"F0.wireOp",EDGE,"E928"),sQuery(id+"F0.wireOp",EDGE,"E929"),sQuery(id+"F0.wireOp",EDGE,"E930"),sQuery(id+"F0.wireOp",EDGE,"E931"),sQuery(id+"F0.wireOp",EDGE,"E932"),sQuery(id+"F0.wireOp",EDGE,"E933"),sQuery(id+"F0.wireOp",EDGE,"E934"),sQuery(id+"F0.wireOp",EDGE,"E935"),sQuery(id+"F0.wireOp",EDGE,"E936"),sQuery(id+"F0.wireOp",EDGE,"E938"),sQuery(id+"F0.wireOp",EDGE,"E939"),sQuery(id+"F0.wireOp",EDGE,"E940"),sQuery(id+"F0.wireOp",EDGE,"E942"),sQuery(id+"F0.wireOp",EDGE,"E943"),sQuery(id+"F0.wireOp",EDGE,"E944"),sQuery(id+"F0.wireOp",EDGE,"E945"),sQuery(id+"F0.wireOp",EDGE,"E946"),sQuery(id+"F0.wireOp",EDGE,"E947"),sQuery(id+"F0.wireOp",EDGE,"E948"),sQuery(id+"F0.wireOp",EDGE,"E949"),sQuery(id+"F0.wireOp",EDGE,"E950"),sQuery(id+"F0.wireOp",EDGE,"E951"),sQuery(id+"F0.wireOp",EDGE,"E952"),sQuery(id+"F0.wireOp",EDGE,"E953"),sQuery(id+"F0.wireOp",EDGE,"E955"),sQuery(id+"F0.wireOp",EDGE,"E956"),sQuery(id+"F0.wireOp",EDGE,"E957"),sQuery(id+"F0.wireOp",EDGE,"E959"),sQuery(id+"F0.wireOp",EDGE,"E960"),sQuery(id+"F0.wireOp",EDGE,"E961"),sQuery(id+"F0.wireOp",EDGE,"E962"),sQuery(id+"F0.wireOp",EDGE,"E963"),sQuery(id+"F0.wireOp",EDGE,"E964"),sQuery(id+"F0.wireOp",EDGE,"E965"),sQuery(id+"F0.wireOp",EDGE,"E966"),sQuery(id+"F0.wireOp",EDGE,"E967"),sQuery(id+"F0.wireOp",EDGE,"E968"),sQuery(id+"F0.wireOp",EDGE,"E969"),sQuery(id+"F0.wireOp",EDGE,"E970"),sQuery(id+"F0.wireOp",EDGE,"E971"),sQuery(id+"F0.wireOp",EDGE,"E972"),sQuery(id+"F0.wireOp",EDGE,"E973"),sQuery(id+"F0.wireOp",EDGE,"E974"),sQuery(id+"F0.wireOp",EDGE,"E975"),sQuery(id+"F0.wireOp",EDGE,"E976"),sQuery(id+"F0.wireOp",EDGE,"E977"),sQuery(id+"F0.wireOp",EDGE,"E978"),sQuery(id+"F0.wireOp",EDGE,"E979"),sQuery(id+"F0.wireOp",EDGE,"E980"),sQuery(id+"F0.wireOp",EDGE,"E981"),sQuery(id+"F0.wireOp",EDGE,"E982"),sQuery(id+"F0.wireOp",EDGE,"E983"),sQuery(id+"F0.wireOp",EDGE,"E984"),sQuery(id+"F0.wireOp",EDGE,"E985"),sQuery(id+"F0.wireOp",EDGE,"E986"),sQuery(id+"F0.wireOp",EDGE,"E987"),sQuery(id+"F0.wireOp",EDGE,"E988"),sQuery(id+"F0.wireOp",EDGE,"E989"),sQuery(id+"F0.wireOp",EDGE,"E990"),sQuery(id+"F0.wireOp",EDGE,"E991"),sQuery(id+"F0.wireOp",EDGE,"E992"),sQuery(id+"F0.wireOp",EDGE,"E993"),sQuery(id+"F0.wireOp",EDGE,"E994"),sQuery(id+"F0.wireOp",EDGE,"E995"),sQuery(id+"F0.wireOp",EDGE,"E996"),sQuery(id+"F0.wireOp",EDGE,"E997"),sQuery(id+"F0.wireOp",EDGE,"E998"),sQuery(id+"F0.wireOp",EDGE,"E999"),sQuery(id+"F0.wireOp",EDGE,"E1000"),sQuery(id+"F0.wireOp",EDGE,"E1001"),sQuery(id+"F0.wireOp",EDGE,"E1002"),sQuery(id+"F0.wireOp",EDGE,"E1003"),sQuery(id+"F0.wireOp",EDGE,"E1004"),sQuery(id+"F0.wireOp",EDGE,"E1005"),sQuery(id+"F0.wireOp",EDGE,"E1006"),sQuery(id+"F0.wireOp",EDGE,"E1007"),sQuery(id+"F0.wireOp",EDGE,"E1008"),sQuery(id+"F0.wireOp",EDGE,"E1009"),sQuery(id+"F0.wireOp",EDGE,"E1010"),sQuery(id+"F0.wireOp",EDGE,"E1011"),sQuery(id+"F0.wireOp",EDGE,"E1012"),sQuery(id+"F0.wireOp",EDGE,"E1013"),sQuery(id+"F0.wireOp",EDGE,"E1014"),sQuery(id+"F0.wireOp",EDGE,"E1015"),sQuery(id+"F0.wireOp",EDGE,"E1016"),sQuery(id+"F0.wireOp",EDGE,"E1017"),sQuery(id+"F0.wireOp",EDGE,"E1018"),sQuery(id+"F0.wireOp",EDGE,"E1019"),sQuery(id+"F0.wireOp",EDGE,"E1020"),sQuery(id+"F0.wireOp",EDGE,"E1021"),sQuery(id+"F0.wireOp",EDGE,"E1022"),sQuery(id+"F0.wireOp",EDGE,"E1023"),sQuery(id+"F0.wireOp",EDGE,"E1024"),sQuery(id+"F0.wireOp",EDGE,"E1025"),sQuery(id+"F0.wireOp",EDGE,"E1026"),sQuery(id+"F0.wireOp",EDGE,"E1027"),sQuery(id+"F0.wireOp",EDGE,"E1028"),sQuery(id+"F0.wireOp",EDGE,"E1029"),sQuery(id+"F0.wireOp",EDGE,"E1030"),sQuery(id+"F0.wireOp",EDGE,"E1031"),sQuery(id+"F0.wireOp",EDGE,"E1032"),sQuery(id+"F0.wireOp",EDGE,"E1033"),sQuery(id+"F0.wireOp",EDGE,"E1034"),sQuery(id+"F0.wireOp",EDGE,"E1220"),sQuery(id+"F0.wireOp",EDGE,"E1221"),sQuery(id+"F0.wireOp",EDGE,"E1222"),sQuery(id+"F0.wireOp",EDGE,"E1223"),sQuery(id+"F0.wireOp",EDGE,"E1224"),sQuery(id+"F0.wireOp",EDGE,"E1225"),sQuery(id+"F0.wireOp",EDGE,"E1226"),sQuery(id+"F0.wireOp",EDGE,"E1227"),sQuery(id+"F0.wireOp",EDGE,"E1228"),sQuery(id+"F0.wireOp",EDGE,"E1229"),sQuery(id+"F0.wireOp",EDGE,"E1230")])],"isStart":false});
            var sketch = newSketch(context, id + "F20", { "sketchPlane" : qUnion([Q0])});
            skCircle(sketch, "E1250", {"center": v(-245.05, 134.48) * mm, "radius": 1.6 * mm});
            skCircle(sketch, "E1251", {"center": v(-36.03, 134.48) * mm, "radius": 1.6 * mm});
            skCircle(sketch, "E1252", {"center": v(-36.03, -74.54) * mm, "radius": 1.6 * mm});
            skCircle(sketch, "E1253", {"center": v(-245.05, -74.52) * mm, "radius": 1.6 * mm});
            skLineSegment(sketch, "E1254.bottom", {"start": v(-247.35, 136.7) * mm, "end": v(-33.35, 136.7) * mm});
            skLineSegment(sketch, "E1254.top", {"start": v(-247.35, -77.3) * mm, "end": v(-33.35, -77.3) * mm});
            skLineSegment(sketch, "E1254.left", {"start": v(-247.35, 136.7) * mm, "end": v(-247.35, -77.3) * mm});
            skLineSegment(sketch, "E1254.right", {"start": v(-33.35, 136.7) * mm, "end": v(-33.35, -77.3) * mm});
            skSolve(sketch);
        }
        {
            var Q0;
            {var subQ5=makeQuery(id+"F1.opExtrude","CAP_EDGE",EDGE,{"disambiguationData":[OSD([sQuery(id+"F0.wireOp",EDGE,"E853")])],"isStart":false});Q0=makeQuery(id+"F20.imprint","IMPRINT",FACE,{"disambiguationData":[TD([[makeQuery(id+"F20.imprint","IMPRINT",EDGE,{"derivedFrom":subQ5}),1.0]])]});}
            var Q1;
            {var subQ5=makeQuery(id+"F1.opExtrude","CAP_EDGE",EDGE,{"disambiguationData":[OSD([sQuery(id+"F0.wireOp",EDGE,"E803")])],"isStart":false});Q1=makeQuery(id+"F20.imprint","IMPRINT",FACE,{"disambiguationData":[TD([[makeQuery(id+"F20.imprint","IMPRINT",EDGE,{"derivedFrom":subQ5}),-1.0]])]});}
            var Q2;
            {var subQ5=makeQuery(id+"F1.opExtrude","CAP_EDGE",EDGE,{"disambiguationData":[OSD([sQuery(id+"F0.wireOp",EDGE,"E917")])],"isStart":false});Q2=makeQuery(id+"F20.imprint","IMPRINT",FACE,{"disambiguationData":[TD([[makeQuery(id+"F20.imprint","IMPRINT",EDGE,{"derivedFrom":subQ5}),-1.0]])]});}
            var Q3;
            Q3=makeQuery(id+"F20.imprint","IMPRINT",FACE,{"disambiguationData":[TD([[makeQuery(id+"F20.imprint","IMPRINT",EDGE,{"derivedFrom":makeQuery(id+"F1.opExtrude","CAP_EDGE",EDGE,{"disambiguationData":[OSD([sQuery(id+"F0.wireOp",EDGE,"E3")])],"isStart":false})}),1.0]])]});
            var Q4;
            Q4=makeQuery(id+"F20.imprint","IMPRINT",FACE,{"disambiguationData":[TD([[makeQuery(id+"F20.imprint","IMPRINT",EDGE,{"derivedFrom":makeQuery(id+"F1.opExtrude","CAP_EDGE",EDGE,{"disambiguationData":[OSD([sQuery(id+"F0.wireOp",EDGE,"E804")])],"isStart":false})}),1.0]])]});
            var Q5;
            Q5=makeQuery(id+"F20.imprint","IMPRINT",FACE,{"disambiguationData":[TD([[makeQuery(id+"F20.imprint","IMPRINT",EDGE,{"derivedFrom":makeQuery(id+"F1.opExtrude","CAP_EDGE",EDGE,{"disambiguationData":[OSD([sQuery(id+"F0.wireOp",EDGE,"E835")])],"isStart":false})}),-1.0]])]});
            var Q6;
            Q6=makeQuery(id+"F20.imprint","IMPRINT",FACE,{"disambiguationData":[TD([[makeQuery(id+"F20.imprint","IMPRINT",EDGE,{"derivedFrom":makeQuery(id+"F1.opExtrude","CAP_EDGE",EDGE,{"disambiguationData":[OSD([sQuery(id+"F0.wireOp",EDGE,"E818")])],"isStart":false})}),-1.0]])]});
            var Q7;
            Q7=makeQuery(id+"F20.imprint","IMPRINT",FACE,{"disambiguationData":[TD([[makeQuery(id+"F20.imprint","IMPRINT",EDGE,{"derivedFrom":makeQuery(id+"F1.opExtrude","CAP_EDGE",EDGE,{"disambiguationData":[OSD([sQuery(id+"F0.wireOp",EDGE,"E945")])],"isStart":false})}),-1.0]])]});
            var Q8;
            Q8=makeQuery(id+"F20.imprint","IMPRINT",FACE,{"disambiguationData":[TD([[makeQuery(id+"F20.imprint","IMPRINT",EDGE,{"derivedFrom":makeQuery(id+"F1.opExtrude","CAP_EDGE",EDGE,{"disambiguationData":[OSD([sQuery(id+"F0.wireOp",EDGE,"E3")])],"isStart":false})}),-1.0]])]});
            var Q9;
            Q9=makeQuery(id+"F20.imprint","IMPRINT",FACE,{"disambiguationData":[TD([[makeQuery(id+"F20.imprint","IMPRINT",EDGE,{"derivedFrom":makeQuery(id+"F1.opExtrude","CAP_EDGE",EDGE,{"disambiguationData":[OSD([sQuery(id+"F0.wireOp",EDGE,"E822")])],"isStart":false})}),1.0]])]});
            var Q10;
            Q10=makeQuery(id+"F20.imprint","IMPRINT",FACE,{"disambiguationData":[TD([[makeQuery(id+"F20.imprint","IMPRINT",EDGE,{"derivedFrom":makeQuery(id+"F1.opExtrude","CAP_EDGE",EDGE,{"disambiguationData":[OSD([sQuery(id+"F0.wireOp",EDGE,"E806")])],"isStart":false})}),1.0]])]});
            var Q11;
            Q11=makeQuery(id+"F20.imprint","IMPRINT",FACE,{"disambiguationData":[TD([[makeQuery(id+"F20.imprint","IMPRINT",EDGE,{"derivedFrom":makeQuery(id+"F1.opExtrude","CAP_EDGE",EDGE,{"disambiguationData":[OSD([sQuery(id+"F0.wireOp",EDGE,"E805")])],"isStart":false})}),-1.0]])]});
            var Q12;
            Q12=makeQuery(id+"F20.imprint","IMPRINT",FACE,{"disambiguationData":[TD([[makeQuery(id+"F20.imprint","IMPRINT",EDGE,{"derivedFrom":makeQuery(id+"F1.opExtrude","CAP_EDGE",EDGE,{"disambiguationData":[OSD([sQuery(id+"F0.wireOp",EDGE,"E1225")])],"isStart":false})}),1.0]])]});
            var Q13;
            Q13=makeQuery(id+"F20.imprint","IMPRINT",FACE,{"disambiguationData":[TD([[makeQuery(id+"F20.imprint","IMPRINT",EDGE,{"derivedFrom":makeQuery(id+"F1.opExtrude","CAP_EDGE",EDGE,{"disambiguationData":[OSD([sQuery(id+"F0.wireOp",EDGE,"E1224")])],"isStart":false})}),1.0]])]});
            var Q14;
            Q14=makeQuery(id+"F20.imprint","IMPRINT",FACE,{"disambiguationData":[TD([[makeQuery(id+"F20.imprint","IMPRINT",EDGE,{"derivedFrom":makeQuery(id+"F1.opExtrude","CAP_EDGE",EDGE,{"disambiguationData":[OSD([sQuery(id+"F0.wireOp",EDGE,"E1228")])],"isStart":false})}),1.0]])]});
            var Q15;
            Q15=makeQuery(id+"F20.imprint","IMPRINT",FACE,{"disambiguationData":[TD([[makeQuery(id+"F20.imprint","IMPRINT",EDGE,{"derivedFrom":makeQuery(id+"F1.opExtrude","CAP_EDGE",EDGE,{"disambiguationData":[OSD([sQuery(id+"F0.wireOp",EDGE,"E1226")])],"isStart":false})}),1.0]])]});
            var Q16;
            Q16=makeQuery(id+"F20.imprint","IMPRINT",FACE,{"disambiguationData":[TD([[makeQuery(id+"F20.imprint","IMPRINT",EDGE,{"derivedFrom":makeQuery(id+"F1.opExtrude","CAP_EDGE",EDGE,{"disambiguationData":[OSD([sQuery(id+"F0.wireOp",EDGE,"E1227")])],"isStart":false})}),1.0]])]});
            var Q17;
            Q17=makeQuery(id+"F20.imprint","IMPRINT",FACE,{"disambiguationData":[TD([[makeQuery(id+"F20.imprint","IMPRINT",EDGE,{"derivedFrom":makeQuery(id+"F1.opExtrude","CAP_EDGE",EDGE,{"disambiguationData":[OSD([sQuery(id+"F0.wireOp",EDGE,"E1223")])],"isStart":false})}),1.0]])]});
            var Q18;
            Q18=makeQuery(id+"F20.imprint","IMPRINT",FACE,{"disambiguationData":[TD([[makeQuery(id+"F20.imprint","IMPRINT",EDGE,{"derivedFrom":makeQuery(id+"F1.opExtrude","CAP_EDGE",EDGE,{"disambiguationData":[OSD([sQuery(id+"F0.wireOp",EDGE,"E1222")])],"isStart":false})}),1.0]])]});
            extrude(context, id + "F21", {"entities" : qUnion([Q0, Q1, Q2, Q3, Q4, Q5, Q6, Q7, Q8, Q9, Q10, Q11, Q12, Q13, Q14, Q15, Q16, Q17, Q18]), "depth" : 2.5 * mm});
        }
    });
